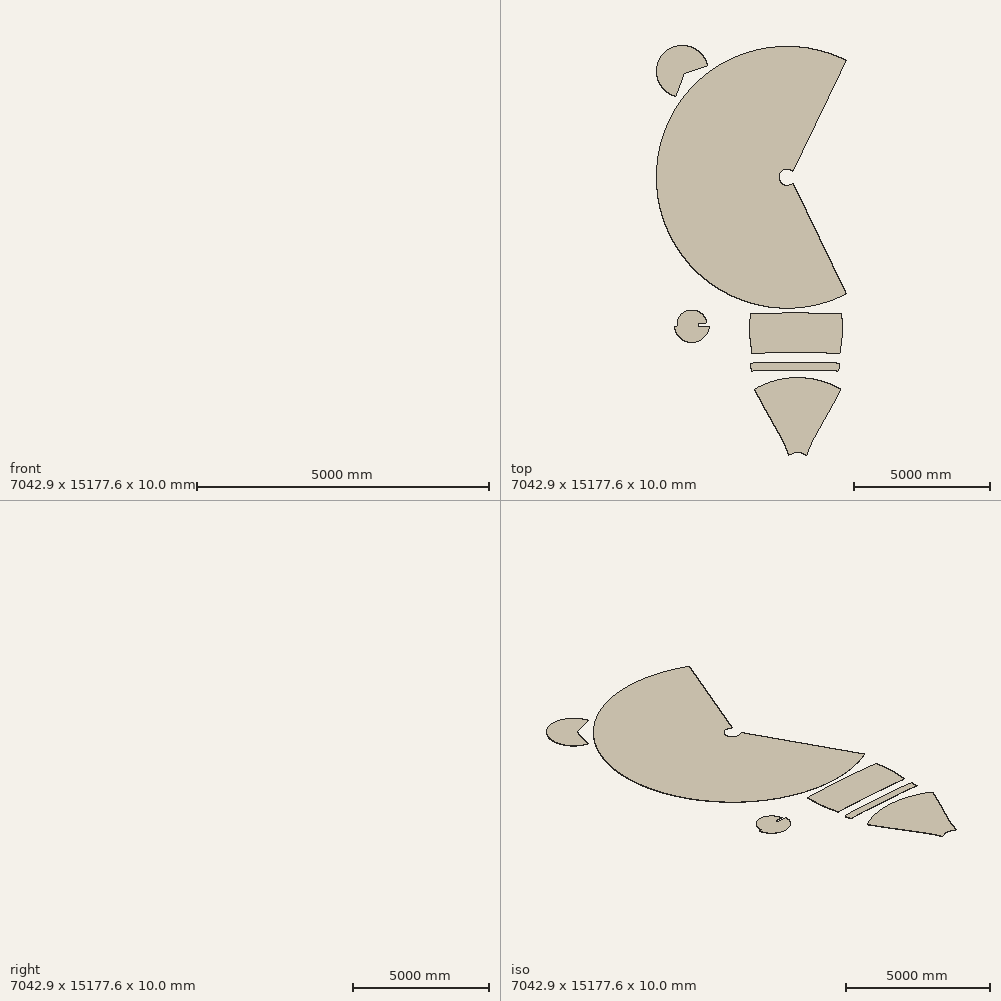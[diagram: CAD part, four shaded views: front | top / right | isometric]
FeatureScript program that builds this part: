
annotation { "Feature Type Name" : "Feature", "Feature Type Description" : "" }
export const myFeature = defineFeature(function(context is Context, id is Id, definition is map)
    precondition{}
    {
        {
            var Q0;
            Q0=qCreatedBy(makeId("Top.planeOp"),FACE);
            var sketch = newSketch(context, id + "F0", { "sketchPlane" : qUnion([Q0])});
            skLineSegment(sketch, "E0", {"start": v(3689.21, 4533.13) * mm, "end": v(3688.96, 4522.87) * mm});
            skLineSegment(sketch, "E1", {"start": v(3688.96, 4522.87) * mm, "end": v(3679.89, 4525.24) * mm});
            skLineSegment(sketch, "E2", {"start": v(3679.89, 4525.24) * mm, "end": v(3689.21, 4533.13) * mm});
            skLineSegment(sketch, "E3", {"start": v(4140.22, 4519.46) * mm, "end": v(4117.49, 4558.33) * mm});
            skLineSegment(sketch, "E4", {"start": v(4117.49, 4558.33) * mm, "end": v(4094.03, 4596.74) * mm});
            skLineSegment(sketch, "E5", {"start": v(4094.03, 4596.74) * mm, "end": v(4069.87, 4634.67) * mm});
            skLineSegment(sketch, "E6", {"start": v(4069.87, 4634.67) * mm, "end": v(4045.02, 4672.12) * mm});
            skLineSegment(sketch, "E7", {"start": v(4045.02, 4672.12) * mm, "end": v(4019.5, 4709.08) * mm});
            skLineSegment(sketch, "E8", {"start": v(4019.5, 4709.08) * mm, "end": v(3993.33, 4745.54) * mm});
            skLineSegment(sketch, "E9", {"start": v(3993.33, 4745.54) * mm, "end": v(3966.52, 4781.49) * mm});
            skLineSegment(sketch, "E10", {"start": v(3966.52, 4781.49) * mm, "end": v(3939.1, 4816.92) * mm});
            skLineSegment(sketch, "E11", {"start": v(3939.1, 4816.92) * mm, "end": v(3911.07, 4851.83) * mm});
            skLineSegment(sketch, "E12", {"start": v(3911.07, 4851.83) * mm, "end": v(3882.46, 4886.21) * mm});
            skLineSegment(sketch, "E13", {"start": v(3882.46, 4886.21) * mm, "end": v(3823.55, 4953.35) * mm});
            skLineSegment(sketch, "E14", {"start": v(3823.55, 4953.35) * mm, "end": v(3762.5, 5018.27) * mm});
            skLineSegment(sketch, "E15", {"start": v(3762.5, 5018.27) * mm, "end": v(3699.43, 5080.93) * mm});
            skLineSegment(sketch, "E16", {"start": v(3699.43, 5080.93) * mm, "end": v(3634.48, 5141.28) * mm});
            skLineSegment(sketch, "E17", {"start": v(3634.48, 5141.28) * mm, "end": v(3567.78, 5199.28) * mm});
            skLineSegment(sketch, "E18", {"start": v(3567.78, 5199.28) * mm, "end": v(3499.44, 5254.88) * mm});
            skLineSegment(sketch, "E19", {"start": v(3499.44, 5254.88) * mm, "end": v(3429.6, 5308.04) * mm});
            skLineSegment(sketch, "E20", {"start": v(3429.6, 5308.04) * mm, "end": v(3358.36, 5358.74) * mm});
            skLineSegment(sketch, "E21", {"start": v(3358.36, 5358.74) * mm, "end": v(3285.85, 5406.94) * mm});
            skLineSegment(sketch, "E22", {"start": v(3285.85, 5406.94) * mm, "end": v(3212.2, 5452.6) * mm});
            skLineSegment(sketch, "E23", {"start": v(3212.2, 5452.6) * mm, "end": v(3137.5, 5495.73) * mm});
            skLineSegment(sketch, "E24", {"start": v(3137.5, 5495.73) * mm, "end": v(3061.89, 5536.28) * mm});
            skLineSegment(sketch, "E25", {"start": v(3061.89, 5536.28) * mm, "end": v(2985.46, 5574.24) * mm});
            skLineSegment(sketch, "E26", {"start": v(2985.46, 5574.24) * mm, "end": v(2908.33, 5609.6) * mm});
            skLineSegment(sketch, "E27", {"start": v(2908.33, 5609.6) * mm, "end": v(2830.62, 5642.34) * mm});
            skLineSegment(sketch, "E28", {"start": v(2830.62, 5642.34) * mm, "end": v(2752.41, 5672.45) * mm});
            skLineSegment(sketch, "E29", {"start": v(2752.41, 5672.45) * mm, "end": v(2673.83, 5699.94) * mm});
            skLineSegment(sketch, "E30", {"start": v(2673.83, 5699.94) * mm, "end": v(2594.97, 5724.78) * mm});
            skLineSegment(sketch, "E31", {"start": v(2594.97, 5724.78) * mm, "end": v(2515.93, 5747) * mm});
            skLineSegment(sketch, "E32", {"start": v(2515.93, 5747) * mm, "end": v(2436.82, 5766.57) * mm});
            skLineSegment(sketch, "E33", {"start": v(2436.82, 5766.57) * mm, "end": v(2357.73, 5783.51) * mm});
            skLineSegment(sketch, "E34", {"start": v(2357.73, 5783.51) * mm, "end": v(2278.75, 5797.83) * mm});
            skLineSegment(sketch, "E35", {"start": v(2278.75, 5797.83) * mm, "end": v(2199.99, 5809.53) * mm});
            skLineSegment(sketch, "E36", {"start": v(2199.99, 5809.53) * mm, "end": v(2121.53, 5818.63) * mm});
            skLineSegment(sketch, "E37", {"start": v(2121.53, 5818.63) * mm, "end": v(2043.46, 5825.14) * mm});
            skLineSegment(sketch, "E38", {"start": v(2043.46, 5825.14) * mm, "end": v(1965.88, 5829.08) * mm});
            skLineSegment(sketch, "E39", {"start": v(1965.88, 5829.08) * mm, "end": v(1888.87, 5830.46) * mm});
            skLineSegment(sketch, "E40", {"start": v(1888.87, 5830.46) * mm, "end": v(1812.52, 5829.3) * mm});
            skLineSegment(sketch, "E41", {"start": v(1812.52, 5829.3) * mm, "end": v(1736.9, 5825.62) * mm});
            skLineSegment(sketch, "E42", {"start": v(1736.9, 5825.62) * mm, "end": v(1662.11, 5819.46) * mm});
            skLineSegment(sketch, "E43", {"start": v(1662.11, 5819.46) * mm, "end": v(1588.22, 5810.83) * mm});
            skLineSegment(sketch, "E44", {"start": v(1588.22, 5810.83) * mm, "end": v(1515.31, 5799.76) * mm});
            skLineSegment(sketch, "E45", {"start": v(1515.31, 5799.76) * mm, "end": v(1479.25, 5793.32) * mm});
            skLineSegment(sketch, "E46", {"start": v(1479.25, 5793.32) * mm, "end": v(1443.46, 5786.29) * mm});
            skLineSegment(sketch, "E47", {"start": v(1443.46, 5786.29) * mm, "end": v(1407.95, 5778.65) * mm});
            skLineSegment(sketch, "E48", {"start": v(1407.95, 5778.65) * mm, "end": v(1372.74, 5770.43) * mm});
            skLineSegment(sketch, "E49", {"start": v(1372.74, 5770.43) * mm, "end": v(1337.82, 5761.62) * mm});
            skLineSegment(sketch, "E50", {"start": v(1337.82, 5761.62) * mm, "end": v(1303.22, 5752.23) * mm});
            skLineSegment(sketch, "E51", {"start": v(1303.22, 5752.23) * mm, "end": v(1268.94, 5742.26) * mm});
            skLineSegment(sketch, "E52", {"start": v(1268.94, 5742.26) * mm, "end": v(1234.98, 5731.72) * mm});
            skLineSegment(sketch, "E53", {"start": v(1234.98, 5731.72) * mm, "end": v(1201.36, 5720.61) * mm});
            skLineSegment(sketch, "E54", {"start": v(1201.36, 5720.61) * mm, "end": v(1168.09, 5708.94) * mm});
            skLineSegment(sketch, "E55", {"start": v(1168.09, 5708.94) * mm, "end": v(1135.17, 5696.7) * mm});
            skLineSegment(sketch, "E56", {"start": v(1135.17, 5696.7) * mm, "end": v(1102.61, 5683.91) * mm});
            skLineSegment(sketch, "E57", {"start": v(1102.61, 5683.91) * mm, "end": v(1070.42, 5670.57) * mm});
            skLineSegment(sketch, "E58", {"start": v(1070.42, 5670.57) * mm, "end": v(1038.61, 5656.69) * mm});
            skLineSegment(sketch, "E59", {"start": v(1038.61, 5656.69) * mm, "end": v(1007.19, 5642.26) * mm});
            skLineSegment(sketch, "E60", {"start": v(1007.19, 5642.26) * mm, "end": v(976.16, 5627.3) * mm});
            skLineSegment(sketch, "E61", {"start": v(976.16, 5627.3) * mm, "end": v(945.53, 5611.8) * mm});
            skLineSegment(sketch, "E62", {"start": v(945.53, 5611.8) * mm, "end": v(915.31, 5595.79) * mm});
            skLineSegment(sketch, "E63", {"start": v(915.31, 5595.79) * mm, "end": v(885.51, 5579.25) * mm});
            skLineSegment(sketch, "E64", {"start": v(885.51, 5579.25) * mm, "end": v(856.14, 5562.2) * mm});
            skLineSegment(sketch, "E65", {"start": v(856.14, 5562.2) * mm, "end": v(827.2, 5544.64) * mm});
            skLineSegment(sketch, "E66", {"start": v(827.2, 5544.64) * mm, "end": v(798.69, 5526.58) * mm});
            skLineSegment(sketch, "E67", {"start": v(798.69, 5526.58) * mm, "end": v(770.63, 5508.01) * mm});
            skLineSegment(sketch, "E68", {"start": v(770.63, 5508.01) * mm, "end": v(743.03, 5488.96) * mm});
            skLineSegment(sketch, "E69", {"start": v(743.03, 5488.96) * mm, "end": v(715.88, 5469.42) * mm});
            skLineSegment(sketch, "E70", {"start": v(715.88, 5469.42) * mm, "end": v(689.2, 5449.4) * mm});
            skLineSegment(sketch, "E71", {"start": v(689.2, 5449.4) * mm, "end": v(663, 5428.9) * mm});
            skLineSegment(sketch, "E72", {"start": v(663, 5428.9) * mm, "end": v(637.28, 5407.92) * mm});
            skLineSegment(sketch, "E73", {"start": v(637.28, 5407.92) * mm, "end": v(612.05, 5386.5) * mm});
            skLineSegment(sketch, "E74", {"start": v(612.05, 5386.5) * mm, "end": v(587.3, 5364.6) * mm});
            skLineSegment(sketch, "E75", {"start": v(587.3, 5364.6) * mm, "end": v(563.06, 5342.25) * mm});
            skLineSegment(sketch, "E76", {"start": v(563.06, 5342.25) * mm, "end": v(539.33, 5319.46) * mm});
            skLineSegment(sketch, "E77", {"start": v(539.33, 5319.46) * mm, "end": v(516.1, 5296.23) * mm});
            skLineSegment(sketch, "E78", {"start": v(516.1, 5296.23) * mm, "end": v(493.4, 5272.56) * mm});
            skLineSegment(sketch, "E79", {"start": v(493.4, 5272.56) * mm, "end": v(471.22, 5248.47) * mm});
            skLineSegment(sketch, "E80", {"start": v(471.22, 5248.47) * mm, "end": v(449.57, 5223.95) * mm});
            skLineSegment(sketch, "E81", {"start": v(449.57, 5223.95) * mm, "end": v(428.45, 5199.01) * mm});
            skLineSegment(sketch, "E82", {"start": v(428.45, 5199.01) * mm, "end": v(407.88, 5173.67) * mm});
            skLineSegment(sketch, "E83", {"start": v(407.88, 5173.67) * mm, "end": v(387.85, 5147.92) * mm});
            skLineSegment(sketch, "E84", {"start": v(387.85, 5147.92) * mm, "end": v(368.37, 5121.77) * mm});
            skLineSegment(sketch, "E85", {"start": v(368.37, 5121.77) * mm, "end": v(349.45, 5095.23) * mm});
            skLineSegment(sketch, "E86", {"start": v(349.45, 5095.23) * mm, "end": v(331.1, 5068.3) * mm});
            skLineSegment(sketch, "E87", {"start": v(331.1, 5068.3) * mm, "end": v(313.3, 5041) * mm});
            skLineSegment(sketch, "E88", {"start": v(313.3, 5041) * mm, "end": v(296.08, 5013.33) * mm});
            skLineSegment(sketch, "E89", {"start": v(296.08, 5013.33) * mm, "end": v(279.44, 4985.28) * mm});
            skLineSegment(sketch, "E90", {"start": v(279.44, 4985.28) * mm, "end": v(263.38, 4956.88) * mm});
            skLineSegment(sketch, "E91", {"start": v(263.38, 4956.88) * mm, "end": v(247.9, 4928.12) * mm});
            skLineSegment(sketch, "E92", {"start": v(247.9, 4928.12) * mm, "end": v(233.02, 4899) * mm});
            skLineSegment(sketch, "E93", {"start": v(233.02, 4899) * mm, "end": v(218.73, 4869.56) * mm});
            skLineSegment(sketch, "E94", {"start": v(218.73, 4869.56) * mm, "end": v(205.04, 4839.77) * mm});
            skLineSegment(sketch, "E95", {"start": v(205.04, 4839.77) * mm, "end": v(191.95, 4809.65) * mm});
            skLineSegment(sketch, "E96", {"start": v(191.95, 4809.65) * mm, "end": v(179.47, 4779.21) * mm});
            skLineSegment(sketch, "E97", {"start": v(179.47, 4779.21) * mm, "end": v(167.6, 4748.46) * mm});
            skLineSegment(sketch, "E98", {"start": v(167.6, 4748.46) * mm, "end": v(156.35, 4717.4) * mm});
            skLineSegment(sketch, "E99", {"start": v(156.35, 4717.4) * mm, "end": v(145.72, 4686.02) * mm});
            skLineSegment(sketch, "E100", {"start": v(145.72, 4686.02) * mm, "end": v(135.7, 4654.35) * mm});
            skLineSegment(sketch, "E101", {"start": v(135.7, 4654.35) * mm, "end": v(126.32, 4622.39) * mm});
            skLineSegment(sketch, "E102", {"start": v(126.32, 4622.39) * mm, "end": v(117.57, 4590.14) * mm});
            skLineSegment(sketch, "E103", {"start": v(117.57, 4590.14) * mm, "end": v(109.45, 4557.61) * mm});
            skLineSegment(sketch, "E104", {"start": v(109.45, 4557.61) * mm, "end": v(101.96, 4524.81) * mm});
            skLineSegment(sketch, "E105", {"start": v(101.96, 4524.81) * mm, "end": v(95.11, 4491.74) * mm});
            skLineSegment(sketch, "E106", {"start": v(95.11, 4491.74) * mm, "end": v(88.9, 4458.41) * mm});
            skLineSegment(sketch, "E107", {"start": v(88.9, 4458.41) * mm, "end": v(83.35, 4424.83) * mm});
            skLineSegment(sketch, "E108", {"start": v(83.35, 4424.83) * mm, "end": v(78.44, 4391) * mm});
            skLineSegment(sketch, "E109", {"start": v(78.44, 4391) * mm, "end": v(74.18, 4356.92) * mm});
            skLineSegment(sketch, "E110", {"start": v(74.18, 4356.92) * mm, "end": v(70.57, 4322.6) * mm});
            skLineSegment(sketch, "E111", {"start": v(70.57, 4322.6) * mm, "end": v(67.62, 4288.06) * mm});
            skLineSegment(sketch, "E112", {"start": v(67.62, 4288.06) * mm, "end": v(65.33, 4253.3) * mm});
            skLineSegment(sketch, "E113", {"start": v(65.33, 4253.3) * mm, "end": v(63.7, 4218.3) * mm});
            skLineSegment(sketch, "E114", {"start": v(63.7, 4218.3) * mm, "end": v(62.73, 4183.1) * mm});
            skLineSegment(sketch, "E115", {"start": v(62.73, 4183.1) * mm, "end": v(62.42, 4147.69) * mm});
            skLineSegment(sketch, "E116", {"start": v(62.42, 4147.69) * mm, "end": v(62.78, 4112.07) * mm});
            skLineSegment(sketch, "E117", {"start": v(62.78, 4112.07) * mm, "end": v(63.81, 4076.27) * mm});
            skLineSegment(sketch, "E118", {"start": v(63.81, 4076.27) * mm, "end": v(65.51, 4040.27) * mm});
            skLineSegment(sketch, "E119", {"start": v(65.51, 4040.27) * mm, "end": v(67.89, 4004.08) * mm});
            skLineSegment(sketch, "E120", {"start": v(67.89, 4004.08) * mm, "end": v(70.93, 3967.72) * mm});
            skLineSegment(sketch, "E121", {"start": v(70.93, 3967.72) * mm, "end": v(74.66, 3931.18) * mm});
            skLineSegment(sketch, "E122", {"start": v(74.66, 3931.18) * mm, "end": v(79.05, 3894.48) * mm});
            skLineSegment(sketch, "E123", {"start": v(79.05, 3894.48) * mm, "end": v(89.88, 3820.58) * mm});
            skLineSegment(sketch, "E124", {"start": v(89.88, 3820.58) * mm, "end": v(103.44, 3746.07) * mm});
            skLineSegment(sketch, "E125", {"start": v(103.44, 3746.07) * mm, "end": v(119.71, 3671) * mm});
            skLineSegment(sketch, "E126", {"start": v(119.71, 3671) * mm, "end": v(138.72, 3595.4) * mm});
            skLineSegment(sketch, "E127", {"start": v(138.72, 3595.4) * mm, "end": v(160.46, 3519.3) * mm});
            skLineSegment(sketch, "E128", {"start": v(160.46, 3519.3) * mm, "end": v(184.95, 3442.76) * mm});
            skLineSegment(sketch, "E129", {"start": v(184.95, 3442.76) * mm, "end": v(212.17, 3365.8) * mm});
            skLineSegment(sketch, "E130", {"start": v(212.17, 3365.8) * mm, "end": v(242.13, 3288.46) * mm});
            skLineSegment(sketch, "E131", {"start": v(242.13, 3288.46) * mm, "end": v(274.82, 3210.77) * mm});
            skLineSegment(sketch, "E132", {"start": v(274.82, 3210.77) * mm, "end": v(310.24, 3132.76) * mm});
            skLineSegment(sketch, "E133", {"start": v(310.24, 3132.76) * mm, "end": v(348.39, 3054.47) * mm});
            skLineSegment(sketch, "E134", {"start": v(348.39, 3054.47) * mm, "end": v(389.25, 2975.93) * mm});
            skLineSegment(sketch, "E135", {"start": v(389.25, 2975.93) * mm, "end": v(432.82, 2897.15) * mm});
            skLineSegment(sketch, "E136", {"start": v(432.82, 2897.15) * mm, "end": v(479.1, 2818.17) * mm});
            skLineSegment(sketch, "E137", {"start": v(479.1, 2818.17) * mm, "end": v(528.04, 2739) * mm});
            skLineSegment(sketch, "E138", {"start": v(528.04, 2739) * mm, "end": v(579.66, 2659.68) * mm});
            skLineSegment(sketch, "E139", {"start": v(579.66, 2659.68) * mm, "end": v(633.94, 2580.2) * mm});
            skLineSegment(sketch, "E140", {"start": v(633.94, 2580.2) * mm, "end": v(690.85, 2500.62) * mm});
            skLineSegment(sketch, "E141", {"start": v(690.85, 2500.62) * mm, "end": v(750.38, 2420.92) * mm});
            skLineSegment(sketch, "E142", {"start": v(750.38, 2420.92) * mm, "end": v(812.5, 2341.12) * mm});
            skLineSegment(sketch, "E143", {"start": v(812.5, 2341.12) * mm, "end": v(877.2, 2261.24) * mm});
            skLineSegment(sketch, "E144", {"start": v(877.2, 2261.24) * mm, "end": v(944.46, 2181.27) * mm});
            skLineSegment(sketch, "E145", {"start": v(944.46, 2181.27) * mm, "end": v(1086.5, 2021.14) * mm});
            skLineSegment(sketch, "E146", {"start": v(1086.5, 2021.14) * mm, "end": v(1238.44, 1860.72) * mm});
            skLineSegment(sketch, "E147", {"start": v(1238.44, 1860.72) * mm, "end": v(1400, 1700) * mm});
            skLineSegment(sketch, "E148", {"start": v(1400, 1700) * mm, "end": v(1570.92, 1538.9) * mm});
            skLineSegment(sketch, "E149", {"start": v(1570.92, 1538.9) * mm, "end": v(1750.89, 1377.31) * mm});
            skLineSegment(sketch, "E150", {"start": v(1750.89, 1377.31) * mm, "end": v(1939.6, 1215.06) * mm});
            skLineSegment(sketch, "E151", {"start": v(1939.6, 1215.06) * mm, "end": v(2136.68, 1051.94) * mm});
            skLineSegment(sketch, "E152", {"start": v(2136.68, 1051.94) * mm, "end": v(2554.47, 721.93) * mm});
            skLineSegment(sketch, "E153", {"start": v(2554.47, 721.93) * mm, "end": v(3000.97, 384.44) * mm});
            skLineSegment(sketch, "E154", {"start": v(3000.97, 384.44) * mm, "end": v(3964.87, -329.08) * mm});
            skLineSegment(sketch, "E155", {"start": v(1447.12, 4527.46) * mm, "end": v(1247.66, 4747.46) * mm});
            skLineSegment(sketch, "E156", {"start": v(1513.24, 4570.67) * mm, "end": v(1323.36, 4814.66) * mm});
            skLineSegment(sketch, "E157", {"start": v(4034.03, 4649.95) * mm, "end": v(4487.9, 4649.95) * mm});
            skLineSegment(sketch, "E158", {"start": v(4034.03, 4772.78) * mm, "end": v(4487.9, 4772.78) * mm});
            skLineSegment(sketch, "E159", {"start": v(4487.9, 4772.78) * mm, "end": v(4487.9, 4527.12) * mm});
            skLineSegment(sketch, "E160", {"start": v(4487.9, 4527.12) * mm, "end": v(4034.03, 4527.12) * mm});
            skLineSegment(sketch, "E161", {"start": v(4034.03, 4527.12) * mm, "end": v(4034.03, 4772.78) * mm});
            skLineSegment(sketch, "E162", {"start": v(3708.57, 4527.12) * mm, "end": v(4809.75, 4527.12) * mm});
            skLineSegment(sketch, "E163", {"start": v(3672.75, 4500.41) * mm, "end": v(3636.94, 4473.7) * mm});
            skLineSegment(sketch, "E164", {"start": v(3704.91, 4531.44) * mm, "end": v(3669.18, 4504.72) * mm});
            skLineSegment(sketch, "E165", {"start": v(3669.18, 4504.72) * mm, "end": v(3628.22, 4500.41) * mm});
            skLineSegment(sketch, "E166", {"start": v(3711.49, 4523.63) * mm, "end": v(3675.46, 4495.62) * mm});
            skLineSegment(sketch, "E167", {"start": v(3675.46, 4495.62) * mm, "end": v(3664.7, 4457.04) * mm});
            skLineSegment(sketch, "E168", {"start": v(3672.75, 4500.41) * mm, "end": v(3708.57, 4527.12) * mm});
            skLineSegment(sketch, "E169", {"start": v(3685.87, 4527.86) * mm, "end": v(3654.62, 4550.77) * mm});
            skLineSegment(sketch, "E170", {"start": v(3654.62, 4550.77) * mm, "end": v(3485.23, 4535.65) * mm});
            skLineSegment(sketch, "E171", {"start": v(1299.6, 3557.02) * mm, "end": v(1190.33, 3465.32) * mm});
            skLineSegment(sketch, "E172", {"start": v(3708.57, 4527.12) * mm, "end": v(3765.21, 4574.65) * mm});
            skCircle(sketch, "E173", {"center": v(1186.85, 9802.11) * mm, "radius": 552.4 * mm});
            skCircle(sketch, "E174", {"center": v(1186.85, 9802.11) * mm, "radius": 652.4 * mm});
            skLineSegment(sketch, "E175", {"start": v(932.85, 9722.74) * mm, "end": v(1440.85, 9722.74) * mm});
            skLineSegment(sketch, "E176", {"start": v(932.85, 9881.49) * mm, "end": v(1440.85, 9881.49) * mm});
            skLineSegment(sketch, "E177", {"start": v(932.85, 9960.86) * mm, "end": v(1440.85, 9960.86) * mm});
            skLineSegment(sketch, "E178", {"start": v(1440.85, 9960.86) * mm, "end": v(1440.85, 9643.36) * mm});
            skLineSegment(sketch, "E179", {"start": v(1440.85, 9643.36) * mm, "end": v(932.85, 9643.36) * mm});
            skLineSegment(sketch, "E180", {"start": v(932.85, 9643.36) * mm, "end": v(932.85, 9960.86) * mm});
            skLineSegment(sketch, "E181", {"start": v(1837.34, 9752.11) * mm, "end": v(536.37, 9752.11) * mm});
            skLineSegment(sketch, "E182", {"start": v(1837.34, 9852.11) * mm, "end": v(536.37, 9852.11) * mm});
            skLineSegment(sketch, "E183", {"start": v(6519.23, 8294.43) * mm, "end": v(6493.53, 8297.42) * mm});
            skLineSegment(sketch, "E184", {"start": v(6493.53, 8297.42) * mm, "end": v(6467.82, 8300.22) * mm});
            skLineSegment(sketch, "E185", {"start": v(6467.82, 8300.22) * mm, "end": v(6442.09, 8302.82) * mm});
            skLineSegment(sketch, "E186", {"start": v(6442.09, 8302.82) * mm, "end": v(6416.34, 8305.23) * mm});
            skLineSegment(sketch, "E187", {"start": v(6416.34, 8305.23) * mm, "end": v(6390.59, 8307.47) * mm});
            skLineSegment(sketch, "E188", {"start": v(6390.59, 8307.47) * mm, "end": v(6364.82, 8309.52) * mm});
            skLineSegment(sketch, "E189", {"start": v(6364.82, 8309.52) * mm, "end": v(6339.7, 8311.37) * mm});
            skLineSegment(sketch, "E190", {"start": v(6339.7, 8311.37) * mm, "end": v(6314.74, 8313.05) * mm});
            skLineSegment(sketch, "E191", {"start": v(6314.74, 8313.05) * mm, "end": v(6289.79, 8314.59) * mm});
            skLineSegment(sketch, "E192", {"start": v(6289.79, 8314.59) * mm, "end": v(6264.83, 8315.98) * mm});
            skLineSegment(sketch, "E193", {"start": v(6264.83, 8315.98) * mm, "end": v(6239.88, 8317.24) * mm});
            skLineSegment(sketch, "E194", {"start": v(6239.88, 8317.24) * mm, "end": v(6214.93, 8318.37) * mm});
            skLineSegment(sketch, "E195", {"start": v(6214.93, 8318.37) * mm, "end": v(6189.98, 8319.36) * mm});
            skLineSegment(sketch, "E196", {"start": v(6189.98, 8319.36) * mm, "end": v(6165.04, 8320.24) * mm});
            skLineSegment(sketch, "E197", {"start": v(6165.04, 8320.24) * mm, "end": v(6140.1, 8321) * mm});
            skLineSegment(sketch, "E198", {"start": v(6140.1, 8321) * mm, "end": v(6115.17, 8321.65) * mm});
            skLineSegment(sketch, "E199", {"start": v(6115.17, 8321.65) * mm, "end": v(6090.25, 8322.2) * mm});
            skLineSegment(sketch, "E200", {"start": v(6090.25, 8322.2) * mm, "end": v(6065.33, 8322.66) * mm});
            skLineSegment(sketch, "E201", {"start": v(6065.33, 8322.66) * mm, "end": v(6040.43, 8323.03) * mm});
            skLineSegment(sketch, "E202", {"start": v(6040.43, 8323.03) * mm, "end": v(6015.53, 8323.33) * mm});
            skLineSegment(sketch, "E203", {"start": v(6015.53, 8323.33) * mm, "end": v(5990.65, 8323.55) * mm});
            skLineSegment(sketch, "E204", {"start": v(5990.65, 8323.55) * mm, "end": v(5965.77, 8323.7) * mm});
            skLineSegment(sketch, "E205", {"start": v(5965.77, 8323.7) * mm, "end": v(5940.9, 8323.8) * mm});
            skLineSegment(sketch, "E206", {"start": v(5940.9, 8323.8) * mm, "end": v(5916.04, 8323.83) * mm});
            skLineSegment(sketch, "E207", {"start": v(5916.04, 8323.83) * mm, "end": v(5891.2, 8323.81) * mm});
            skLineSegment(sketch, "E208", {"start": v(5891.2, 8323.81) * mm, "end": v(5866.35, 8323.75) * mm});
            skLineSegment(sketch, "E209", {"start": v(5866.35, 8323.75) * mm, "end": v(5841.52, 8323.64) * mm});
            skLineSegment(sketch, "E210", {"start": v(5841.52, 8323.64) * mm, "end": v(5816.7, 8323.5) * mm});
            skLineSegment(sketch, "E211", {"start": v(5816.7, 8323.5) * mm, "end": v(5791.89, 8323.32) * mm});
            skLineSegment(sketch, "E212", {"start": v(5791.89, 8323.32) * mm, "end": v(5767.08, 8323.12) * mm});
            skLineSegment(sketch, "E213", {"start": v(5767.08, 8323.12) * mm, "end": v(5742.28, 8322.9) * mm});
            skLineSegment(sketch, "E214", {"start": v(5742.28, 8322.9) * mm, "end": v(5717.5, 8322.66) * mm});
            skLineSegment(sketch, "E215", {"start": v(5717.5, 8322.66) * mm, "end": v(5692.7, 8322.41) * mm});
            skLineSegment(sketch, "E216", {"start": v(5692.7, 8322.41) * mm, "end": v(5667.93, 8322.15) * mm});
            skLineSegment(sketch, "E217", {"start": v(5667.93, 8322.15) * mm, "end": v(5643.15, 8321.88) * mm});
            skLineSegment(sketch, "E218", {"start": v(5643.15, 8321.88) * mm, "end": v(5618.39, 8321.6) * mm});
            skLineSegment(sketch, "E219", {"start": v(5618.39, 8321.6) * mm, "end": v(5593.62, 8321.32) * mm});
            skLineSegment(sketch, "E220", {"start": v(5593.62, 8321.32) * mm, "end": v(5569.07, 8321.05) * mm});
            skLineSegment(sketch, "E221", {"start": v(5569.07, 8321.05) * mm, "end": v(5544.6, 8320.78) * mm});
            skLineSegment(sketch, "E222", {"start": v(5544.6, 8320.78) * mm, "end": v(5520.14, 8320.52) * mm});
            skLineSegment(sketch, "E223", {"start": v(5520.14, 8320.52) * mm, "end": v(5495.68, 8320.26) * mm});
            skLineSegment(sketch, "E224", {"start": v(5495.68, 8320.26) * mm, "end": v(5471.22, 8320) * mm});
            skLineSegment(sketch, "E225", {"start": v(5471.22, 8320) * mm, "end": v(5446.77, 8319.76) * mm});
            skLineSegment(sketch, "E226", {"start": v(5446.77, 8319.76) * mm, "end": v(5422.32, 8319.53) * mm});
            skLineSegment(sketch, "E227", {"start": v(5422.32, 8319.53) * mm, "end": v(5397.87, 8319.3) * mm});
            skLineSegment(sketch, "E228", {"start": v(5397.87, 8319.3) * mm, "end": v(5373.42, 8319.08) * mm});
            skLineSegment(sketch, "E229", {"start": v(5373.42, 8319.08) * mm, "end": v(5348.98, 8318.88) * mm});
            skLineSegment(sketch, "E230", {"start": v(5348.98, 8318.88) * mm, "end": v(5324.54, 8318.68) * mm});
            skLineSegment(sketch, "E231", {"start": v(5324.54, 8318.68) * mm, "end": v(5300.1, 8318.5) * mm});
            skLineSegment(sketch, "E232", {"start": v(5300.1, 8318.5) * mm, "end": v(5275.66, 8318.33) * mm});
            skLineSegment(sketch, "E233", {"start": v(5275.66, 8318.33) * mm, "end": v(5251.23, 8318.18) * mm});
            skLineSegment(sketch, "E234", {"start": v(5251.23, 8318.18) * mm, "end": v(5226.8, 8318.04) * mm});
            skLineSegment(sketch, "E235", {"start": v(5226.8, 8318.04) * mm, "end": v(5202.36, 8317.91) * mm});
            skLineSegment(sketch, "E236", {"start": v(5202.36, 8317.91) * mm, "end": v(5177.93, 8317.8) * mm});
            skLineSegment(sketch, "E237", {"start": v(5177.93, 8317.8) * mm, "end": v(5153.5, 8317.71) * mm});
            skLineSegment(sketch, "E238", {"start": v(5153.5, 8317.71) * mm, "end": v(5129.07, 8317.63) * mm});
            skLineSegment(sketch, "E239", {"start": v(5129.07, 8317.63) * mm, "end": v(5104.64, 8317.56) * mm});
            skLineSegment(sketch, "E240", {"start": v(5104.64, 8317.56) * mm, "end": v(5080.2, 8317.5) * mm});
            skLineSegment(sketch, "E241", {"start": v(5080.2, 8317.5) * mm, "end": v(5055.78, 8317.45) * mm});
            skLineSegment(sketch, "E242", {"start": v(5055.78, 8317.45) * mm, "end": v(5031.35, 8317.43) * mm});
            skLineSegment(sketch, "E243", {"start": v(5031.35, 8317.43) * mm, "end": v(5006.93, 8317.41) * mm});
            skLineSegment(sketch, "E244", {"start": v(5006.93, 8317.41) * mm, "end": v(4982.5, 8317.42) * mm});
            skLineSegment(sketch, "E245", {"start": v(4982.5, 8317.42) * mm, "end": v(4958.07, 8317.44) * mm});
            skLineSegment(sketch, "E246", {"start": v(4958.07, 8317.44) * mm, "end": v(4933.65, 8317.47) * mm});
            skLineSegment(sketch, "E247", {"start": v(4933.65, 8317.47) * mm, "end": v(4909.22, 8317.52) * mm});
            skLineSegment(sketch, "E248", {"start": v(4909.22, 8317.52) * mm, "end": v(4884.79, 8317.58) * mm});
            skLineSegment(sketch, "E249", {"start": v(4884.79, 8317.58) * mm, "end": v(4860.36, 8317.66) * mm});
            skLineSegment(sketch, "E250", {"start": v(4860.36, 8317.66) * mm, "end": v(4835.93, 8317.74) * mm});
            skLineSegment(sketch, "E251", {"start": v(4835.93, 8317.74) * mm, "end": v(4811.5, 8317.84) * mm});
            skLineSegment(sketch, "E252", {"start": v(4811.5, 8317.84) * mm, "end": v(4787.07, 8317.96) * mm});
            skLineSegment(sketch, "E253", {"start": v(4787.07, 8317.96) * mm, "end": v(4762.63, 8318.1) * mm});
            skLineSegment(sketch, "E254", {"start": v(4762.63, 8318.1) * mm, "end": v(4738.2, 8318.24) * mm});
            skLineSegment(sketch, "E255", {"start": v(4738.2, 8318.24) * mm, "end": v(4713.76, 8318.4) * mm});
            skLineSegment(sketch, "E256", {"start": v(4713.76, 8318.4) * mm, "end": v(4689.33, 8318.58) * mm});
            skLineSegment(sketch, "E257", {"start": v(4689.33, 8318.58) * mm, "end": v(4664.89, 8318.77) * mm});
            skLineSegment(sketch, "E258", {"start": v(4664.89, 8318.77) * mm, "end": v(4640.45, 8318.98) * mm});
            skLineSegment(sketch, "E259", {"start": v(4640.45, 8318.98) * mm, "end": v(4616, 8319.19) * mm});
            skLineSegment(sketch, "E260", {"start": v(4616, 8319.19) * mm, "end": v(4591.56, 8319.41) * mm});
            skLineSegment(sketch, "E261", {"start": v(4591.56, 8319.41) * mm, "end": v(4567.1, 8319.65) * mm});
            skLineSegment(sketch, "E262", {"start": v(4567.1, 8319.65) * mm, "end": v(4542.66, 8319.9) * mm});
            skLineSegment(sketch, "E263", {"start": v(4542.66, 8319.9) * mm, "end": v(4518.2, 8320.15) * mm});
            skLineSegment(sketch, "E264", {"start": v(4518.2, 8320.15) * mm, "end": v(4493.75, 8320.4) * mm});
            skLineSegment(sketch, "E265", {"start": v(4493.75, 8320.4) * mm, "end": v(4469.28, 8320.68) * mm});
            skLineSegment(sketch, "E266", {"start": v(4469.28, 8320.68) * mm, "end": v(4444.82, 8320.96) * mm});
            skLineSegment(sketch, "E267", {"start": v(4444.82, 8320.96) * mm, "end": v(4420.35, 8321.23) * mm});
            skLineSegment(sketch, "E268", {"start": v(4420.35, 8321.23) * mm, "end": v(4395.88, 8321.52) * mm});
            skLineSegment(sketch, "E269", {"start": v(4395.88, 8321.52) * mm, "end": v(4371.4, 8321.8) * mm});
            skLineSegment(sketch, "E270", {"start": v(4371.4, 8321.8) * mm, "end": v(4346.91, 8322.07) * mm});
            skLineSegment(sketch, "E271", {"start": v(4346.91, 8322.07) * mm, "end": v(4322.42, 8322.34) * mm});
            skLineSegment(sketch, "E272", {"start": v(4322.42, 8322.34) * mm, "end": v(4297.93, 8322.6) * mm});
            skLineSegment(sketch, "E273", {"start": v(4297.93, 8322.6) * mm, "end": v(4273.42, 8322.84) * mm});
            skLineSegment(sketch, "E274", {"start": v(4273.42, 8322.84) * mm, "end": v(4248.92, 8323.07) * mm});
            skLineSegment(sketch, "E275", {"start": v(4248.92, 8323.07) * mm, "end": v(4224.4, 8323.28) * mm});
            skLineSegment(sketch, "E276", {"start": v(4224.4, 8323.28) * mm, "end": v(4199.88, 8323.47) * mm});
            skLineSegment(sketch, "E277", {"start": v(4199.88, 8323.47) * mm, "end": v(4175.35, 8323.63) * mm});
            skLineSegment(sketch, "E278", {"start": v(4175.35, 8323.63) * mm, "end": v(4150.81, 8323.76) * mm});
            skLineSegment(sketch, "E279", {"start": v(4150.81, 8323.76) * mm, "end": v(4126.26, 8323.85) * mm});
            skLineSegment(sketch, "E280", {"start": v(4126.26, 8323.85) * mm, "end": v(4101.7, 8323.9) * mm});
            skLineSegment(sketch, "E281", {"start": v(4101.7, 8323.9) * mm, "end": v(4077.14, 8323.89) * mm});
            skLineSegment(sketch, "E282", {"start": v(4077.14, 8323.89) * mm, "end": v(4052.56, 8323.83) * mm});
            skLineSegment(sketch, "E283", {"start": v(4052.56, 8323.83) * mm, "end": v(4027.98, 8323.72) * mm});
            skLineSegment(sketch, "E284", {"start": v(4027.98, 8323.72) * mm, "end": v(4003.39, 8323.54) * mm});
            skLineSegment(sketch, "E285", {"start": v(4003.39, 8323.54) * mm, "end": v(3978.79, 8323.3) * mm});
            skLineSegment(sketch, "E286", {"start": v(3978.79, 8323.3) * mm, "end": v(3954.18, 8322.98) * mm});
            skLineSegment(sketch, "E287", {"start": v(3954.18, 8322.98) * mm, "end": v(3929.56, 8322.58) * mm});
            skLineSegment(sketch, "E288", {"start": v(3929.56, 8322.58) * mm, "end": v(3904.93, 8322.1) * mm});
            skLineSegment(sketch, "E289", {"start": v(3904.93, 8322.1) * mm, "end": v(3880.3, 8321.52) * mm});
            skLineSegment(sketch, "E290", {"start": v(3880.3, 8321.52) * mm, "end": v(3855.65, 8320.84) * mm});
            skLineSegment(sketch, "E291", {"start": v(3855.65, 8320.84) * mm, "end": v(3831, 8320.05) * mm});
            skLineSegment(sketch, "E292", {"start": v(3831, 8320.05) * mm, "end": v(3806.34, 8319.14) * mm});
            skLineSegment(sketch, "E293", {"start": v(3806.34, 8319.14) * mm, "end": v(3781.68, 8318.12) * mm});
            skLineSegment(sketch, "E294", {"start": v(3781.68, 8318.12) * mm, "end": v(3757.02, 8316.98) * mm});
            skLineSegment(sketch, "E295", {"start": v(3757.02, 8316.98) * mm, "end": v(3732.36, 8315.7) * mm});
            skLineSegment(sketch, "E296", {"start": v(3732.36, 8315.7) * mm, "end": v(3707.7, 8314.28) * mm});
            skLineSegment(sketch, "E297", {"start": v(3707.7, 8314.28) * mm, "end": v(3683.02, 8312.73) * mm});
            skLineSegment(sketch, "E298", {"start": v(3683.02, 8312.73) * mm, "end": v(3658.36, 8311.03) * mm});
            skLineSegment(sketch, "E299", {"start": v(3658.36, 8311.03) * mm, "end": v(3633.7, 8309.18) * mm});
            skLineSegment(sketch, "E300", {"start": v(3633.7, 8309.18) * mm, "end": v(3609.04, 8307.17) * mm});
            skLineSegment(sketch, "E301", {"start": v(3609.04, 8307.17) * mm, "end": v(3584.4, 8305) * mm});
            skLineSegment(sketch, "E302", {"start": v(3584.4, 8305) * mm, "end": v(3559.75, 8302.67) * mm});
            skLineSegment(sketch, "E303", {"start": v(3559.75, 8302.67) * mm, "end": v(3535.13, 8300.16) * mm});
            skLineSegment(sketch, "E304", {"start": v(3535.13, 8300.16) * mm, "end": v(3510.51, 8297.47) * mm});
            skLineSegment(sketch, "E305", {"start": v(3510.51, 8297.47) * mm, "end": v(3485.92, 8294.61) * mm});
            skLineSegment(sketch, "E306", {"start": v(3485.92, 8294.61) * mm, "end": v(3461.34, 8291.58) * mm});
            skLineSegment(sketch, "E307", {"start": v(3461.34, 8291.58) * mm, "end": v(3462.78, 8280.2) * mm});
            skLineSegment(sketch, "E308", {"start": v(3462.78, 8280.2) * mm, "end": v(3464.23, 8268.84) * mm});
            skLineSegment(sketch, "E309", {"start": v(3464.23, 8268.84) * mm, "end": v(3465.68, 8257.46) * mm});
            skLineSegment(sketch, "E310", {"start": v(3465.68, 8257.46) * mm, "end": v(3467.13, 8246.03) * mm});
            skLineSegment(sketch, "E311", {"start": v(3467.13, 8246.03) * mm, "end": v(3468.58, 8234.65) * mm});
            skLineSegment(sketch, "E312", {"start": v(3468.58, 8234.65) * mm, "end": v(3470.03, 8223.29) * mm});
            skLineSegment(sketch, "E313", {"start": v(3470.03, 8223.29) * mm, "end": v(3471.48, 8211.91) * mm});
            skLineSegment(sketch, "E314", {"start": v(3471.48, 8211.91) * mm, "end": v(3472.94, 8200.49) * mm});
            skLineSegment(sketch, "E315", {"start": v(3472.94, 8200.49) * mm, "end": v(3496.94, 8203.44) * mm});
            skLineSegment(sketch, "E316", {"start": v(3496.94, 8203.44) * mm, "end": v(3520.96, 8206.23) * mm});
            skLineSegment(sketch, "E317", {"start": v(3520.96, 8206.23) * mm, "end": v(3545, 8208.85) * mm});
            skLineSegment(sketch, "E318", {"start": v(3545, 8208.85) * mm, "end": v(3569.05, 8211.3) * mm});
            skLineSegment(sketch, "E319", {"start": v(3569.05, 8211.3) * mm, "end": v(3593.14, 8213.58) * mm});
            skLineSegment(sketch, "E320", {"start": v(3593.14, 8213.58) * mm, "end": v(3617.24, 8215.7) * mm});
            skLineSegment(sketch, "E321", {"start": v(3617.24, 8215.7) * mm, "end": v(3641.36, 8217.65) * mm});
            skLineSegment(sketch, "E322", {"start": v(3641.36, 8217.65) * mm, "end": v(3665.5, 8219.46) * mm});
            skLineSegment(sketch, "E323", {"start": v(3665.5, 8219.46) * mm, "end": v(3689.65, 8221.11) * mm});
            skLineSegment(sketch, "E324", {"start": v(3689.65, 8221.11) * mm, "end": v(3713.82, 8222.62) * mm});
            skLineSegment(sketch, "E325", {"start": v(3713.82, 8222.62) * mm, "end": v(3738, 8224) * mm});
            skLineSegment(sketch, "E326", {"start": v(3738, 8224) * mm, "end": v(3762.2, 8225.26) * mm});
            skLineSegment(sketch, "E327", {"start": v(3762.2, 8225.26) * mm, "end": v(3786.42, 8226.38) * mm});
            skLineSegment(sketch, "E328", {"start": v(3786.42, 8226.38) * mm, "end": v(3810.65, 8227.38) * mm});
            skLineSegment(sketch, "E329", {"start": v(3810.65, 8227.38) * mm, "end": v(3834.89, 8228.26) * mm});
            skLineSegment(sketch, "E330", {"start": v(3834.89, 8228.26) * mm, "end": v(3859.14, 8229.04) * mm});
            skLineSegment(sketch, "E331", {"start": v(3859.14, 8229.04) * mm, "end": v(3883.41, 8229.7) * mm});
            skLineSegment(sketch, "E332", {"start": v(3883.41, 8229.7) * mm, "end": v(3907.7, 8230.27) * mm});
            skLineSegment(sketch, "E333", {"start": v(3907.7, 8230.27) * mm, "end": v(3931.98, 8230.75) * mm});
            skLineSegment(sketch, "E334", {"start": v(3931.98, 8230.75) * mm, "end": v(3956.28, 8231.14) * mm});
            skLineSegment(sketch, "E335", {"start": v(3956.28, 8231.14) * mm, "end": v(3980.6, 8231.45) * mm});
            skLineSegment(sketch, "E336", {"start": v(3980.6, 8231.45) * mm, "end": v(4004.92, 8231.69) * mm});
            skLineSegment(sketch, "E337", {"start": v(4004.92, 8231.69) * mm, "end": v(4029.25, 8231.86) * mm});
            skLineSegment(sketch, "E338", {"start": v(4029.25, 8231.86) * mm, "end": v(4053.6, 8231.97) * mm});
            skLineSegment(sketch, "E339", {"start": v(4053.6, 8231.97) * mm, "end": v(4077.94, 8232.02) * mm});
            skLineSegment(sketch, "E340", {"start": v(4077.94, 8232.02) * mm, "end": v(4102.3, 8232.02) * mm});
            skLineSegment(sketch, "E341", {"start": v(4102.3, 8232.02) * mm, "end": v(4126.67, 8231.97) * mm});
            skLineSegment(sketch, "E342", {"start": v(4126.67, 8231.97) * mm, "end": v(4151.05, 8231.88) * mm});
            skLineSegment(sketch, "E343", {"start": v(4151.05, 8231.88) * mm, "end": v(4175.43, 8231.75) * mm});
            skLineSegment(sketch, "E344", {"start": v(4175.43, 8231.75) * mm, "end": v(4199.82, 8231.6) * mm});
            skLineSegment(sketch, "E345", {"start": v(4199.82, 8231.6) * mm, "end": v(4224.22, 8231.4) * mm});
            skLineSegment(sketch, "E346", {"start": v(4224.22, 8231.4) * mm, "end": v(4248.63, 8231.2) * mm});
            skLineSegment(sketch, "E347", {"start": v(4248.63, 8231.2) * mm, "end": v(4273.04, 8230.97) * mm});
            skLineSegment(sketch, "E348", {"start": v(4273.04, 8230.97) * mm, "end": v(4297.46, 8230.73) * mm});
            skLineSegment(sketch, "E349", {"start": v(4297.46, 8230.73) * mm, "end": v(4321.9, 8230.48) * mm});
            skLineSegment(sketch, "E350", {"start": v(4321.9, 8230.48) * mm, "end": v(4346.32, 8230.2) * mm});
            skLineSegment(sketch, "E351", {"start": v(4346.32, 8230.2) * mm, "end": v(4370.76, 8229.93) * mm});
            skLineSegment(sketch, "E352", {"start": v(4370.76, 8229.93) * mm, "end": v(4395.2, 8229.65) * mm});
            skLineSegment(sketch, "E353", {"start": v(4395.2, 8229.65) * mm, "end": v(4419.65, 8229.37) * mm});
            skLineSegment(sketch, "E354", {"start": v(4419.65, 8229.37) * mm, "end": v(4444.1, 8229.09) * mm});
            skLineSegment(sketch, "E355", {"start": v(4444.1, 8229.09) * mm, "end": v(4468.55, 8228.81) * mm});
            skLineSegment(sketch, "E356", {"start": v(4468.55, 8228.81) * mm, "end": v(4493.01, 8228.54) * mm});
            skLineSegment(sketch, "E357", {"start": v(4493.01, 8228.54) * mm, "end": v(4517.47, 8228.27) * mm});
            skLineSegment(sketch, "E358", {"start": v(4517.47, 8228.27) * mm, "end": v(4541.93, 8228.02) * mm});
            skLineSegment(sketch, "E359", {"start": v(4541.93, 8228.02) * mm, "end": v(4566.4, 8227.77) * mm});
            skLineSegment(sketch, "E360", {"start": v(4566.4, 8227.77) * mm, "end": v(4590.86, 8227.53) * mm});
            skLineSegment(sketch, "E361", {"start": v(4590.86, 8227.53) * mm, "end": v(4615.33, 8227.3) * mm});
            skLineSegment(sketch, "E362", {"start": v(4615.33, 8227.3) * mm, "end": v(4639.8, 8227.09) * mm});
            skLineSegment(sketch, "E363", {"start": v(4639.8, 8227.09) * mm, "end": v(4664.27, 8226.88) * mm});
            skLineSegment(sketch, "E364", {"start": v(4664.27, 8226.88) * mm, "end": v(4688.74, 8226.69) * mm});
            skLineSegment(sketch, "E365", {"start": v(4688.74, 8226.69) * mm, "end": v(4713.22, 8226.51) * mm});
            skLineSegment(sketch, "E366", {"start": v(4713.22, 8226.51) * mm, "end": v(4737.7, 8226.35) * mm});
            skLineSegment(sketch, "E367", {"start": v(4737.7, 8226.35) * mm, "end": v(4762.17, 8226.2) * mm});
            skLineSegment(sketch, "E368", {"start": v(4762.17, 8226.2) * mm, "end": v(4786.64, 8226.07) * mm});
            skLineSegment(sketch, "E369", {"start": v(4786.64, 8226.07) * mm, "end": v(4811.12, 8225.95) * mm});
            skLineSegment(sketch, "E370", {"start": v(4811.12, 8225.95) * mm, "end": v(4835.6, 8225.85) * mm});
            skLineSegment(sketch, "E371", {"start": v(4835.6, 8225.85) * mm, "end": v(4860.07, 8225.76) * mm});
            skLineSegment(sketch, "E372", {"start": v(4860.07, 8225.76) * mm, "end": v(4884.55, 8225.68) * mm});
            skLineSegment(sketch, "E373", {"start": v(4884.55, 8225.68) * mm, "end": v(4909.03, 8225.62) * mm});
            skLineSegment(sketch, "E374", {"start": v(4909.03, 8225.62) * mm, "end": v(4933.5, 8225.57) * mm});
            skLineSegment(sketch, "E375", {"start": v(4933.5, 8225.57) * mm, "end": v(4957.98, 8225.53) * mm});
            skLineSegment(sketch, "E376", {"start": v(4957.98, 8225.53) * mm, "end": v(4982.46, 8225.51) * mm});
            skLineSegment(sketch, "E377", {"start": v(4982.46, 8225.51) * mm, "end": v(5006.94, 8225.5) * mm});
            skLineSegment(sketch, "E378", {"start": v(5006.94, 8225.5) * mm, "end": v(5031.42, 8225.52) * mm});
            skLineSegment(sketch, "E379", {"start": v(5031.42, 8225.52) * mm, "end": v(5055.9, 8225.55) * mm});
            skLineSegment(sketch, "E380", {"start": v(5055.9, 8225.55) * mm, "end": v(5080.37, 8225.6) * mm});
            skLineSegment(sketch, "E381", {"start": v(5080.37, 8225.6) * mm, "end": v(5104.85, 8225.66) * mm});
            skLineSegment(sketch, "E382", {"start": v(5104.85, 8225.66) * mm, "end": v(5129.33, 8225.73) * mm});
            skLineSegment(sketch, "E383", {"start": v(5129.33, 8225.73) * mm, "end": v(5153.8, 8225.82) * mm});
            skLineSegment(sketch, "E384", {"start": v(5153.8, 8225.82) * mm, "end": v(5178.28, 8225.91) * mm});
            skLineSegment(sketch, "E385", {"start": v(5178.28, 8225.91) * mm, "end": v(5202.75, 8226.02) * mm});
            skLineSegment(sketch, "E386", {"start": v(5202.75, 8226.02) * mm, "end": v(5227.23, 8226.15) * mm});
            skLineSegment(sketch, "E387", {"start": v(5227.23, 8226.15) * mm, "end": v(5251.7, 8226.29) * mm});
            skLineSegment(sketch, "E388", {"start": v(5251.7, 8226.29) * mm, "end": v(5276.18, 8226.44) * mm});
            skLineSegment(sketch, "E389", {"start": v(5276.18, 8226.44) * mm, "end": v(5300.65, 8226.6) * mm});
            skLineSegment(sketch, "E390", {"start": v(5300.65, 8226.6) * mm, "end": v(5325.13, 8226.8) * mm});
            skLineSegment(sketch, "E391", {"start": v(5325.13, 8226.8) * mm, "end": v(5349.6, 8226.99) * mm});
            skLineSegment(sketch, "E392", {"start": v(5349.6, 8226.99) * mm, "end": v(5374.07, 8227.2) * mm});
            skLineSegment(sketch, "E393", {"start": v(5374.07, 8227.2) * mm, "end": v(5398.53, 8227.42) * mm});
            skLineSegment(sketch, "E394", {"start": v(5398.53, 8227.42) * mm, "end": v(5423, 8227.65) * mm});
            skLineSegment(sketch, "E395", {"start": v(5423, 8227.65) * mm, "end": v(5447.46, 8227.88) * mm});
            skLineSegment(sketch, "E396", {"start": v(5447.46, 8227.88) * mm, "end": v(5471.92, 8228.13) * mm});
            skLineSegment(sketch, "E397", {"start": v(5471.92, 8228.13) * mm, "end": v(5496.39, 8228.39) * mm});
            skLineSegment(sketch, "E398", {"start": v(5496.39, 8228.39) * mm, "end": v(5520.84, 8228.65) * mm});
            skLineSegment(sketch, "E399", {"start": v(5520.84, 8228.65) * mm, "end": v(5545.3, 8228.91) * mm});
            skLineSegment(sketch, "E400", {"start": v(5545.3, 8228.91) * mm, "end": v(5569.75, 8229.18) * mm});
            skLineSegment(sketch, "E401", {"start": v(5569.75, 8229.18) * mm, "end": v(5594.28, 8229.46) * mm});
            skLineSegment(sketch, "E402", {"start": v(5594.28, 8229.46) * mm, "end": v(5619, 8229.74) * mm});
            skLineSegment(sketch, "E403", {"start": v(5619, 8229.74) * mm, "end": v(5643.74, 8230.02) * mm});
            skLineSegment(sketch, "E404", {"start": v(5643.74, 8230.02) * mm, "end": v(5668.46, 8230.29) * mm});
            skLineSegment(sketch, "E405", {"start": v(5668.46, 8230.29) * mm, "end": v(5693.18, 8230.55) * mm});
            skLineSegment(sketch, "E406", {"start": v(5693.18, 8230.55) * mm, "end": v(5717.89, 8230.8) * mm});
            skLineSegment(sketch, "E407", {"start": v(5717.89, 8230.8) * mm, "end": v(5742.6, 8231.03) * mm});
            skLineSegment(sketch, "E408", {"start": v(5742.6, 8231.03) * mm, "end": v(5767.3, 8231.25) * mm});
            skLineSegment(sketch, "E409", {"start": v(5767.3, 8231.25) * mm, "end": v(5791.98, 8231.44) * mm});
            skLineSegment(sketch, "E410", {"start": v(5791.98, 8231.44) * mm, "end": v(5816.66, 8231.62) * mm});
            skLineSegment(sketch, "E411", {"start": v(5816.66, 8231.62) * mm, "end": v(5841.34, 8231.76) * mm});
            skLineSegment(sketch, "E412", {"start": v(5841.34, 8231.76) * mm, "end": v(5866, 8231.87) * mm});
            skLineSegment(sketch, "E413", {"start": v(5866, 8231.87) * mm, "end": v(5890.66, 8231.94) * mm});
            skLineSegment(sketch, "E414", {"start": v(5890.66, 8231.94) * mm, "end": v(5915.31, 8231.96) * mm});
            skLineSegment(sketch, "E415", {"start": v(5915.31, 8231.96) * mm, "end": v(5939.95, 8231.93) * mm});
            skLineSegment(sketch, "E416", {"start": v(5939.95, 8231.93) * mm, "end": v(5964.58, 8231.84) * mm});
            skLineSegment(sketch, "E417", {"start": v(5964.58, 8231.84) * mm, "end": v(5989.2, 8231.7) * mm});
            skLineSegment(sketch, "E418", {"start": v(5989.2, 8231.7) * mm, "end": v(6013.82, 8231.48) * mm});
            skLineSegment(sketch, "E419", {"start": v(6013.82, 8231.48) * mm, "end": v(6038.42, 8231.2) * mm});
            skLineSegment(sketch, "E420", {"start": v(6038.42, 8231.2) * mm, "end": v(6063.01, 8230.83) * mm});
            skLineSegment(sketch, "E421", {"start": v(6063.01, 8230.83) * mm, "end": v(6087.6, 8230.38) * mm});
            skLineSegment(sketch, "E422", {"start": v(6087.6, 8230.38) * mm, "end": v(6112.16, 8229.84) * mm});
            skLineSegment(sketch, "E423", {"start": v(6112.16, 8229.84) * mm, "end": v(6136.72, 8229.2) * mm});
            skLineSegment(sketch, "E424", {"start": v(6136.72, 8229.2) * mm, "end": v(6161.26, 8228.45) * mm});
            skLineSegment(sketch, "E425", {"start": v(6161.26, 8228.45) * mm, "end": v(6185.79, 8227.59) * mm});
            skLineSegment(sketch, "E426", {"start": v(6185.79, 8227.59) * mm, "end": v(6210.3, 8226.61) * mm});
            skLineSegment(sketch, "E427", {"start": v(6210.3, 8226.61) * mm, "end": v(6234.8, 8225.52) * mm});
            skLineSegment(sketch, "E428", {"start": v(6234.8, 8225.52) * mm, "end": v(6259.3, 8224.29) * mm});
            skLineSegment(sketch, "E429", {"start": v(6259.3, 8224.29) * mm, "end": v(6283.77, 8222.92) * mm});
            skLineSegment(sketch, "E430", {"start": v(6283.77, 8222.92) * mm, "end": v(6308.23, 8221.42) * mm});
            skLineSegment(sketch, "E431", {"start": v(6308.23, 8221.42) * mm, "end": v(6332.67, 8219.78) * mm});
            skLineSegment(sketch, "E432", {"start": v(6332.67, 8219.78) * mm, "end": v(6357.27, 8217.98) * mm});
            skLineSegment(sketch, "E433", {"start": v(6357.27, 8217.98) * mm, "end": v(6382.47, 8215.98) * mm});
            skLineSegment(sketch, "E434", {"start": v(6382.47, 8215.98) * mm, "end": v(6407.66, 8213.8) * mm});
            skLineSegment(sketch, "E435", {"start": v(6407.66, 8213.8) * mm, "end": v(6432.82, 8211.45) * mm});
            skLineSegment(sketch, "E436", {"start": v(6432.82, 8211.45) * mm, "end": v(6457.97, 8208.91) * mm});
            skLineSegment(sketch, "E437", {"start": v(6457.97, 8208.91) * mm, "end": v(6483.08, 8206.18) * mm});
            skLineSegment(sketch, "E438", {"start": v(6483.08, 8206.18) * mm, "end": v(6508.18, 8203.27) * mm});
            skLineSegment(sketch, "E439", {"start": v(6508.18, 8203.27) * mm, "end": v(6533.25, 8200.16) * mm});
            skLineSegment(sketch, "E440", {"start": v(6533.25, 8200.16) * mm, "end": v(6534.71, 8211.59) * mm});
            skLineSegment(sketch, "E441", {"start": v(6534.71, 8211.59) * mm, "end": v(6536.17, 8222.97) * mm});
            skLineSegment(sketch, "E442", {"start": v(6536.17, 8222.97) * mm, "end": v(6537.62, 8234.33) * mm});
            skLineSegment(sketch, "E443", {"start": v(6537.62, 8234.33) * mm, "end": v(6539.08, 8245.7) * mm});
            skLineSegment(sketch, "E444", {"start": v(6539.08, 8245.7) * mm, "end": v(6540.54, 8257.13) * mm});
            skLineSegment(sketch, "E445", {"start": v(6540.54, 8257.13) * mm, "end": v(6542, 8268.51) * mm});
            skLineSegment(sketch, "E446", {"start": v(6542, 8268.51) * mm, "end": v(6543.46, 8279.87) * mm});
            skLineSegment(sketch, "E447", {"start": v(6543.46, 8279.87) * mm, "end": v(6544.9, 8291.25) * mm});
            skLineSegment(sketch, "E448", {"start": v(6544.9, 8291.25) * mm, "end": v(6519.23, 8294.43) * mm});
            skLineSegment(sketch, "E449", {"start": v(6590.38, 8909.88) * mm, "end": v(6599.59, 8973.4) * mm});
            skLineSegment(sketch, "E450", {"start": v(6599.59, 8973.4) * mm, "end": v(6608.48, 9035.46) * mm});
            skLineSegment(sketch, "E451", {"start": v(6608.48, 9035.46) * mm, "end": v(6616.8, 9096.04) * mm});
            skLineSegment(sketch, "E452", {"start": v(6616.8, 9096.04) * mm, "end": v(6625, 9158.81) * mm});
            skLineSegment(sketch, "E453", {"start": v(6625, 9158.81) * mm, "end": v(6632.56, 9221.72) * mm});
            skLineSegment(sketch, "E454", {"start": v(6632.56, 9221.72) * mm, "end": v(6639.26, 9284.76) * mm});
            skLineSegment(sketch, "E455", {"start": v(6639.26, 9284.76) * mm, "end": v(6644.98, 9347.86) * mm});
            skLineSegment(sketch, "E456", {"start": v(6644.98, 9347.86) * mm, "end": v(6649.79, 9412.57) * mm});
            skLineSegment(sketch, "E457", {"start": v(6649.79, 9412.57) * mm, "end": v(6653.36, 9476.26) * mm});
            skLineSegment(sketch, "E458", {"start": v(6653.36, 9476.26) * mm, "end": v(6655.73, 9539.38) * mm});
            skLineSegment(sketch, "E459", {"start": v(6655.73, 9539.38) * mm, "end": v(6656.93, 9601.13) * mm});
            skLineSegment(sketch, "E460", {"start": v(6656.93, 9601.13) * mm, "end": v(6657.01, 9663.96) * mm});
            skLineSegment(sketch, "E461", {"start": v(6657.01, 9663.96) * mm, "end": v(6655.96, 9728.54) * mm});
            skLineSegment(sketch, "E462", {"start": v(6655.96, 9728.54) * mm, "end": v(6653.75, 9794.97) * mm});
            skLineSegment(sketch, "E463", {"start": v(6653.75, 9794.97) * mm, "end": v(6650.99, 9858.48) * mm});
            skLineSegment(sketch, "E464", {"start": v(6650.99, 9858.48) * mm, "end": v(6647.65, 9921.7) * mm});
            skLineSegment(sketch, "E465", {"start": v(6647.65, 9921.7) * mm, "end": v(6644.1, 9983.44) * mm});
            skLineSegment(sketch, "E466", {"start": v(6644.1, 9983.44) * mm, "end": v(6640.26, 10046.74) * mm});
            skLineSegment(sketch, "E467", {"start": v(6640.26, 10046.74) * mm, "end": v(6636.59, 10110.05) * mm});
            skLineSegment(sketch, "E468", {"start": v(6636.59, 10110.05) * mm, "end": v(6572.65, 10110.82) * mm});
            skLineSegment(sketch, "E469", {"start": v(6572.65, 10110.82) * mm, "end": v(6508.56, 10112.35) * mm});
            skLineSegment(sketch, "E470", {"start": v(6508.56, 10112.35) * mm, "end": v(6444.42, 10114.41) * mm});
            skLineSegment(sketch, "E471", {"start": v(6444.42, 10114.41) * mm, "end": v(6382.08, 10116.6) * mm});
            skLineSegment(sketch, "E472", {"start": v(6382.08, 10116.6) * mm, "end": v(6319.6, 10119.03) * mm});
            skLineSegment(sketch, "E473", {"start": v(6319.6, 10119.03) * mm, "end": v(6256.96, 10121.57) * mm});
            skLineSegment(sketch, "E474", {"start": v(6256.96, 10121.57) * mm, "end": v(6194.22, 10124.13) * mm});
            skLineSegment(sketch, "E475", {"start": v(6194.22, 10124.13) * mm, "end": v(6131.36, 10126.66) * mm});
            skLineSegment(sketch, "E476", {"start": v(6131.36, 10126.66) * mm, "end": v(6068.4, 10129.12) * mm});
            skLineSegment(sketch, "E477", {"start": v(6068.4, 10129.12) * mm, "end": v(6005.36, 10131.47) * mm});
            skLineSegment(sketch, "E478", {"start": v(6005.36, 10131.47) * mm, "end": v(5942.22, 10133.66) * mm});
            skLineSegment(sketch, "E479", {"start": v(5942.22, 10133.66) * mm, "end": v(5879.04, 10135.7) * mm});
            skLineSegment(sketch, "E480", {"start": v(5879.04, 10135.7) * mm, "end": v(5815.78, 10137.58) * mm});
            skLineSegment(sketch, "E481", {"start": v(5815.78, 10137.58) * mm, "end": v(5752.46, 10139.35) * mm});
            skLineSegment(sketch, "E482", {"start": v(5752.46, 10139.35) * mm, "end": v(5689.1, 10140.97) * mm});
            skLineSegment(sketch, "E483", {"start": v(5689.1, 10140.97) * mm, "end": v(5626, 10142.43) * mm});
            skLineSegment(sketch, "E484", {"start": v(5626, 10142.43) * mm, "end": v(5563.33, 10143.73) * mm});
            skLineSegment(sketch, "E485", {"start": v(5563.33, 10143.73) * mm, "end": v(5500.62, 10144.9) * mm});
            skLineSegment(sketch, "E486", {"start": v(5500.62, 10144.9) * mm, "end": v(5437.89, 10145.9) * mm});
            skLineSegment(sketch, "E487", {"start": v(5437.89, 10145.9) * mm, "end": v(5375.15, 10146.77) * mm});
            skLineSegment(sketch, "E488", {"start": v(5375.15, 10146.77) * mm, "end": v(5312.39, 10147.5) * mm});
            skLineSegment(sketch, "E489", {"start": v(5312.39, 10147.5) * mm, "end": v(5249.6, 10148.07) * mm});
            skLineSegment(sketch, "E490", {"start": v(5249.6, 10148.07) * mm, "end": v(5186.84, 10148.5) * mm});
            skLineSegment(sketch, "E491", {"start": v(5186.84, 10148.5) * mm, "end": v(5124.04, 10148.78) * mm});
            skLineSegment(sketch, "E492", {"start": v(5124.04, 10148.78) * mm, "end": v(5061.25, 10148.9) * mm});
            skLineSegment(sketch, "E493", {"start": v(5061.25, 10148.9) * mm, "end": v(4998.46, 10148.9) * mm});
            skLineSegment(sketch, "E494", {"start": v(4998.46, 10148.9) * mm, "end": v(4935.66, 10148.75) * mm});
            skLineSegment(sketch, "E495", {"start": v(4935.66, 10148.75) * mm, "end": v(4872.88, 10148.45) * mm});
            skLineSegment(sketch, "E496", {"start": v(4872.88, 10148.45) * mm, "end": v(4810.1, 10148) * mm});
            skLineSegment(sketch, "E497", {"start": v(4810.1, 10148) * mm, "end": v(4747.32, 10147.4) * mm});
            skLineSegment(sketch, "E498", {"start": v(4747.32, 10147.4) * mm, "end": v(4684.56, 10146.64) * mm});
            skLineSegment(sketch, "E499", {"start": v(4684.56, 10146.64) * mm, "end": v(4621.81, 10145.75) * mm});
            skLineSegment(sketch, "E500", {"start": v(4621.81, 10145.75) * mm, "end": v(4559.08, 10144.7) * mm});
            skLineSegment(sketch, "E501", {"start": v(4559.08, 10144.7) * mm, "end": v(4496.38, 10143.5) * mm});
            skLineSegment(sketch, "E502", {"start": v(4496.38, 10143.5) * mm, "end": v(4433.69, 10142.15) * mm});
            skLineSegment(sketch, "E503", {"start": v(4433.69, 10142.15) * mm, "end": v(4371.06, 10140.66) * mm});
            skLineSegment(sketch, "E504", {"start": v(4371.06, 10140.66) * mm, "end": v(4308.45, 10139.03) * mm});
            skLineSegment(sketch, "E505", {"start": v(4308.45, 10139.03) * mm, "end": v(4245.88, 10137.26) * mm});
            skLineSegment(sketch, "E506", {"start": v(4245.88, 10137.26) * mm, "end": v(4183.38, 10135.36) * mm});
            skLineSegment(sketch, "E507", {"start": v(4183.38, 10135.36) * mm, "end": v(4120.93, 10133.33) * mm});
            skLineSegment(sketch, "E508", {"start": v(4120.93, 10133.33) * mm, "end": v(4058.55, 10131.14) * mm});
            skLineSegment(sketch, "E509", {"start": v(4058.55, 10131.14) * mm, "end": v(3996.25, 10128.8) * mm});
            skLineSegment(sketch, "E510", {"start": v(3996.25, 10128.8) * mm, "end": v(3934.04, 10126.34) * mm});
            skLineSegment(sketch, "E511", {"start": v(3934.04, 10126.34) * mm, "end": v(3871.94, 10123.84) * mm});
            skLineSegment(sketch, "E512", {"start": v(3871.94, 10123.84) * mm, "end": v(3809.94, 10121.3) * mm});
            skLineSegment(sketch, "E513", {"start": v(3809.94, 10121.3) * mm, "end": v(3748.04, 10118.79) * mm});
            skLineSegment(sketch, "E514", {"start": v(3748.04, 10118.79) * mm, "end": v(3686.3, 10116.4) * mm});
            skLineSegment(sketch, "E515", {"start": v(3686.3, 10116.4) * mm, "end": v(3624.7, 10114.25) * mm});
            skLineSegment(sketch, "E516", {"start": v(3624.7, 10114.25) * mm, "end": v(3563.22, 10112.42) * mm});
            skLineSegment(sketch, "E517", {"start": v(3563.22, 10112.42) * mm, "end": v(3501.9, 10111.1) * mm});
            skLineSegment(sketch, "E518", {"start": v(3501.9, 10111.1) * mm, "end": v(3440.72, 10110.51) * mm});
            skLineSegment(sketch, "E519", {"start": v(3440.72, 10110.51) * mm, "end": v(3437.05, 10047.2) * mm});
            skLineSegment(sketch, "E520", {"start": v(3437.05, 10047.2) * mm, "end": v(3433.22, 9983.9) * mm});
            skLineSegment(sketch, "E521", {"start": v(3433.22, 9983.9) * mm, "end": v(3429.68, 9922.16) * mm});
            skLineSegment(sketch, "E522", {"start": v(3429.68, 9922.16) * mm, "end": v(3426.35, 9858.93) * mm});
            skLineSegment(sketch, "E523", {"start": v(3426.35, 9858.93) * mm, "end": v(3423.6, 9795.41) * mm});
            skLineSegment(sketch, "E524", {"start": v(3423.6, 9795.41) * mm, "end": v(3421.39, 9728.97) * mm});
            skLineSegment(sketch, "E525", {"start": v(3421.39, 9728.97) * mm, "end": v(3420.33, 9664.38) * mm});
            skLineSegment(sketch, "E526", {"start": v(3420.33, 9664.38) * mm, "end": v(3420.41, 9601.53) * mm});
            skLineSegment(sketch, "E527", {"start": v(3420.41, 9601.53) * mm, "end": v(3421.6, 9539.76) * mm});
            skLineSegment(sketch, "E528", {"start": v(3421.6, 9539.76) * mm, "end": v(3423.96, 9476.63) * mm});
            skLineSegment(sketch, "E529", {"start": v(3423.96, 9476.63) * mm, "end": v(3427.51, 9412.91) * mm});
            skLineSegment(sketch, "E530", {"start": v(3427.51, 9412.91) * mm, "end": v(3432.3, 9348.18) * mm});
            skLineSegment(sketch, "E531", {"start": v(3432.3, 9348.18) * mm, "end": v(3438, 9285.07) * mm});
            skLineSegment(sketch, "E532", {"start": v(3438, 9285.07) * mm, "end": v(3444.67, 9222.01) * mm});
            skLineSegment(sketch, "E533", {"start": v(3444.67, 9222.01) * mm, "end": v(3452.2, 9159.08) * mm});
            skLineSegment(sketch, "E534", {"start": v(3452.2, 9159.08) * mm, "end": v(3460.37, 9096.3) * mm});
            skLineSegment(sketch, "E535", {"start": v(3460.37, 9096.3) * mm, "end": v(3468.65, 9035.72) * mm});
            skLineSegment(sketch, "E536", {"start": v(3468.65, 9035.72) * mm, "end": v(3477.5, 8973.65) * mm});
            skLineSegment(sketch, "E537", {"start": v(3477.5, 8973.65) * mm, "end": v(3486.68, 8910.12) * mm});
            skLineSegment(sketch, "E538", {"start": v(3486.68, 8910.12) * mm, "end": v(3496, 8845.1) * mm});
            skLineSegment(sketch, "E539", {"start": v(3496, 8845.1) * mm, "end": v(3554.92, 8849.86) * mm});
            skLineSegment(sketch, "E540", {"start": v(3554.92, 8849.86) * mm, "end": v(3614.03, 8853.72) * mm});
            skLineSegment(sketch, "E541", {"start": v(3614.03, 8853.72) * mm, "end": v(3673.31, 8856.87) * mm});
            skLineSegment(sketch, "E542", {"start": v(3673.31, 8856.87) * mm, "end": v(3732.76, 8859.43) * mm});
            skLineSegment(sketch, "E543", {"start": v(3732.76, 8859.43) * mm, "end": v(3792.34, 8861.5) * mm});
            skLineSegment(sketch, "E544", {"start": v(3792.34, 8861.5) * mm, "end": v(3852.05, 8863.2) * mm});
            skLineSegment(sketch, "E545", {"start": v(3852.05, 8863.2) * mm, "end": v(3911.9, 8864.6) * mm});
            skLineSegment(sketch, "E546", {"start": v(3911.9, 8864.6) * mm, "end": v(3971.85, 8865.77) * mm});
            skLineSegment(sketch, "E547", {"start": v(3971.85, 8865.77) * mm, "end": v(4031.88, 8866.76) * mm});
            skLineSegment(sketch, "E548", {"start": v(4031.88, 8866.76) * mm, "end": v(4092.03, 8867.61) * mm});
            skLineSegment(sketch, "E549", {"start": v(4092.03, 8867.61) * mm, "end": v(4152.25, 8868.36) * mm});
            skLineSegment(sketch, "E550", {"start": v(4152.25, 8868.36) * mm, "end": v(4212.52, 8869.02) * mm});
            skLineSegment(sketch, "E551", {"start": v(4212.52, 8869.02) * mm, "end": v(4272.87, 8869.6) * mm});
            skLineSegment(sketch, "E552", {"start": v(4272.87, 8869.6) * mm, "end": v(4333.27, 8870.08) * mm});
            skLineSegment(sketch, "E553", {"start": v(4333.27, 8870.08) * mm, "end": v(4393.71, 8870.5) * mm});
            skLineSegment(sketch, "E554", {"start": v(4393.71, 8870.5) * mm, "end": v(4454.2, 8870.88) * mm});
            skLineSegment(sketch, "E555", {"start": v(4454.2, 8870.88) * mm, "end": v(4514.71, 8871.19) * mm});
            skLineSegment(sketch, "E556", {"start": v(4514.71, 8871.19) * mm, "end": v(4575.26, 8871.42) * mm});
            skLineSegment(sketch, "E557", {"start": v(4575.26, 8871.42) * mm, "end": v(4635.84, 8871.6) * mm});
            skLineSegment(sketch, "E558", {"start": v(4635.84, 8871.6) * mm, "end": v(4696.44, 8871.74) * mm});
            skLineSegment(sketch, "E559", {"start": v(4696.44, 8871.74) * mm, "end": v(4757.07, 8871.83) * mm});
            skLineSegment(sketch, "E560", {"start": v(4757.07, 8871.83) * mm, "end": v(4817.7, 8871.9) * mm});
            skLineSegment(sketch, "E561", {"start": v(4817.7, 8871.9) * mm, "end": v(4878.35, 8871.97) * mm});
            skLineSegment(sketch, "E562", {"start": v(4878.35, 8871.97) * mm, "end": v(4939.02, 8872) * mm});
            skLineSegment(sketch, "E563", {"start": v(4939.02, 8872) * mm, "end": v(4999.68, 8872.02) * mm});
            skLineSegment(sketch, "E564", {"start": v(4999.68, 8872.02) * mm, "end": v(5060.35, 8872.01) * mm});
            skLineSegment(sketch, "E565", {"start": v(5060.35, 8872.01) * mm, "end": v(5121.01, 8872) * mm});
            skLineSegment(sketch, "E566", {"start": v(5121.01, 8872) * mm, "end": v(5181.67, 8871.97) * mm});
            skLineSegment(sketch, "E567", {"start": v(5181.67, 8871.97) * mm, "end": v(5242.32, 8871.9) * mm});
            skLineSegment(sketch, "E568", {"start": v(5242.32, 8871.9) * mm, "end": v(5302.96, 8871.83) * mm});
            skLineSegment(sketch, "E569", {"start": v(5302.96, 8871.83) * mm, "end": v(5363.58, 8871.73) * mm});
            skLineSegment(sketch, "E570", {"start": v(5363.58, 8871.73) * mm, "end": v(5424.19, 8871.6) * mm});
            skLineSegment(sketch, "E571", {"start": v(5424.19, 8871.6) * mm, "end": v(5484.77, 8871.4) * mm});
            skLineSegment(sketch, "E572", {"start": v(5484.77, 8871.4) * mm, "end": v(5545.31, 8871.17) * mm});
            skLineSegment(sketch, "E573", {"start": v(5545.31, 8871.17) * mm, "end": v(5605.84, 8870.86) * mm});
            skLineSegment(sketch, "E574", {"start": v(5605.84, 8870.86) * mm, "end": v(5666.77, 8870.48) * mm});
            skLineSegment(sketch, "E575", {"start": v(5666.77, 8870.48) * mm, "end": v(5727.93, 8870.04) * mm});
            skLineSegment(sketch, "E576", {"start": v(5727.93, 8870.04) * mm, "end": v(5789.06, 8869.54) * mm});
            skLineSegment(sketch, "E577", {"start": v(5789.06, 8869.54) * mm, "end": v(5850.12, 8868.97) * mm});
            skLineSegment(sketch, "E578", {"start": v(5850.12, 8868.97) * mm, "end": v(5911.13, 8868.3) * mm});
            skLineSegment(sketch, "E579", {"start": v(5911.13, 8868.3) * mm, "end": v(5972.07, 8867.55) * mm});
            skLineSegment(sketch, "E580", {"start": v(5972.07, 8867.55) * mm, "end": v(6032.93, 8866.7) * mm});
            skLineSegment(sketch, "E581", {"start": v(6032.93, 8866.7) * mm, "end": v(6093.7, 8865.7) * mm});
            skLineSegment(sketch, "E582", {"start": v(6093.7, 8865.7) * mm, "end": v(6154.36, 8864.52) * mm});
            skLineSegment(sketch, "E583", {"start": v(6154.36, 8864.52) * mm, "end": v(6214.94, 8863.12) * mm});
            skLineSegment(sketch, "E584", {"start": v(6214.94, 8863.12) * mm, "end": v(6275.37, 8861.43) * mm});
            skLineSegment(sketch, "E585", {"start": v(6275.37, 8861.43) * mm, "end": v(6335.67, 8859.35) * mm});
            skLineSegment(sketch, "E586", {"start": v(6335.67, 8859.35) * mm, "end": v(6395.82, 8856.79) * mm});
            skLineSegment(sketch, "E587", {"start": v(6395.82, 8856.79) * mm, "end": v(6457.7, 8853.64) * mm});
            skLineSegment(sketch, "E588", {"start": v(6457.7, 8853.64) * mm, "end": v(6519.47, 8849.73) * mm});
            skLineSegment(sketch, "E589", {"start": v(6519.47, 8849.73) * mm, "end": v(6581.04, 8844.87) * mm});
            skLineSegment(sketch, "E590", {"start": v(6581.04, 8844.87) * mm, "end": v(6590.38, 8909.88) * mm});
            skLineSegment(sketch, "E591", {"start": v(6494.4, 7419.7) * mm, "end": v(6411.13, 7460.06) * mm});
            skLineSegment(sketch, "E592", {"start": v(6411.13, 7460.06) * mm, "end": v(6332.75, 7495.39) * mm});
            skLineSegment(sketch, "E593", {"start": v(6332.75, 7495.39) * mm, "end": v(6251.7, 7529.35) * mm});
            skLineSegment(sketch, "E594", {"start": v(6251.7, 7529.35) * mm, "end": v(6169.67, 7561.06) * mm});
            skLineSegment(sketch, "E595", {"start": v(6169.67, 7561.06) * mm, "end": v(6086.74, 7590.48) * mm});
            skLineSegment(sketch, "E596", {"start": v(6086.74, 7590.48) * mm, "end": v(6002.96, 7617.53) * mm});
            skLineSegment(sketch, "E597", {"start": v(6002.96, 7617.53) * mm, "end": v(5918.41, 7642.18) * mm});
            skLineSegment(sketch, "E598", {"start": v(5918.41, 7642.18) * mm, "end": v(5833.15, 7664.4) * mm});
            skLineSegment(sketch, "E599", {"start": v(5833.15, 7664.4) * mm, "end": v(5747.26, 7684.18) * mm});
            skLineSegment(sketch, "E600", {"start": v(5747.26, 7684.18) * mm, "end": v(5661.1, 7701.4) * mm});
            skLineSegment(sketch, "E601", {"start": v(5661.1, 7701.4) * mm, "end": v(5575.18, 7716.04) * mm});
            skLineSegment(sketch, "E602", {"start": v(5575.18, 7716.04) * mm, "end": v(5488.86, 7728.2) * mm});
            skLineSegment(sketch, "E603", {"start": v(5488.86, 7728.2) * mm, "end": v(5402.21, 7737.9) * mm});
            skLineSegment(sketch, "E604", {"start": v(5402.21, 7737.9) * mm, "end": v(5315.32, 7745.11) * mm});
            skLineSegment(sketch, "E605", {"start": v(5315.32, 7745.11) * mm, "end": v(5228.25, 7749.84) * mm});
            skLineSegment(sketch, "E606", {"start": v(5228.25, 7749.84) * mm, "end": v(5141.07, 7752.06) * mm});
            skLineSegment(sketch, "E607", {"start": v(5141.07, 7752.06) * mm, "end": v(5053.86, 7751.8) * mm});
            skLineSegment(sketch, "E608", {"start": v(5053.86, 7751.8) * mm, "end": v(4966.7, 7749.04) * mm});
            skLineSegment(sketch, "E609", {"start": v(4966.7, 7749.04) * mm, "end": v(4879.66, 7743.78) * mm});
            skLineSegment(sketch, "E610", {"start": v(4879.66, 7743.78) * mm, "end": v(4792.81, 7736.04) * mm});
            skLineSegment(sketch, "E611", {"start": v(4792.81, 7736.04) * mm, "end": v(4706.23, 7725.8) * mm});
            skLineSegment(sketch, "E612", {"start": v(4706.23, 7725.8) * mm, "end": v(4619.99, 7713.11) * mm});
            skLineSegment(sketch, "E613", {"start": v(4619.99, 7713.11) * mm, "end": v(4534.16, 7697.96) * mm});
            skLineSegment(sketch, "E614", {"start": v(4534.16, 7697.96) * mm, "end": v(4448.83, 7680.36) * mm});
            skLineSegment(sketch, "E615", {"start": v(4448.83, 7680.36) * mm, "end": v(4364.05, 7660.34) * mm});
            skLineSegment(sketch, "E616", {"start": v(4364.05, 7660.34) * mm, "end": v(4279.9, 7637.93) * mm});
            skLineSegment(sketch, "E617", {"start": v(4279.9, 7637.93) * mm, "end": v(4196.46, 7613.14) * mm});
            skLineSegment(sketch, "E618", {"start": v(4196.46, 7613.14) * mm, "end": v(4113.79, 7586.02) * mm});
            skLineSegment(sketch, "E619", {"start": v(4113.79, 7586.02) * mm, "end": v(4031.95, 7556.6) * mm});
            skLineSegment(sketch, "E620", {"start": v(4031.95, 7556.6) * mm, "end": v(3951, 7524.93) * mm});
            skLineSegment(sketch, "E621", {"start": v(3951, 7524.93) * mm, "end": v(3871.02, 7491.07) * mm});
            skLineSegment(sketch, "E622", {"start": v(3871.02, 7491.07) * mm, "end": v(3792.02, 7455.1) * mm});
            skLineSegment(sketch, "E623", {"start": v(3792.02, 7455.1) * mm, "end": v(3714.05, 7417.12) * mm});
            skLineSegment(sketch, "E624", {"start": v(3714.05, 7417.12) * mm, "end": v(3637.1, 7377.24) * mm});
            skLineSegment(sketch, "E625", {"start": v(3637.1, 7377.24) * mm, "end": v(3677.34, 7298.95) * mm});
            skLineSegment(sketch, "E626", {"start": v(3677.34, 7298.95) * mm, "end": v(3717.53, 7221.35) * mm});
            skLineSegment(sketch, "E627", {"start": v(3717.53, 7221.35) * mm, "end": v(3758.79, 7142.38) * mm});
            skLineSegment(sketch, "E628", {"start": v(3758.79, 7142.38) * mm, "end": v(3801.1, 7062.25) * mm});
            skLineSegment(sketch, "E629", {"start": v(3801.1, 7062.25) * mm, "end": v(3843.37, 6983.07) * mm});
            skLineSegment(sketch, "E630", {"start": v(3843.37, 6983.07) * mm, "end": v(3886.36, 6903.43) * mm});
            skLineSegment(sketch, "E631", {"start": v(3886.36, 6903.43) * mm, "end": v(3929.8, 6823.78) * mm});
            skLineSegment(sketch, "E632", {"start": v(3929.8, 6823.78) * mm, "end": v(3973.49, 6744.44) * mm});
            skLineSegment(sketch, "E633", {"start": v(3973.49, 6744.44) * mm, "end": v(4017.2, 6665.7) * mm});
            skLineSegment(sketch, "E634", {"start": v(4017.2, 6665.7) * mm, "end": v(4060.75, 6587.87) * mm});
            skLineSegment(sketch, "E635", {"start": v(4060.75, 6587.87) * mm, "end": v(4103.9, 6511.18) * mm});
            skLineSegment(sketch, "E636", {"start": v(4103.9, 6511.18) * mm, "end": v(4146.43, 6435.86) * mm});
            skLineSegment(sketch, "E637", {"start": v(4146.43, 6435.86) * mm, "end": v(4188.17, 6362.11) * mm});
            skLineSegment(sketch, "E638", {"start": v(4188.17, 6362.11) * mm, "end": v(4231.58, 6285.64) * mm});
            skLineSegment(sketch, "E639", {"start": v(4231.58, 6285.64) * mm, "end": v(4274.47, 6210.19) * mm});
            skLineSegment(sketch, "E640", {"start": v(4274.47, 6210.19) * mm, "end": v(4317.99, 6133.68) * mm});
            skLineSegment(sketch, "E641", {"start": v(4317.99, 6133.68) * mm, "end": v(4362.04, 6056.13) * mm});
            skLineSegment(sketch, "E642", {"start": v(4362.04, 6056.13) * mm, "end": v(4406.37, 5977.75) * mm});
            skLineSegment(sketch, "E643", {"start": v(4406.37, 5977.75) * mm, "end": v(4451.73, 5897) * mm});
            skLineSegment(sketch, "E644", {"start": v(4451.73, 5897) * mm, "end": v(4494.51, 5819.73) * mm});
            skLineSegment(sketch, "E645", {"start": v(4494.51, 5819.73) * mm, "end": v(4536.74, 5742.22) * mm});
            skLineSegment(sketch, "E646", {"start": v(4536.74, 5742.22) * mm, "end": v(4578.25, 5664.38) * mm});
            skLineSegment(sketch, "E647", {"start": v(4578.25, 5664.38) * mm, "end": v(4618.85, 5586.13) * mm});
            skLineSegment(sketch, "E648", {"start": v(4618.85, 5586.13) * mm, "end": v(4658.35, 5507.36) * mm});
            skLineSegment(sketch, "E649", {"start": v(4658.35, 5507.36) * mm, "end": v(4697.98, 5424.49) * mm});
            skLineSegment(sketch, "E650", {"start": v(4697.98, 5424.49) * mm, "end": v(4735.11, 5342.73) * mm});
            skLineSegment(sketch, "E651", {"start": v(4735.11, 5342.73) * mm, "end": v(4769.5, 5262.25) * mm});
            skLineSegment(sketch, "E652", {"start": v(4769.5, 5262.25) * mm, "end": v(4801.03, 5183.22) * mm});
            skLineSegment(sketch, "E653", {"start": v(4801.03, 5183.22) * mm, "end": v(4829.89, 5105.82) * mm});
            skLineSegment(sketch, "E654", {"start": v(4829.89, 5105.82) * mm, "end": v(4844.83, 5112.73) * mm});
            skLineSegment(sketch, "E655", {"start": v(4844.83, 5112.73) * mm, "end": v(4859.77, 5119.67) * mm});
            skLineSegment(sketch, "E656", {"start": v(4859.77, 5119.67) * mm, "end": v(4874.76, 5126.46) * mm});
            skLineSegment(sketch, "E657", {"start": v(4874.76, 5126.46) * mm, "end": v(4889.86, 5133.02) * mm});
            skLineSegment(sketch, "E658", {"start": v(4889.86, 5133.02) * mm, "end": v(4905.08, 5139.29) * mm});
            skLineSegment(sketch, "E659", {"start": v(4905.08, 5139.29) * mm, "end": v(4920.43, 5145.2) * mm});
            skLineSegment(sketch, "E660", {"start": v(4920.43, 5145.2) * mm, "end": v(4935.92, 5150.73) * mm});
            skLineSegment(sketch, "E661", {"start": v(4935.92, 5150.73) * mm, "end": v(4951.54, 5155.84) * mm});
            skLineSegment(sketch, "E662", {"start": v(4951.54, 5155.84) * mm, "end": v(4967.3, 5160.5) * mm});
            skLineSegment(sketch, "E663", {"start": v(4967.3, 5160.5) * mm, "end": v(4983.2, 5164.69) * mm});
            skLineSegment(sketch, "E664", {"start": v(4983.2, 5164.69) * mm, "end": v(4999.2, 5168.4) * mm});
            skLineSegment(sketch, "E665", {"start": v(4999.2, 5168.4) * mm, "end": v(5015.3, 5171.6) * mm});
            skLineSegment(sketch, "E666", {"start": v(5015.3, 5171.6) * mm, "end": v(5031.5, 5174.3) * mm});
            skLineSegment(sketch, "E667", {"start": v(5031.5, 5174.3) * mm, "end": v(5047.78, 5176.48) * mm});
            skLineSegment(sketch, "E668", {"start": v(5047.78, 5176.48) * mm, "end": v(5064.1, 5178.13) * mm});
            skLineSegment(sketch, "E669", {"start": v(5064.1, 5178.13) * mm, "end": v(5080.49, 5179.25) * mm});
            skLineSegment(sketch, "E670", {"start": v(5080.49, 5179.25) * mm, "end": v(5096.89, 5179.84) * mm});
            skLineSegment(sketch, "E671", {"start": v(5096.89, 5179.84) * mm, "end": v(5113.3, 5179.9) * mm});
            skLineSegment(sketch, "E672", {"start": v(5113.3, 5179.9) * mm, "end": v(5129.7, 5179.41) * mm});
            skLineSegment(sketch, "E673", {"start": v(5129.7, 5179.41) * mm, "end": v(5146.09, 5178.4) * mm});
            skLineSegment(sketch, "E674", {"start": v(5146.09, 5178.4) * mm, "end": v(5162.43, 5176.85) * mm});
            skLineSegment(sketch, "E675", {"start": v(5162.43, 5176.85) * mm, "end": v(5178.72, 5174.78) * mm});
            skLineSegment(sketch, "E676", {"start": v(5178.72, 5174.78) * mm, "end": v(5194.93, 5172.19) * mm});
            skLineSegment(sketch, "E677", {"start": v(5194.93, 5172.19) * mm, "end": v(5211.06, 5169.08) * mm});
            skLineSegment(sketch, "E678", {"start": v(5211.06, 5169.08) * mm, "end": v(5227.22, 5165.45) * mm});
            skLineSegment(sketch, "E679", {"start": v(5227.22, 5165.45) * mm, "end": v(5243.32, 5161.3) * mm});
            skLineSegment(sketch, "E680", {"start": v(5243.32, 5161.3) * mm, "end": v(5259.3, 5156.68) * mm});
            skLineSegment(sketch, "E681", {"start": v(5259.3, 5156.68) * mm, "end": v(5275.13, 5151.6) * mm});
            skLineSegment(sketch, "E682", {"start": v(5275.13, 5151.6) * mm, "end": v(5290.82, 5146.08) * mm});
            skLineSegment(sketch, "E683", {"start": v(5290.82, 5146.08) * mm, "end": v(5306.38, 5140.16) * mm});
            skLineSegment(sketch, "E684", {"start": v(5306.38, 5140.16) * mm, "end": v(5321.8, 5133.88) * mm});
            skLineSegment(sketch, "E685", {"start": v(5321.8, 5133.88) * mm, "end": v(5337.09, 5127.28) * mm});
            skLineSegment(sketch, "E686", {"start": v(5337.09, 5127.28) * mm, "end": v(5351.95, 5120.58) * mm});
            skLineSegment(sketch, "E687", {"start": v(5351.95, 5120.58) * mm, "end": v(5367.91, 5113.25) * mm});
            skLineSegment(sketch, "E688", {"start": v(5367.91, 5113.25) * mm, "end": v(5383.54, 5106.04) * mm});
            skLineSegment(sketch, "E689", {"start": v(5383.54, 5106.04) * mm, "end": v(5412.35, 5183.46) * mm});
            skLineSegment(sketch, "E690", {"start": v(5412.35, 5183.46) * mm, "end": v(5443.84, 5262.5) * mm});
            skLineSegment(sketch, "E691", {"start": v(5443.84, 5262.5) * mm, "end": v(5478.17, 5343) * mm});
            skLineSegment(sketch, "E692", {"start": v(5478.17, 5343) * mm, "end": v(5515.24, 5424.77) * mm});
            skLineSegment(sketch, "E693", {"start": v(5515.24, 5424.77) * mm, "end": v(5554.8, 5507.65) * mm});
            skLineSegment(sketch, "E694", {"start": v(5554.8, 5507.65) * mm, "end": v(5594.25, 5586.44) * mm});
            skLineSegment(sketch, "E695", {"start": v(5594.25, 5586.44) * mm, "end": v(5634.8, 5664.7) * mm});
            skLineSegment(sketch, "E696", {"start": v(5634.8, 5664.7) * mm, "end": v(5676.24, 5742.56) * mm});
            skLineSegment(sketch, "E697", {"start": v(5676.24, 5742.56) * mm, "end": v(5718.42, 5820.1) * mm});
            skLineSegment(sketch, "E698", {"start": v(5718.42, 5820.1) * mm, "end": v(5761.15, 5897.39) * mm});
            skLineSegment(sketch, "E699", {"start": v(5761.15, 5897.39) * mm, "end": v(5806.45, 5978.16) * mm});
            skLineSegment(sketch, "E700", {"start": v(5806.45, 5978.16) * mm, "end": v(5850.73, 6056.57) * mm});
            skLineSegment(sketch, "E701", {"start": v(5850.73, 6056.57) * mm, "end": v(5894.73, 6134.15) * mm});
            skLineSegment(sketch, "E702", {"start": v(5894.73, 6134.15) * mm, "end": v(5938.2, 6210.68) * mm});
            skLineSegment(sketch, "E703", {"start": v(5938.2, 6210.68) * mm, "end": v(5981.04, 6286.15) * mm});
            skLineSegment(sketch, "E704", {"start": v(5981.04, 6286.15) * mm, "end": v(6024.4, 6362.66) * mm});
            skLineSegment(sketch, "E705", {"start": v(6024.4, 6362.66) * mm, "end": v(6066.1, 6436.43) * mm});
            skLineSegment(sketch, "E706", {"start": v(6066.1, 6436.43) * mm, "end": v(6108.6, 6511.78) * mm});
            skLineSegment(sketch, "E707", {"start": v(6108.6, 6511.78) * mm, "end": v(6151.7, 6588.5) * mm});
            skLineSegment(sketch, "E708", {"start": v(6151.7, 6588.5) * mm, "end": v(6195.19, 6666.35) * mm});
            skLineSegment(sketch, "E709", {"start": v(6195.19, 6666.35) * mm, "end": v(6238.86, 6745.1) * mm});
            skLineSegment(sketch, "E710", {"start": v(6238.86, 6745.1) * mm, "end": v(6282.5, 6824.48) * mm});
            skLineSegment(sketch, "E711", {"start": v(6282.5, 6824.48) * mm, "end": v(6325.9, 6904.15) * mm});
            skLineSegment(sketch, "E712", {"start": v(6325.9, 6904.15) * mm, "end": v(6368.84, 6983.82) * mm});
            skLineSegment(sketch, "E713", {"start": v(6368.84, 6983.82) * mm, "end": v(6411.07, 7063.02) * mm});
            skLineSegment(sketch, "E714", {"start": v(6411.07, 7063.02) * mm, "end": v(6453.32, 7143.17) * mm});
            skLineSegment(sketch, "E715", {"start": v(6453.32, 7143.17) * mm, "end": v(6494.52, 7222.16) * mm});
            skLineSegment(sketch, "E716", {"start": v(6494.52, 7222.16) * mm, "end": v(6534.66, 7299.8) * mm});
            skLineSegment(sketch, "E717", {"start": v(6534.66, 7299.8) * mm, "end": v(6574.84, 7378.12) * mm});
            skLineSegment(sketch, "E718", {"start": v(6574.84, 7378.12) * mm, "end": v(6494.4, 7419.7) * mm});
            skLineSegment(sketch, "E719", {"start": v(6538.01, 7509.7) * mm, "end": v(6454.74, 7550.05) * mm});
            skLineSegment(sketch, "E720", {"start": v(6454.74, 7550.05) * mm, "end": v(6452.22, 7551.23) * mm});
            skLineSegment(sketch, "E721", {"start": v(6452.22, 7551.23) * mm, "end": v(6373.83, 7586.56) * mm});
            skLineSegment(sketch, "E722", {"start": v(6373.83, 7586.56) * mm, "end": v(6371.4, 7587.62) * mm});
            skLineSegment(sketch, "E723", {"start": v(6371.4, 7587.62) * mm, "end": v(6290.34, 7621.58) * mm});
            skLineSegment(sketch, "E724", {"start": v(6290.34, 7621.58) * mm, "end": v(6287.76, 7622.62) * mm});
            skLineSegment(sketch, "E725", {"start": v(6287.76, 7622.62) * mm, "end": v(6205.74, 7654.33) * mm});
            skLineSegment(sketch, "E726", {"start": v(6205.74, 7654.33) * mm, "end": v(6203.1, 7655.31) * mm});
            skLineSegment(sketch, "E727", {"start": v(6203.1, 7655.31) * mm, "end": v(6120.17, 7684.72) * mm});
            skLineSegment(sketch, "E728", {"start": v(6120.17, 7684.72) * mm, "end": v(6117.47, 7685.64) * mm});
            skLineSegment(sketch, "E729", {"start": v(6117.47, 7685.64) * mm, "end": v(6033.7, 7712.7) * mm});
            skLineSegment(sketch, "E730", {"start": v(6033.7, 7712.7) * mm, "end": v(6030.96, 7713.53) * mm});
            skLineSegment(sketch, "E731", {"start": v(6030.96, 7713.53) * mm, "end": v(5946.4, 7738.19) * mm});
            skLineSegment(sketch, "E732", {"start": v(5946.4, 7738.19) * mm, "end": v(5943.63, 7738.95) * mm});
            skLineSegment(sketch, "E733", {"start": v(5943.63, 7738.95) * mm, "end": v(5858.38, 7761.18) * mm});
            skLineSegment(sketch, "E734", {"start": v(5858.38, 7761.18) * mm, "end": v(5855.58, 7761.86) * mm});
            skLineSegment(sketch, "E735", {"start": v(5855.58, 7761.86) * mm, "end": v(5769.69, 7781.63) * mm});
            skLineSegment(sketch, "E736", {"start": v(5769.69, 7781.63) * mm, "end": v(5766.87, 7782.24) * mm});
            skLineSegment(sketch, "E737", {"start": v(5766.87, 7782.24) * mm, "end": v(5680.7, 7799.47) * mm});
            skLineSegment(sketch, "E738", {"start": v(5680.7, 7799.47) * mm, "end": v(5677.88, 7800) * mm});
            skLineSegment(sketch, "E739", {"start": v(5677.88, 7800) * mm, "end": v(5591.96, 7814.62) * mm});
            skLineSegment(sketch, "E740", {"start": v(5591.96, 7814.62) * mm, "end": v(5589.13, 7815.06) * mm});
            skLineSegment(sketch, "E741", {"start": v(5589.13, 7815.06) * mm, "end": v(5502.82, 7827.23) * mm});
            skLineSegment(sketch, "E742", {"start": v(5502.82, 7827.23) * mm, "end": v(5499.98, 7827.59) * mm});
            skLineSegment(sketch, "E743", {"start": v(5499.98, 7827.59) * mm, "end": v(5413.33, 7837.28) * mm});
            skLineSegment(sketch, "E744", {"start": v(5413.33, 7837.28) * mm, "end": v(5410.49, 7837.56) * mm});
            skLineSegment(sketch, "E745", {"start": v(5410.49, 7837.56) * mm, "end": v(5323.6, 7844.77) * mm});
            skLineSegment(sketch, "E746", {"start": v(5323.6, 7844.77) * mm, "end": v(5320.73, 7844.97) * mm});
            skLineSegment(sketch, "E747", {"start": v(5320.73, 7844.97) * mm, "end": v(5233.66, 7849.69) * mm});
            skLineSegment(sketch, "E748", {"start": v(5233.66, 7849.69) * mm, "end": v(5230.8, 7849.8) * mm});
            skLineSegment(sketch, "E749", {"start": v(5230.8, 7849.8) * mm, "end": v(5143.62, 7852.03) * mm});
            skLineSegment(sketch, "E750", {"start": v(5143.62, 7852.03) * mm, "end": v(5140.76, 7852.06) * mm});
            skLineSegment(sketch, "E751", {"start": v(5140.76, 7852.06) * mm, "end": v(5053.56, 7851.8) * mm});
            skLineSegment(sketch, "E752", {"start": v(5053.56, 7851.8) * mm, "end": v(5050.7, 7851.75) * mm});
            skLineSegment(sketch, "E753", {"start": v(5050.7, 7851.75) * mm, "end": v(4963.54, 7848.99) * mm});
            skLineSegment(sketch, "E754", {"start": v(4963.54, 7848.99) * mm, "end": v(4960.68, 7848.85) * mm});
            skLineSegment(sketch, "E755", {"start": v(4960.68, 7848.85) * mm, "end": v(4873.63, 7843.6) * mm});
            skLineSegment(sketch, "E756", {"start": v(4873.63, 7843.6) * mm, "end": v(4870.78, 7843.39) * mm});
            skLineSegment(sketch, "E757", {"start": v(4870.78, 7843.39) * mm, "end": v(4783.93, 7835.64) * mm});
            skLineSegment(sketch, "E758", {"start": v(4783.93, 7835.64) * mm, "end": v(4781.08, 7835.35) * mm});
            skLineSegment(sketch, "E759", {"start": v(4781.08, 7835.35) * mm, "end": v(4694.5, 7825.12) * mm});
            skLineSegment(sketch, "E760", {"start": v(4694.5, 7825.12) * mm, "end": v(4691.66, 7824.74) * mm});
            skLineSegment(sketch, "E761", {"start": v(4691.66, 7824.74) * mm, "end": v(4605.42, 7812.04) * mm});
            skLineSegment(sketch, "E762", {"start": v(4605.42, 7812.04) * mm, "end": v(4602.6, 7811.59) * mm});
            skLineSegment(sketch, "E763", {"start": v(4602.6, 7811.59) * mm, "end": v(4516.78, 7796.43) * mm});
            skLineSegment(sketch, "E764", {"start": v(4516.78, 7796.43) * mm, "end": v(4513.97, 7795.9) * mm});
            skLineSegment(sketch, "E765", {"start": v(4513.97, 7795.9) * mm, "end": v(4428.63, 7778.3) * mm});
            skLineSegment(sketch, "E766", {"start": v(4428.63, 7778.3) * mm, "end": v(4425.84, 7777.68) * mm});
            skLineSegment(sketch, "E767", {"start": v(4425.84, 7777.68) * mm, "end": v(4341.06, 7757.66) * mm});
            skLineSegment(sketch, "E768", {"start": v(4341.06, 7757.66) * mm, "end": v(4338.3, 7756.97) * mm});
            skLineSegment(sketch, "E769", {"start": v(4338.3, 7756.97) * mm, "end": v(4254.16, 7734.56) * mm});
            skLineSegment(sketch, "E770", {"start": v(4254.16, 7734.56) * mm, "end": v(4251.43, 7733.79) * mm});
            skLineSegment(sketch, "E771", {"start": v(4251.43, 7733.79) * mm, "end": v(4167.98, 7709) * mm});
            skLineSegment(sketch, "E772", {"start": v(4167.98, 7709) * mm, "end": v(4165.28, 7708.16) * mm});
            skLineSegment(sketch, "E773", {"start": v(4165.28, 7708.16) * mm, "end": v(4082.61, 7681.03) * mm});
            skLineSegment(sketch, "E774", {"start": v(4082.61, 7681.03) * mm, "end": v(4079.95, 7680.12) * mm});
            skLineSegment(sketch, "E775", {"start": v(4079.95, 7680.12) * mm, "end": v(3998.12, 7650.7) * mm});
            skLineSegment(sketch, "E776", {"start": v(3998.12, 7650.7) * mm, "end": v(3995.52, 7649.72) * mm});
            skLineSegment(sketch, "E777", {"start": v(3995.52, 7649.72) * mm, "end": v(3914.57, 7618.05) * mm});
            skLineSegment(sketch, "E778", {"start": v(3914.57, 7618.05) * mm, "end": v(3912.03, 7617.02) * mm});
            skLineSegment(sketch, "E779", {"start": v(3912.03, 7617.02) * mm, "end": v(3832.04, 7583.16) * mm});
            skLineSegment(sketch, "E780", {"start": v(3832.04, 7583.16) * mm, "end": v(3829.58, 7582.08) * mm});
            skLineSegment(sketch, "E781", {"start": v(3829.58, 7582.08) * mm, "end": v(3750.58, 7546.1) * mm});
            skLineSegment(sketch, "E782", {"start": v(3750.58, 7546.1) * mm, "end": v(3748.23, 7545) * mm});
            skLineSegment(sketch, "E783", {"start": v(3748.23, 7545) * mm, "end": v(3670.26, 7507.02) * mm});
            skLineSegment(sketch, "E784", {"start": v(3670.26, 7507.02) * mm, "end": v(3668.04, 7505.9) * mm});
            skLineSegment(sketch, "E785", {"start": v(3668.04, 7505.9) * mm, "end": v(3591.09, 7466.03) * mm});
            skLineSegment(sketch, "E786", {"start": v(3591.09, 7466.03) * mm, "end": v(3502.6, 7420.17) * mm});
            skLineSegment(sketch, "E787", {"start": v(3502.6, 7420.17) * mm, "end": v(3548.16, 7331.53) * mm});
            skLineSegment(sketch, "E788", {"start": v(3548.16, 7331.53) * mm, "end": v(3588.47, 7253.1) * mm});
            skLineSegment(sketch, "E789", {"start": v(3588.47, 7253.1) * mm, "end": v(3628.81, 7175.2) * mm});
            skLineSegment(sketch, "E790", {"start": v(3628.81, 7175.2) * mm, "end": v(3670.26, 7095.88) * mm});
            skLineSegment(sketch, "E791", {"start": v(3670.26, 7095.88) * mm, "end": v(3712.77, 7015.35) * mm});
            skLineSegment(sketch, "E792", {"start": v(3712.77, 7015.35) * mm, "end": v(3755.27, 6935.77) * mm});
            skLineSegment(sketch, "E793", {"start": v(3755.27, 6935.77) * mm, "end": v(3798.46, 6855.75) * mm});
            skLineSegment(sketch, "E794", {"start": v(3798.46, 6855.75) * mm, "end": v(3842.1, 6775.73) * mm});
            skLineSegment(sketch, "E795", {"start": v(3842.1, 6775.73) * mm, "end": v(3885.98, 6696.05) * mm});
            skLineSegment(sketch, "E796", {"start": v(3885.98, 6696.05) * mm, "end": v(3929.86, 6617.02) * mm});
            skLineSegment(sketch, "E797", {"start": v(3929.86, 6617.02) * mm, "end": v(3973.53, 6538.94) * mm});
            skLineSegment(sketch, "E798", {"start": v(3973.53, 6538.94) * mm, "end": v(4016.78, 6462.08) * mm});
            skLineSegment(sketch, "E799", {"start": v(4016.78, 6462.08) * mm, "end": v(4059.37, 6386.65) * mm});
            skLineSegment(sketch, "E800", {"start": v(4059.37, 6386.65) * mm, "end": v(4101.17, 6312.8) * mm});
            skLineSegment(sketch, "E801", {"start": v(4101.17, 6312.8) * mm, "end": v(4144.63, 6236.24) * mm});
            skLineSegment(sketch, "E802", {"start": v(4144.63, 6236.24) * mm, "end": v(4187.54, 6160.76) * mm});
            skLineSegment(sketch, "E803", {"start": v(4187.54, 6160.76) * mm, "end": v(4231.05, 6084.27) * mm});
            skLineSegment(sketch, "E804", {"start": v(4231.05, 6084.27) * mm, "end": v(4275.04, 6006.82) * mm});
            skLineSegment(sketch, "E805", {"start": v(4275.04, 6006.82) * mm, "end": v(4319.25, 5928.65) * mm});
            skLineSegment(sketch, "E806", {"start": v(4319.25, 5928.65) * mm, "end": v(4364.4, 5848.3) * mm});
            skLineSegment(sketch, "E807", {"start": v(4364.4, 5848.3) * mm, "end": v(4406.86, 5771.59) * mm});
            skLineSegment(sketch, "E808", {"start": v(4406.86, 5771.59) * mm, "end": v(4448.71, 5694.77) * mm});
            skLineSegment(sketch, "E809", {"start": v(4448.71, 5694.77) * mm, "end": v(4489.74, 5617.83) * mm});
            skLineSegment(sketch, "E810", {"start": v(4489.74, 5617.83) * mm, "end": v(4529.77, 5540.69) * mm});
            skLineSegment(sketch, "E811", {"start": v(4529.77, 5540.69) * mm, "end": v(4568.54, 5463.37) * mm});
            skLineSegment(sketch, "E812", {"start": v(4568.54, 5463.37) * mm, "end": v(4607.34, 5382.24) * mm});
            skLineSegment(sketch, "E813", {"start": v(4607.34, 5382.24) * mm, "end": v(4643.6, 5302.4) * mm});
            skLineSegment(sketch, "E814", {"start": v(4643.6, 5302.4) * mm, "end": v(4677.07, 5224.07) * mm});
            skLineSegment(sketch, "E815", {"start": v(4677.07, 5224.07) * mm, "end": v(4707.73, 5147.22) * mm});
            skLineSegment(sketch, "E816", {"start": v(4707.73, 5147.22) * mm, "end": v(4736.19, 5070.88) * mm});
            skLineSegment(sketch, "E817", {"start": v(4736.19, 5070.88) * mm, "end": v(4773.9, 4969.73) * mm});
            skLineSegment(sketch, "E818", {"start": v(4773.9, 4969.73) * mm, "end": v(4871.88, 5015.06) * mm});
            skLineSegment(sketch, "E819", {"start": v(4871.88, 5015.06) * mm, "end": v(4928.81, 5040.92) * mm});
            skLineSegment(sketch, "E820", {"start": v(4928.81, 5040.92) * mm, "end": v(4942.1, 5046.39) * mm});
            skLineSegment(sketch, "E821", {"start": v(4942.1, 5046.39) * mm, "end": v(4955.22, 5051.44) * mm});
            skLineSegment(sketch, "E822", {"start": v(4955.22, 5051.44) * mm, "end": v(4968.26, 5056.1) * mm});
            skLineSegment(sketch, "E823", {"start": v(4968.26, 5056.1) * mm, "end": v(4981.25, 5060.34) * mm});
            skLineSegment(sketch, "E824", {"start": v(4981.25, 5060.34) * mm, "end": v(4994.24, 5064.18) * mm});
            skLineSegment(sketch, "E825", {"start": v(4994.24, 5064.18) * mm, "end": v(5007.23, 5067.6) * mm});
            skLineSegment(sketch, "E826", {"start": v(5007.23, 5067.6) * mm, "end": v(5020.25, 5070.62) * mm});
            skLineSegment(sketch, "E827", {"start": v(5020.25, 5070.62) * mm, "end": v(5033.3, 5073.22) * mm});
            skLineSegment(sketch, "E828", {"start": v(5033.3, 5073.22) * mm, "end": v(5046.35, 5075.4) * mm});
            skLineSegment(sketch, "E829", {"start": v(5046.35, 5075.4) * mm, "end": v(5059.44, 5077.15) * mm});
            skLineSegment(sketch, "E830", {"start": v(5059.44, 5077.15) * mm, "end": v(5072.56, 5078.47) * mm});
            skLineSegment(sketch, "E831", {"start": v(5072.56, 5078.47) * mm, "end": v(5085.7, 5079.37) * mm});
            skLineSegment(sketch, "E832", {"start": v(5085.7, 5079.37) * mm, "end": v(5098.85, 5079.84) * mm});
            skLineSegment(sketch, "E833", {"start": v(5098.85, 5079.84) * mm, "end": v(5112, 5079.89) * mm});
            skLineSegment(sketch, "E834", {"start": v(5112, 5079.89) * mm, "end": v(5125.16, 5079.5) * mm});
            skLineSegment(sketch, "E835", {"start": v(5125.16, 5079.5) * mm, "end": v(5138.3, 5078.7) * mm});
            skLineSegment(sketch, "E836", {"start": v(5138.3, 5078.7) * mm, "end": v(5151.41, 5077.45) * mm});
            skLineSegment(sketch, "E837", {"start": v(5151.41, 5077.45) * mm, "end": v(5164.5, 5075.78) * mm});
            skLineSegment(sketch, "E838", {"start": v(5164.5, 5075.78) * mm, "end": v(5177.57, 5073.7) * mm});
            skLineSegment(sketch, "E839", {"start": v(5177.57, 5073.7) * mm, "end": v(5190.62, 5071.18) * mm});
            skLineSegment(sketch, "E840", {"start": v(5190.62, 5071.18) * mm, "end": v(5203.8, 5068.22) * mm});
            skLineSegment(sketch, "E841", {"start": v(5203.8, 5068.22) * mm, "end": v(5216.96, 5064.83) * mm});
            skLineSegment(sketch, "E842", {"start": v(5216.96, 5064.83) * mm, "end": v(5230.1, 5061.03) * mm});
            skLineSegment(sketch, "E843", {"start": v(5230.1, 5061.03) * mm, "end": v(5243.26, 5056.8) * mm});
            skLineSegment(sketch, "E844", {"start": v(5243.26, 5056.8) * mm, "end": v(5256.45, 5052.16) * mm});
            skLineSegment(sketch, "E845", {"start": v(5256.45, 5052.16) * mm, "end": v(5269.72, 5047.11) * mm});
            skLineSegment(sketch, "E846", {"start": v(5269.72, 5047.11) * mm, "end": v(5283.15, 5041.64) * mm});
            skLineSegment(sketch, "E847", {"start": v(5283.15, 5041.64) * mm, "end": v(5341.66, 5015.24) * mm});
            skLineSegment(sketch, "E848", {"start": v(5341.66, 5015.24) * mm, "end": v(5439.62, 4970.06) * mm});
            skLineSegment(sketch, "E849", {"start": v(5439.62, 4970.06) * mm, "end": v(5477.26, 5071.16) * mm});
            skLineSegment(sketch, "E850", {"start": v(5477.26, 5071.16) * mm, "end": v(5505.68, 5147.51) * mm});
            skLineSegment(sketch, "E851", {"start": v(5505.68, 5147.51) * mm, "end": v(5536.3, 5224.38) * mm});
            skLineSegment(sketch, "E852", {"start": v(5536.3, 5224.38) * mm, "end": v(5569.7, 5302.73) * mm});
            skLineSegment(sketch, "E853", {"start": v(5569.7, 5302.73) * mm, "end": v(5605.9, 5382.58) * mm});
            skLineSegment(sketch, "E854", {"start": v(5605.9, 5382.58) * mm, "end": v(5644.65, 5463.72) * mm});
            skLineSegment(sketch, "E855", {"start": v(5644.65, 5463.72) * mm, "end": v(5683.36, 5541.06) * mm});
            skLineSegment(sketch, "E856", {"start": v(5683.36, 5541.06) * mm, "end": v(5723.33, 5618.21) * mm});
            skLineSegment(sketch, "E857", {"start": v(5723.33, 5618.21) * mm, "end": v(5764.3, 5695.17) * mm});
            skLineSegment(sketch, "E858", {"start": v(5764.3, 5695.17) * mm, "end": v(5806.1, 5772.01) * mm});
            skLineSegment(sketch, "E859", {"start": v(5806.1, 5772.01) * mm, "end": v(5848.51, 5848.74) * mm});
            skLineSegment(sketch, "E860", {"start": v(5848.51, 5848.74) * mm, "end": v(5893.6, 5929.12) * mm});
            skLineSegment(sketch, "E861", {"start": v(5893.6, 5929.12) * mm, "end": v(5937.76, 6007.31) * mm});
            skLineSegment(sketch, "E862", {"start": v(5937.76, 6007.31) * mm, "end": v(5981.7, 6084.79) * mm});
            skLineSegment(sketch, "E863", {"start": v(5981.7, 6084.79) * mm, "end": v(6025.16, 6161.3) * mm});
            skLineSegment(sketch, "E864", {"start": v(6025.16, 6161.3) * mm, "end": v(6068.02, 6236.81) * mm});
            skLineSegment(sketch, "E865", {"start": v(6068.02, 6236.81) * mm, "end": v(6111.44, 6313.4) * mm});
            skLineSegment(sketch, "E866", {"start": v(6111.44, 6313.4) * mm, "end": v(6153.18, 6387.27) * mm});
            skLineSegment(sketch, "E867", {"start": v(6153.18, 6387.27) * mm, "end": v(6195.74, 6462.72) * mm});
            skLineSegment(sketch, "E868", {"start": v(6195.74, 6462.72) * mm, "end": v(6238.93, 6539.62) * mm});
            skLineSegment(sketch, "E869", {"start": v(6238.93, 6539.62) * mm, "end": v(6282.56, 6617.72) * mm});
            skLineSegment(sketch, "E870", {"start": v(6282.56, 6617.72) * mm, "end": v(6326.4, 6696.77) * mm});
            skLineSegment(sketch, "E871", {"start": v(6326.4, 6696.77) * mm, "end": v(6370.23, 6776.47) * mm});
            skLineSegment(sketch, "E872", {"start": v(6370.23, 6776.47) * mm, "end": v(6413.82, 6856.52) * mm});
            skLineSegment(sketch, "E873", {"start": v(6413.82, 6856.52) * mm, "end": v(6456.97, 6936.57) * mm});
            skLineSegment(sketch, "E874", {"start": v(6456.97, 6936.57) * mm, "end": v(6499.42, 7016.17) * mm});
            skLineSegment(sketch, "E875", {"start": v(6499.42, 7016.17) * mm, "end": v(6541.88, 7096.73) * mm});
            skLineSegment(sketch, "E876", {"start": v(6541.88, 7096.73) * mm, "end": v(6583.27, 7176.08) * mm});
            skLineSegment(sketch, "E877", {"start": v(6583.27, 7176.08) * mm, "end": v(6623.56, 7254) * mm});
            skLineSegment(sketch, "E878", {"start": v(6623.56, 7254) * mm, "end": v(6663.81, 7332.47) * mm});
            skLineSegment(sketch, "E879", {"start": v(6663.81, 7332.47) * mm, "end": v(6709.32, 7421.16) * mm});
            skLineSegment(sketch, "E880", {"start": v(6709.32, 7421.16) * mm, "end": v(6620.77, 7466.94) * mm});
            skLineSegment(sketch, "E881", {"start": v(6620.77, 7466.94) * mm, "end": v(6540.33, 7508.53) * mm});
            skLineSegment(sketch, "E882", {"start": v(6540.33, 7508.53) * mm, "end": v(6538.01, 7509.7) * mm});
            skLineSegment(sketch, "E883", {"start": v(6689.36, 8895.6) * mm, "end": v(6698.57, 8959.14) * mm});
            skLineSegment(sketch, "E884", {"start": v(6698.57, 8959.14) * mm, "end": v(6707.5, 9021.57) * mm});
            skLineSegment(sketch, "E885", {"start": v(6707.5, 9021.57) * mm, "end": v(6715.9, 9082.75) * mm});
            skLineSegment(sketch, "E886", {"start": v(6715.9, 9082.75) * mm, "end": v(6724.22, 9146.37) * mm});
            skLineSegment(sketch, "E887", {"start": v(6724.22, 9146.37) * mm, "end": v(6731.92, 9210.47) * mm});
            skLineSegment(sketch, "E888", {"start": v(6731.92, 9210.47) * mm, "end": v(6738.78, 9274.95) * mm});
            skLineSegment(sketch, "E889", {"start": v(6738.78, 9274.95) * mm, "end": v(6744.64, 9339.64) * mm});
            skLineSegment(sketch, "E890", {"start": v(6744.64, 9339.64) * mm, "end": v(6749.51, 9405.17) * mm});
            skLineSegment(sketch, "E891", {"start": v(6749.51, 9405.17) * mm, "end": v(6749.63, 9406.97) * mm});
            skLineSegment(sketch, "E892", {"start": v(6749.63, 9406.97) * mm, "end": v(6753.2, 9470.67) * mm});
            skLineSegment(sketch, "E893", {"start": v(6753.2, 9470.67) * mm, "end": v(6753.3, 9472.5) * mm});
            skLineSegment(sketch, "E894", {"start": v(6753.3, 9472.5) * mm, "end": v(6755.66, 9535.62) * mm});
            skLineSegment(sketch, "E895", {"start": v(6755.66, 9535.62) * mm, "end": v(6755.72, 9537.44) * mm});
            skLineSegment(sketch, "E896", {"start": v(6755.72, 9537.44) * mm, "end": v(6756.91, 9599.2) * mm});
            skLineSegment(sketch, "E897", {"start": v(6756.91, 9599.2) * mm, "end": v(6756.93, 9601) * mm});
            skLineSegment(sketch, "E898", {"start": v(6756.93, 9601) * mm, "end": v(6757.01, 9663.83) * mm});
            skLineSegment(sketch, "E899", {"start": v(6757.01, 9663.83) * mm, "end": v(6757, 9665.6) * mm});
            skLineSegment(sketch, "E900", {"start": v(6757, 9665.6) * mm, "end": v(6755.92, 9731.02) * mm});
            skLineSegment(sketch, "E901", {"start": v(6755.92, 9731.02) * mm, "end": v(6753.67, 9798.8) * mm});
            skLineSegment(sketch, "E902", {"start": v(6753.67, 9798.8) * mm, "end": v(6750.87, 9863.3) * mm});
            skLineSegment(sketch, "E903", {"start": v(6750.87, 9863.3) * mm, "end": v(6747.5, 9927.22) * mm});
            skLineSegment(sketch, "E904", {"start": v(6747.5, 9927.22) * mm, "end": v(6743.92, 9989.34) * mm});
            skLineSegment(sketch, "E905", {"start": v(6743.92, 9989.34) * mm, "end": v(6740.08, 10052.65) * mm});
            skLineSegment(sketch, "E906", {"start": v(6740.08, 10052.65) * mm, "end": v(6736.42, 10115.84) * mm});
            skLineSegment(sketch, "E907", {"start": v(6736.42, 10115.84) * mm, "end": v(6731.02, 10208.92) * mm});
            skLineSegment(sketch, "E908", {"start": v(6731.02, 10208.92) * mm, "end": v(6637.8, 10210.04) * mm});
            skLineSegment(sketch, "E909", {"start": v(6637.8, 10210.04) * mm, "end": v(6574.45, 10210.8) * mm});
            skLineSegment(sketch, "E910", {"start": v(6574.45, 10210.8) * mm, "end": v(6511.36, 10212.31) * mm});
            skLineSegment(sketch, "E911", {"start": v(6511.36, 10212.31) * mm, "end": v(6447.79, 10214.36) * mm});
            skLineSegment(sketch, "E912", {"start": v(6447.79, 10214.36) * mm, "end": v(6385.77, 10216.54) * mm});
            skLineSegment(sketch, "E913", {"start": v(6385.77, 10216.54) * mm, "end": v(6323.56, 10218.95) * mm});
            skLineSegment(sketch, "E914", {"start": v(6323.56, 10218.95) * mm, "end": v(6261.02, 10221.49) * mm});
            skLineSegment(sketch, "E915", {"start": v(6261.02, 10221.49) * mm, "end": v(6198.27, 10224.05) * mm});
            skLineSegment(sketch, "E916", {"start": v(6198.27, 10224.05) * mm, "end": v(6135.32, 10226.58) * mm});
            skLineSegment(sketch, "E917", {"start": v(6135.32, 10226.58) * mm, "end": v(6072.22, 10229.05) * mm});
            skLineSegment(sketch, "E918", {"start": v(6072.22, 10229.05) * mm, "end": v(6008.96, 10231.4) * mm});
            skLineSegment(sketch, "E919", {"start": v(6008.96, 10231.4) * mm, "end": v(5945.56, 10233.6) * mm});
            skLineSegment(sketch, "E920", {"start": v(5945.56, 10233.6) * mm, "end": v(5882.14, 10235.64) * mm});
            skLineSegment(sketch, "E921", {"start": v(5882.14, 10235.64) * mm, "end": v(5818.66, 10237.54) * mm});
            skLineSegment(sketch, "E922", {"start": v(5818.66, 10237.54) * mm, "end": v(5755.13, 10239.3) * mm});
            skLineSegment(sketch, "E923", {"start": v(5755.13, 10239.3) * mm, "end": v(5691.54, 10240.94) * mm});
            skLineSegment(sketch, "E924", {"start": v(5691.54, 10240.94) * mm, "end": v(5628.2, 10242.4) * mm});
            skLineSegment(sketch, "E925", {"start": v(5628.2, 10242.4) * mm, "end": v(5565.3, 10243.71) * mm});
            skLineSegment(sketch, "E926", {"start": v(5565.3, 10243.71) * mm, "end": v(5502.35, 10244.88) * mm});
            skLineSegment(sketch, "E927", {"start": v(5502.35, 10244.88) * mm, "end": v(5439.38, 10245.9) * mm});
            skLineSegment(sketch, "E928", {"start": v(5439.38, 10245.9) * mm, "end": v(5376.42, 10246.76) * mm});
            skLineSegment(sketch, "E929", {"start": v(5376.42, 10246.76) * mm, "end": v(5313.42, 10247.49) * mm});
            skLineSegment(sketch, "E930", {"start": v(5313.42, 10247.49) * mm, "end": v(5250.4, 10248.06) * mm});
            skLineSegment(sketch, "E931", {"start": v(5250.4, 10248.06) * mm, "end": v(5187.4, 10248.5) * mm});
            skLineSegment(sketch, "E932", {"start": v(5187.4, 10248.5) * mm, "end": v(5124.36, 10248.78) * mm});
            skLineSegment(sketch, "E933", {"start": v(5124.36, 10248.78) * mm, "end": v(5061.34, 10248.9) * mm});
            skLineSegment(sketch, "E934", {"start": v(5061.34, 10248.9) * mm, "end": v(4998.34, 10248.9) * mm});
            skLineSegment(sketch, "E935", {"start": v(4998.34, 10248.9) * mm, "end": v(4935.3, 10248.75) * mm});
            skLineSegment(sketch, "E936", {"start": v(4935.3, 10248.75) * mm, "end": v(4872.27, 10248.45) * mm});
            skLineSegment(sketch, "E937", {"start": v(4872.27, 10248.45) * mm, "end": v(4809.26, 10248) * mm});
            skLineSegment(sketch, "E938", {"start": v(4809.26, 10248) * mm, "end": v(4746.24, 10247.4) * mm});
            skLineSegment(sketch, "E939", {"start": v(4746.24, 10247.4) * mm, "end": v(4683.25, 10246.64) * mm});
            skLineSegment(sketch, "E940", {"start": v(4683.25, 10246.64) * mm, "end": v(4620.27, 10245.74) * mm});
            skLineSegment(sketch, "E941", {"start": v(4620.27, 10245.74) * mm, "end": v(4557.28, 10244.69) * mm});
            skLineSegment(sketch, "E942", {"start": v(4557.28, 10244.69) * mm, "end": v(4494.34, 10243.48) * mm});
            skLineSegment(sketch, "E943", {"start": v(4494.34, 10243.48) * mm, "end": v(4431.43, 10242.13) * mm});
            skLineSegment(sketch, "E944", {"start": v(4431.43, 10242.13) * mm, "end": v(4368.56, 10240.63) * mm});
            skLineSegment(sketch, "E945", {"start": v(4368.56, 10240.63) * mm, "end": v(4305.73, 10238.99) * mm});
            skLineSegment(sketch, "E946", {"start": v(4305.73, 10238.99) * mm, "end": v(4242.95, 10237.22) * mm});
            skLineSegment(sketch, "E947", {"start": v(4242.95, 10237.22) * mm, "end": v(4180.24, 10235.31) * mm});
            skLineSegment(sketch, "E948", {"start": v(4180.24, 10235.31) * mm, "end": v(4117.54, 10233.27) * mm});
            skLineSegment(sketch, "E949", {"start": v(4117.54, 10233.27) * mm, "end": v(4054.92, 10231.07) * mm});
            skLineSegment(sketch, "E950", {"start": v(4054.92, 10231.07) * mm, "end": v(3992.4, 10228.72) * mm});
            skLineSegment(sketch, "E951", {"start": v(3992.4, 10228.72) * mm, "end": v(3930.06, 10226.27) * mm});
            skLineSegment(sketch, "E952", {"start": v(3930.06, 10226.27) * mm, "end": v(3867.87, 10223.76) * mm});
            skLineSegment(sketch, "E953", {"start": v(3867.87, 10223.76) * mm, "end": v(3805.86, 10221.21) * mm});
            skLineSegment(sketch, "E954", {"start": v(3805.86, 10221.21) * mm, "end": v(3744.09, 10218.7) * mm});
            skLineSegment(sketch, "E955", {"start": v(3744.09, 10218.7) * mm, "end": v(3682.63, 10216.33) * mm});
            skLineSegment(sketch, "E956", {"start": v(3682.63, 10216.33) * mm, "end": v(3621.47, 10214.2) * mm});
            skLineSegment(sketch, "E957", {"start": v(3621.47, 10214.2) * mm, "end": v(3560.67, 10212.38) * mm});
            skLineSegment(sketch, "E958", {"start": v(3560.67, 10212.38) * mm, "end": v(3500.35, 10211.1) * mm});
            skLineSegment(sketch, "E959", {"start": v(3500.35, 10211.1) * mm, "end": v(3439.75, 10210.5) * mm});
            skLineSegment(sketch, "E960", {"start": v(3439.75, 10210.5) * mm, "end": v(3346.3, 10209.6) * mm});
            skLineSegment(sketch, "E961", {"start": v(3346.3, 10209.6) * mm, "end": v(3340.89, 10116.3) * mm});
            skLineSegment(sketch, "E962", {"start": v(3340.89, 10116.3) * mm, "end": v(3337.22, 10053.12) * mm});
            skLineSegment(sketch, "E963", {"start": v(3337.22, 10053.12) * mm, "end": v(3333.39, 9989.78) * mm});
            skLineSegment(sketch, "E964", {"start": v(3333.39, 9989.78) * mm, "end": v(3329.83, 9927.65) * mm});
            skLineSegment(sketch, "E965", {"start": v(3329.83, 9927.65) * mm, "end": v(3326.46, 9863.73) * mm});
            skLineSegment(sketch, "E966", {"start": v(3326.46, 9863.73) * mm, "end": v(3323.67, 9799.24) * mm});
            skLineSegment(sketch, "E967", {"start": v(3323.67, 9799.24) * mm, "end": v(3321.42, 9731.45) * mm});
            skLineSegment(sketch, "E968", {"start": v(3321.42, 9731.45) * mm, "end": v(3320.34, 9666) * mm});
            skLineSegment(sketch, "E969", {"start": v(3320.34, 9666) * mm, "end": v(3320.33, 9664.24) * mm});
            skLineSegment(sketch, "E970", {"start": v(3320.33, 9664.24) * mm, "end": v(3320.41, 9601.4) * mm});
            skLineSegment(sketch, "E971", {"start": v(3320.41, 9601.4) * mm, "end": v(3320.43, 9599.6) * mm});
            skLineSegment(sketch, "E972", {"start": v(3320.43, 9599.6) * mm, "end": v(3321.62, 9537.83) * mm});
            skLineSegment(sketch, "E973", {"start": v(3321.62, 9537.83) * mm, "end": v(3321.67, 9536.02) * mm});
            skLineSegment(sketch, "E974", {"start": v(3321.67, 9536.02) * mm, "end": v(3324.03, 9472.9) * mm});
            skLineSegment(sketch, "E975", {"start": v(3324.03, 9472.9) * mm, "end": v(3324.12, 9471.06) * mm});
            skLineSegment(sketch, "E976", {"start": v(3324.12, 9471.06) * mm, "end": v(3327.67, 9407.35) * mm});
            skLineSegment(sketch, "E977", {"start": v(3327.67, 9407.35) * mm, "end": v(3327.79, 9405.55) * mm});
            skLineSegment(sketch, "E978", {"start": v(3327.79, 9405.55) * mm, "end": v(3332.64, 9340) * mm});
            skLineSegment(sketch, "E979", {"start": v(3332.64, 9340) * mm, "end": v(3338.48, 9275.3) * mm});
            skLineSegment(sketch, "E980", {"start": v(3338.48, 9275.3) * mm, "end": v(3345.3, 9210.81) * mm});
            skLineSegment(sketch, "E981", {"start": v(3345.3, 9210.81) * mm, "end": v(3352.97, 9146.7) * mm});
            skLineSegment(sketch, "E982", {"start": v(3352.97, 9146.7) * mm, "end": v(3361.25, 9083.08) * mm});
            skLineSegment(sketch, "E983", {"start": v(3361.25, 9083.08) * mm, "end": v(3369.6, 9021.9) * mm});
            skLineSegment(sketch, "E984", {"start": v(3369.6, 9021.9) * mm, "end": v(3378.52, 8959.44) * mm});
            skLineSegment(sketch, "E985", {"start": v(3378.52, 8959.44) * mm, "end": v(3387.7, 8895.86) * mm});
            skLineSegment(sketch, "E986", {"start": v(3387.7, 8895.86) * mm, "end": v(3397.02, 8830.9) * mm});
            skLineSegment(sketch, "E987", {"start": v(3397.02, 8830.9) * mm, "end": v(3410.36, 8737.88) * mm});
            skLineSegment(sketch, "E988", {"start": v(3410.36, 8737.88) * mm, "end": v(3504.04, 8745.43) * mm});
            skLineSegment(sketch, "E989", {"start": v(3504.04, 8745.43) * mm, "end": v(3562.2, 8750.13) * mm});
            skLineSegment(sketch, "E990", {"start": v(3562.2, 8750.13) * mm, "end": v(3619.94, 8753.9) * mm});
            skLineSegment(sketch, "E991", {"start": v(3619.94, 8753.9) * mm, "end": v(3678.11, 8756.98) * mm});
            skLineSegment(sketch, "E992", {"start": v(3678.11, 8756.98) * mm, "end": v(3736.65, 8759.5) * mm});
            skLineSegment(sketch, "E993", {"start": v(3736.65, 8759.5) * mm, "end": v(3795.5, 8761.55) * mm});
            skLineSegment(sketch, "E994", {"start": v(3795.5, 8761.55) * mm, "end": v(3854.64, 8763.23) * mm});
            skLineSegment(sketch, "E995", {"start": v(3854.64, 8763.23) * mm, "end": v(3914.04, 8764.62) * mm});
            skLineSegment(sketch, "E996", {"start": v(3914.04, 8764.62) * mm, "end": v(3973.65, 8765.78) * mm});
            skLineSegment(sketch, "E997", {"start": v(3973.65, 8765.78) * mm, "end": v(4033.42, 8766.77) * mm});
            skLineSegment(sketch, "E998", {"start": v(4033.42, 8766.77) * mm, "end": v(4093.36, 8767.62) * mm});
            skLineSegment(sketch, "E999", {"start": v(4093.36, 8767.62) * mm, "end": v(4153.42, 8768.36) * mm});
            skLineSegment(sketch, "E1000", {"start": v(4153.42, 8768.36) * mm, "end": v(4213.55, 8769.03) * mm});
            skLineSegment(sketch, "E1001", {"start": v(4213.55, 8769.03) * mm, "end": v(4273.75, 8769.6) * mm});
            skLineSegment(sketch, "E1002", {"start": v(4273.75, 8769.6) * mm, "end": v(4334.03, 8770.09) * mm});
            skLineSegment(sketch, "E1003", {"start": v(4334.03, 8770.09) * mm, "end": v(4394.37, 8770.51) * mm});
            skLineSegment(sketch, "E1004", {"start": v(4394.37, 8770.51) * mm, "end": v(4454.76, 8770.88) * mm});
            skLineSegment(sketch, "E1005", {"start": v(4454.76, 8770.88) * mm, "end": v(4515.15, 8771.2) * mm});
            skLineSegment(sketch, "E1006", {"start": v(4515.15, 8771.2) * mm, "end": v(4575.6, 8771.42) * mm});
            skLineSegment(sketch, "E1007", {"start": v(4575.6, 8771.42) * mm, "end": v(4636.1, 8771.6) * mm});
            skLineSegment(sketch, "E1008", {"start": v(4636.1, 8771.6) * mm, "end": v(4696.64, 8771.74) * mm});
            skLineSegment(sketch, "E1009", {"start": v(4696.64, 8771.74) * mm, "end": v(4757.2, 8771.83) * mm});
            skLineSegment(sketch, "E1010", {"start": v(4757.2, 8771.83) * mm, "end": v(4817.81, 8771.9) * mm});
            skLineSegment(sketch, "E1011", {"start": v(4817.81, 8771.9) * mm, "end": v(4878.44, 8771.97) * mm});
            skLineSegment(sketch, "E1012", {"start": v(4878.44, 8771.97) * mm, "end": v(4939.06, 8772) * mm});
            skLineSegment(sketch, "E1013", {"start": v(4939.06, 8772) * mm, "end": v(4999.69, 8772.02) * mm});
            skLineSegment(sketch, "E1014", {"start": v(4999.69, 8772.02) * mm, "end": v(5060.34, 8772.01) * mm});
            skLineSegment(sketch, "E1015", {"start": v(5060.34, 8772.01) * mm, "end": v(5120.98, 8772) * mm});
            skLineSegment(sketch, "E1016", {"start": v(5120.98, 8772) * mm, "end": v(5181.59, 8771.97) * mm});
            skLineSegment(sketch, "E1017", {"start": v(5181.59, 8771.97) * mm, "end": v(5242.2, 8771.9) * mm});
            skLineSegment(sketch, "E1018", {"start": v(5242.2, 8771.9) * mm, "end": v(5302.82, 8771.83) * mm});
            skLineSegment(sketch, "E1019", {"start": v(5302.82, 8771.83) * mm, "end": v(5363.39, 8771.73) * mm});
            skLineSegment(sketch, "E1020", {"start": v(5363.39, 8771.73) * mm, "end": v(5423.92, 8771.6) * mm});
            skLineSegment(sketch, "E1021", {"start": v(5423.92, 8771.6) * mm, "end": v(5484.42, 8771.4) * mm});
            skLineSegment(sketch, "E1022", {"start": v(5484.42, 8771.4) * mm, "end": v(5544.86, 8771.17) * mm});
            skLineSegment(sketch, "E1023", {"start": v(5544.86, 8771.17) * mm, "end": v(5605.26, 8770.86) * mm});
            skLineSegment(sketch, "E1024", {"start": v(5605.26, 8770.86) * mm, "end": v(5666.1, 8770.48) * mm});
            skLineSegment(sketch, "E1025", {"start": v(5666.1, 8770.48) * mm, "end": v(5727.17, 8770.05) * mm});
            skLineSegment(sketch, "E1026", {"start": v(5727.17, 8770.05) * mm, "end": v(5788.18, 8769.55) * mm});
            skLineSegment(sketch, "E1027", {"start": v(5788.18, 8769.55) * mm, "end": v(5849.1, 8768.97) * mm});
            skLineSegment(sketch, "E1028", {"start": v(5849.1, 8768.97) * mm, "end": v(5909.97, 8768.3) * mm});
            skLineSegment(sketch, "E1029", {"start": v(5909.97, 8768.3) * mm, "end": v(5970.75, 8767.56) * mm});
            skLineSegment(sketch, "E1030", {"start": v(5970.75, 8767.56) * mm, "end": v(6031.4, 8766.7) * mm});
            skLineSegment(sketch, "E1031", {"start": v(6031.4, 8766.7) * mm, "end": v(6091.91, 8765.7) * mm});
            skLineSegment(sketch, "E1032", {"start": v(6091.91, 8765.7) * mm, "end": v(6152.24, 8764.55) * mm});
            skLineSegment(sketch, "E1033", {"start": v(6152.24, 8764.55) * mm, "end": v(6212.38, 8763.16) * mm});
            skLineSegment(sketch, "E1034", {"start": v(6212.38, 8763.16) * mm, "end": v(6272.24, 8761.48) * mm});
            skLineSegment(sketch, "E1035", {"start": v(6272.24, 8761.48) * mm, "end": v(6331.82, 8759.42) * mm});
            skLineSegment(sketch, "E1036", {"start": v(6331.82, 8759.42) * mm, "end": v(6391.15, 8756.9) * mm});
            skLineSegment(sketch, "E1037", {"start": v(6391.15, 8756.9) * mm, "end": v(6451.99, 8753.8) * mm});
            skLineSegment(sketch, "E1038", {"start": v(6451.99, 8753.8) * mm, "end": v(6512.37, 8749.98) * mm});
            skLineSegment(sketch, "E1039", {"start": v(6512.37, 8749.98) * mm, "end": v(6573.17, 8745.18) * mm});
            skLineSegment(sketch, "E1040", {"start": v(6573.17, 8745.18) * mm, "end": v(6666.68, 8737.8) * mm});
            skLineSegment(sketch, "E1041", {"start": v(6666.68, 8737.8) * mm, "end": v(6680.02, 8830.64) * mm});
            skLineSegment(sketch, "E1042", {"start": v(6680.02, 8830.64) * mm, "end": v(6689.36, 8895.6) * mm});
            skLineSegment(sketch, "E1043", {"start": v(6531.16, 8393.71) * mm, "end": v(6504.72, 8396.79) * mm});
            skLineSegment(sketch, "E1044", {"start": v(6504.72, 8396.79) * mm, "end": v(6478.26, 8399.67) * mm});
            skLineSegment(sketch, "E1045", {"start": v(6478.26, 8399.67) * mm, "end": v(6451.78, 8402.35) * mm});
            skLineSegment(sketch, "E1046", {"start": v(6451.78, 8402.35) * mm, "end": v(6425.33, 8404.83) * mm});
            skLineSegment(sketch, "E1047", {"start": v(6425.33, 8404.83) * mm, "end": v(6398.88, 8407.12) * mm});
            skLineSegment(sketch, "E1048", {"start": v(6398.88, 8407.12) * mm, "end": v(6372.46, 8409.23) * mm});
            skLineSegment(sketch, "E1049", {"start": v(6372.46, 8409.23) * mm, "end": v(6346.72, 8411.12) * mm});
            skLineSegment(sketch, "E1050", {"start": v(6346.72, 8411.12) * mm, "end": v(6321.18, 8412.84) * mm});
            skLineSegment(sketch, "E1051", {"start": v(6321.18, 8412.84) * mm, "end": v(6295.65, 8414.41) * mm});
            skLineSegment(sketch, "E1052", {"start": v(6295.65, 8414.41) * mm, "end": v(6270.14, 8415.84) * mm});
            skLineSegment(sketch, "E1053", {"start": v(6270.14, 8415.84) * mm, "end": v(6244.64, 8417.13) * mm});
            skLineSegment(sketch, "E1054", {"start": v(6244.64, 8417.13) * mm, "end": v(6219.17, 8418.27) * mm});
            skLineSegment(sketch, "E1055", {"start": v(6219.17, 8418.27) * mm, "end": v(6193.73, 8419.3) * mm});
            skLineSegment(sketch, "E1056", {"start": v(6193.73, 8419.3) * mm, "end": v(6168.32, 8420.19) * mm});
            skLineSegment(sketch, "E1057", {"start": v(6168.32, 8420.19) * mm, "end": v(6142.93, 8420.96) * mm});
            skLineSegment(sketch, "E1058", {"start": v(6142.93, 8420.96) * mm, "end": v(6117.58, 8421.62) * mm});
            skLineSegment(sketch, "E1059", {"start": v(6117.58, 8421.62) * mm, "end": v(6092.27, 8422.18) * mm});
            skLineSegment(sketch, "E1060", {"start": v(6092.27, 8422.18) * mm, "end": v(6067, 8422.65) * mm});
            skLineSegment(sketch, "E1061", {"start": v(6067, 8422.65) * mm, "end": v(6041.77, 8423.03) * mm});
            skLineSegment(sketch, "E1062", {"start": v(6041.77, 8423.03) * mm, "end": v(6016.57, 8423.32) * mm});
            skLineSegment(sketch, "E1063", {"start": v(6016.57, 8423.32) * mm, "end": v(5991.4, 8423.55) * mm});
            skLineSegment(sketch, "E1064", {"start": v(5991.4, 8423.55) * mm, "end": v(5966.26, 8423.7) * mm});
            skLineSegment(sketch, "E1065", {"start": v(5966.26, 8423.7) * mm, "end": v(5941.15, 8423.8) * mm});
            skLineSegment(sketch, "E1066", {"start": v(5941.15, 8423.8) * mm, "end": v(5916.08, 8423.83) * mm});
            skLineSegment(sketch, "E1067", {"start": v(5916.08, 8423.83) * mm, "end": v(5891.02, 8423.81) * mm});
            skLineSegment(sketch, "E1068", {"start": v(5891.02, 8423.81) * mm, "end": v(5866, 8423.75) * mm});
            skLineSegment(sketch, "E1069", {"start": v(5866, 8423.75) * mm, "end": v(5841.01, 8423.64) * mm});
            skLineSegment(sketch, "E1070", {"start": v(5841.01, 8423.64) * mm, "end": v(5816.06, 8423.5) * mm});
            skLineSegment(sketch, "E1071", {"start": v(5816.06, 8423.5) * mm, "end": v(5791.13, 8423.32) * mm});
            skLineSegment(sketch, "E1072", {"start": v(5791.13, 8423.32) * mm, "end": v(5766.24, 8423.12) * mm});
            skLineSegment(sketch, "E1073", {"start": v(5766.24, 8423.12) * mm, "end": v(5741.36, 8422.9) * mm});
            skLineSegment(sketch, "E1074", {"start": v(5741.36, 8422.9) * mm, "end": v(5716.51, 8422.66) * mm});
            skLineSegment(sketch, "E1075", {"start": v(5716.51, 8422.66) * mm, "end": v(5691.67, 8422.4) * mm});
            skLineSegment(sketch, "E1076", {"start": v(5691.67, 8422.4) * mm, "end": v(5666.85, 8422.15) * mm});
            skLineSegment(sketch, "E1077", {"start": v(5666.85, 8422.15) * mm, "end": v(5642.04, 8421.87) * mm});
            skLineSegment(sketch, "E1078", {"start": v(5642.04, 8421.87) * mm, "end": v(5617.26, 8421.6) * mm});
            skLineSegment(sketch, "E1079", {"start": v(5617.26, 8421.6) * mm, "end": v(5592.5, 8421.32) * mm});
            skLineSegment(sketch, "E1080", {"start": v(5592.5, 8421.32) * mm, "end": v(5567.97, 8421.04) * mm});
            skLineSegment(sketch, "E1081", {"start": v(5567.97, 8421.04) * mm, "end": v(5543.51, 8420.78) * mm});
            skLineSegment(sketch, "E1082", {"start": v(5543.51, 8420.78) * mm, "end": v(5519.07, 8420.51) * mm});
            skLineSegment(sketch, "E1083", {"start": v(5519.07, 8420.51) * mm, "end": v(5494.63, 8420.25) * mm});
            skLineSegment(sketch, "E1084", {"start": v(5494.63, 8420.25) * mm, "end": v(5470.2, 8420) * mm});
            skLineSegment(sketch, "E1085", {"start": v(5470.2, 8420) * mm, "end": v(5445.78, 8419.76) * mm});
            skLineSegment(sketch, "E1086", {"start": v(5445.78, 8419.76) * mm, "end": v(5421.37, 8419.52) * mm});
            skLineSegment(sketch, "E1087", {"start": v(5421.37, 8419.52) * mm, "end": v(5396.96, 8419.3) * mm});
            skLineSegment(sketch, "E1088", {"start": v(5396.96, 8419.3) * mm, "end": v(5372.56, 8419.08) * mm});
            skLineSegment(sketch, "E1089", {"start": v(5372.56, 8419.08) * mm, "end": v(5348.15, 8418.87) * mm});
            skLineSegment(sketch, "E1090", {"start": v(5348.15, 8418.87) * mm, "end": v(5323.76, 8418.68) * mm});
            skLineSegment(sketch, "E1091", {"start": v(5323.76, 8418.68) * mm, "end": v(5299.38, 8418.5) * mm});
            skLineSegment(sketch, "E1092", {"start": v(5299.38, 8418.5) * mm, "end": v(5275.01, 8418.32) * mm});
            skLineSegment(sketch, "E1093", {"start": v(5275.01, 8418.32) * mm, "end": v(5250.63, 8418.17) * mm});
            skLineSegment(sketch, "E1094", {"start": v(5250.63, 8418.17) * mm, "end": v(5226.25, 8418.04) * mm});
            skLineSegment(sketch, "E1095", {"start": v(5226.25, 8418.04) * mm, "end": v(5201.89, 8417.91) * mm});
            skLineSegment(sketch, "E1096", {"start": v(5201.89, 8417.91) * mm, "end": v(5177.52, 8417.8) * mm});
            skLineSegment(sketch, "E1097", {"start": v(5177.52, 8417.8) * mm, "end": v(5153.14, 8417.71) * mm});
            skLineSegment(sketch, "E1098", {"start": v(5153.14, 8417.71) * mm, "end": v(5128.75, 8417.63) * mm});
            skLineSegment(sketch, "E1099", {"start": v(5128.75, 8417.63) * mm, "end": v(5104.37, 8417.56) * mm});
            skLineSegment(sketch, "E1100", {"start": v(5104.37, 8417.56) * mm, "end": v(5080, 8417.5) * mm});
            skLineSegment(sketch, "E1101", {"start": v(5080, 8417.5) * mm, "end": v(5055.63, 8417.45) * mm});
            skLineSegment(sketch, "E1102", {"start": v(5055.63, 8417.45) * mm, "end": v(5031.27, 8417.43) * mm});
            skLineSegment(sketch, "E1103", {"start": v(5031.27, 8417.43) * mm, "end": v(5006.9, 8417.41) * mm});
            skLineSegment(sketch, "E1104", {"start": v(5006.9, 8417.41) * mm, "end": v(4982.55, 8417.42) * mm});
            skLineSegment(sketch, "E1105", {"start": v(4982.55, 8417.42) * mm, "end": v(4958.19, 8417.44) * mm});
            skLineSegment(sketch, "E1106", {"start": v(4958.19, 8417.44) * mm, "end": v(4933.82, 8417.47) * mm});
            skLineSegment(sketch, "E1107", {"start": v(4933.82, 8417.47) * mm, "end": v(4909.44, 8417.52) * mm});
            skLineSegment(sketch, "E1108", {"start": v(4909.44, 8417.52) * mm, "end": v(4885.06, 8417.58) * mm});
            skLineSegment(sketch, "E1109", {"start": v(4885.06, 8417.58) * mm, "end": v(4860.68, 8417.66) * mm});
            skLineSegment(sketch, "E1110", {"start": v(4860.68, 8417.66) * mm, "end": v(4836.31, 8417.74) * mm});
            skLineSegment(sketch, "E1111", {"start": v(4836.31, 8417.74) * mm, "end": v(4811.95, 8417.84) * mm});
            skLineSegment(sketch, "E1112", {"start": v(4811.95, 8417.84) * mm, "end": v(4787.57, 8417.96) * mm});
            skLineSegment(sketch, "E1113", {"start": v(4787.57, 8417.96) * mm, "end": v(4763.2, 8418.1) * mm});
            skLineSegment(sketch, "E1114", {"start": v(4763.2, 8418.1) * mm, "end": v(4738.83, 8418.24) * mm});
            skLineSegment(sketch, "E1115", {"start": v(4738.83, 8418.24) * mm, "end": v(4714.46, 8418.4) * mm});
            skLineSegment(sketch, "E1116", {"start": v(4714.46, 8418.4) * mm, "end": v(4690.09, 8418.58) * mm});
            skLineSegment(sketch, "E1117", {"start": v(4690.09, 8418.58) * mm, "end": v(4665.7, 8418.77) * mm});
            skLineSegment(sketch, "E1118", {"start": v(4665.7, 8418.77) * mm, "end": v(4641.3, 8418.97) * mm});
            skLineSegment(sketch, "E1119", {"start": v(4641.3, 8418.97) * mm, "end": v(4616.9, 8419.18) * mm});
            skLineSegment(sketch, "E1120", {"start": v(4616.9, 8419.18) * mm, "end": v(4592.5, 8419.4) * mm});
            skLineSegment(sketch, "E1121", {"start": v(4592.5, 8419.4) * mm, "end": v(4568.1, 8419.64) * mm});
            skLineSegment(sketch, "E1122", {"start": v(4568.1, 8419.64) * mm, "end": v(4543.68, 8419.89) * mm});
            skLineSegment(sketch, "E1123", {"start": v(4543.68, 8419.89) * mm, "end": v(4519.26, 8420.14) * mm});
            skLineSegment(sketch, "E1124", {"start": v(4519.26, 8420.14) * mm, "end": v(4494.83, 8420.4) * mm});
            skLineSegment(sketch, "E1125", {"start": v(4494.83, 8420.4) * mm, "end": v(4470.4, 8420.67) * mm});
            skLineSegment(sketch, "E1126", {"start": v(4470.4, 8420.67) * mm, "end": v(4445.95, 8420.95) * mm});
            skLineSegment(sketch, "E1127", {"start": v(4445.95, 8420.95) * mm, "end": v(4421.5, 8421.23) * mm});
            skLineSegment(sketch, "E1128", {"start": v(4421.5, 8421.23) * mm, "end": v(4397.02, 8421.5) * mm});
            skLineSegment(sketch, "E1129", {"start": v(4397.02, 8421.5) * mm, "end": v(4372.53, 8421.79) * mm});
            skLineSegment(sketch, "E1130", {"start": v(4372.53, 8421.79) * mm, "end": v(4348.02, 8422.07) * mm});
            skLineSegment(sketch, "E1131", {"start": v(4348.02, 8422.07) * mm, "end": v(4323.49, 8422.33) * mm});
            skLineSegment(sketch, "E1132", {"start": v(4323.49, 8422.33) * mm, "end": v(4298.94, 8422.59) * mm});
            skLineSegment(sketch, "E1133", {"start": v(4298.94, 8422.59) * mm, "end": v(4274.39, 8422.83) * mm});
            skLineSegment(sketch, "E1134", {"start": v(4274.39, 8422.83) * mm, "end": v(4249.81, 8423.06) * mm});
            skLineSegment(sketch, "E1135", {"start": v(4249.81, 8423.06) * mm, "end": v(4225.22, 8423.28) * mm});
            skLineSegment(sketch, "E1136", {"start": v(4225.22, 8423.28) * mm, "end": v(4200.6, 8423.47) * mm});
            skLineSegment(sketch, "E1137", {"start": v(4200.6, 8423.47) * mm, "end": v(4175.94, 8423.63) * mm});
            skLineSegment(sketch, "E1138", {"start": v(4175.94, 8423.63) * mm, "end": v(4151.25, 8423.76) * mm});
            skLineSegment(sketch, "E1139", {"start": v(4151.25, 8423.76) * mm, "end": v(4126.53, 8423.85) * mm});
            skLineSegment(sketch, "E1140", {"start": v(4126.53, 8423.85) * mm, "end": v(4101.79, 8423.9) * mm});
            skLineSegment(sketch, "E1141", {"start": v(4101.79, 8423.9) * mm, "end": v(4077.02, 8423.89) * mm});
            skLineSegment(sketch, "E1142", {"start": v(4077.02, 8423.89) * mm, "end": v(4052.22, 8423.83) * mm});
            skLineSegment(sketch, "E1143", {"start": v(4052.22, 8423.83) * mm, "end": v(4027.4, 8423.71) * mm});
            skLineSegment(sketch, "E1144", {"start": v(4027.4, 8423.71) * mm, "end": v(4002.53, 8423.54) * mm});
            skLineSegment(sketch, "E1145", {"start": v(4002.53, 8423.54) * mm, "end": v(3977.64, 8423.29) * mm});
            skLineSegment(sketch, "E1146", {"start": v(3977.64, 8423.29) * mm, "end": v(3952.72, 8422.97) * mm});
            skLineSegment(sketch, "E1147", {"start": v(3952.72, 8422.97) * mm, "end": v(3927.77, 8422.56) * mm});
            skLineSegment(sketch, "E1148", {"start": v(3927.77, 8422.56) * mm, "end": v(3902.78, 8422.07) * mm});
            skLineSegment(sketch, "E1149", {"start": v(3902.78, 8422.07) * mm, "end": v(3877.74, 8421.49) * mm});
            skLineSegment(sketch, "E1150", {"start": v(3877.74, 8421.49) * mm, "end": v(3852.66, 8420.8) * mm});
            skLineSegment(sketch, "E1151", {"start": v(3852.66, 8420.8) * mm, "end": v(3827.57, 8419.99) * mm});
            skLineSegment(sketch, "E1152", {"start": v(3827.57, 8419.99) * mm, "end": v(3802.45, 8419.07) * mm});
            skLineSegment(sketch, "E1153", {"start": v(3802.45, 8419.07) * mm, "end": v(3777.3, 8418.03) * mm});
            skLineSegment(sketch, "E1154", {"start": v(3777.3, 8418.03) * mm, "end": v(3752.1, 8416.85) * mm});
            skLineSegment(sketch, "E1155", {"start": v(3752.1, 8416.85) * mm, "end": v(3726.9, 8415.55) * mm});
            skLineSegment(sketch, "E1156", {"start": v(3726.9, 8415.55) * mm, "end": v(3701.69, 8414.1) * mm});
            skLineSegment(sketch, "E1157", {"start": v(3701.69, 8414.1) * mm, "end": v(3676.46, 8412.51) * mm});
            skLineSegment(sketch, "E1158", {"start": v(3676.46, 8412.51) * mm, "end": v(3651.19, 8410.78) * mm});
            skLineSegment(sketch, "E1159", {"start": v(3651.19, 8410.78) * mm, "end": v(3625.9, 8408.88) * mm});
            skLineSegment(sketch, "E1160", {"start": v(3625.9, 8408.88) * mm, "end": v(3600.6, 8406.82) * mm});
            skLineSegment(sketch, "E1161", {"start": v(3600.6, 8406.82) * mm, "end": v(3575.3, 8404.59) * mm});
            skLineSegment(sketch, "E1162", {"start": v(3575.3, 8404.59) * mm, "end": v(3549.96, 8402.19) * mm});
            skLineSegment(sketch, "E1163", {"start": v(3549.96, 8402.19) * mm, "end": v(3524.63, 8399.6) * mm});
            skLineSegment(sketch, "E1164", {"start": v(3524.63, 8399.6) * mm, "end": v(3499.31, 8396.84) * mm});
            skLineSegment(sketch, "E1165", {"start": v(3499.31, 8396.84) * mm, "end": v(3474.02, 8393.9) * mm});
            skLineSegment(sketch, "E1166", {"start": v(3474.02, 8393.9) * mm, "end": v(3449.1, 8390.83) * mm});
            skLineSegment(sketch, "E1167", {"start": v(3449.1, 8390.83) * mm, "end": v(3349.51, 8378.55) * mm});
            skLineSegment(sketch, "E1168", {"start": v(3349.51, 8378.55) * mm, "end": v(3362.13, 8279) * mm});
            skLineSegment(sketch, "E1169", {"start": v(3362.13, 8279) * mm, "end": v(3373.74, 8187.84) * mm});
            skLineSegment(sketch, "E1170", {"start": v(3373.74, 8187.84) * mm, "end": v(3386.34, 8089.05) * mm});
            skLineSegment(sketch, "E1171", {"start": v(3386.34, 8089.05) * mm, "end": v(3485.17, 8101.24) * mm});
            skLineSegment(sketch, "E1172", {"start": v(3485.17, 8101.24) * mm, "end": v(3508.82, 8104.15) * mm});
            skLineSegment(sketch, "E1173", {"start": v(3508.82, 8104.15) * mm, "end": v(3532.15, 8106.86) * mm});
            skLineSegment(sketch, "E1174", {"start": v(3532.15, 8106.86) * mm, "end": v(3555.48, 8109.4) * mm});
            skLineSegment(sketch, "E1175", {"start": v(3555.48, 8109.4) * mm, "end": v(3578.83, 8111.78) * mm});
            skLineSegment(sketch, "E1176", {"start": v(3578.83, 8111.78) * mm, "end": v(3602.22, 8114) * mm});
            skLineSegment(sketch, "E1177", {"start": v(3602.22, 8114) * mm, "end": v(3625.65, 8116.05) * mm});
            skLineSegment(sketch, "E1178", {"start": v(3625.65, 8116.05) * mm, "end": v(3649.13, 8117.96) * mm});
            skLineSegment(sketch, "E1179", {"start": v(3649.13, 8117.96) * mm, "end": v(3672.63, 8119.71) * mm});
            skLineSegment(sketch, "E1180", {"start": v(3672.63, 8119.71) * mm, "end": v(3696.19, 8121.33) * mm});
            skLineSegment(sketch, "E1181", {"start": v(3696.19, 8121.33) * mm, "end": v(3719.8, 8122.8) * mm});
            skLineSegment(sketch, "E1182", {"start": v(3719.8, 8122.8) * mm, "end": v(3743.44, 8124.15) * mm});
            skLineSegment(sketch, "E1183", {"start": v(3743.44, 8124.15) * mm, "end": v(3767.1, 8125.38) * mm});
            skLineSegment(sketch, "E1184", {"start": v(3767.1, 8125.38) * mm, "end": v(3790.8, 8126.48) * mm});
            skLineSegment(sketch, "E1185", {"start": v(3790.8, 8126.48) * mm, "end": v(3814.53, 8127.45) * mm});
            skLineSegment(sketch, "E1186", {"start": v(3814.53, 8127.45) * mm, "end": v(3838.3, 8128.32) * mm});
            skLineSegment(sketch, "E1187", {"start": v(3838.3, 8128.32) * mm, "end": v(3862.12, 8129.08) * mm});
            skLineSegment(sketch, "E1188", {"start": v(3862.12, 8129.08) * mm, "end": v(3885.96, 8129.74) * mm});
            skLineSegment(sketch, "E1189", {"start": v(3885.96, 8129.74) * mm, "end": v(3909.83, 8130.3) * mm});
            skLineSegment(sketch, "E1190", {"start": v(3909.83, 8130.3) * mm, "end": v(3933.76, 8130.76) * mm});
            skLineSegment(sketch, "E1191", {"start": v(3933.76, 8130.76) * mm, "end": v(3957.73, 8131.15) * mm});
            skLineSegment(sketch, "E1192", {"start": v(3957.73, 8131.15) * mm, "end": v(3981.73, 8131.45) * mm});
            skLineSegment(sketch, "E1193", {"start": v(3981.73, 8131.45) * mm, "end": v(4005.76, 8131.7) * mm});
            skLineSegment(sketch, "E1194", {"start": v(4005.76, 8131.7) * mm, "end": v(4029.83, 8131.86) * mm});
            skLineSegment(sketch, "E1195", {"start": v(4029.83, 8131.86) * mm, "end": v(4053.93, 8131.97) * mm});
            skLineSegment(sketch, "E1196", {"start": v(4053.93, 8131.97) * mm, "end": v(4078.05, 8132.02) * mm});
            skLineSegment(sketch, "E1197", {"start": v(4078.05, 8132.02) * mm, "end": v(4102.2, 8132.02) * mm});
            skLineSegment(sketch, "E1198", {"start": v(4102.2, 8132.02) * mm, "end": v(4126.38, 8131.97) * mm});
            skLineSegment(sketch, "E1199", {"start": v(4126.38, 8131.97) * mm, "end": v(4150.6, 8131.88) * mm});
            skLineSegment(sketch, "E1200", {"start": v(4150.6, 8131.88) * mm, "end": v(4174.84, 8131.76) * mm});
            skLineSegment(sketch, "E1201", {"start": v(4174.84, 8131.76) * mm, "end": v(4199.11, 8131.6) * mm});
            skLineSegment(sketch, "E1202", {"start": v(4199.11, 8131.6) * mm, "end": v(4223.4, 8131.41) * mm});
            skLineSegment(sketch, "E1203", {"start": v(4223.4, 8131.41) * mm, "end": v(4247.74, 8131.2) * mm});
            skLineSegment(sketch, "E1204", {"start": v(4247.74, 8131.2) * mm, "end": v(4272.08, 8130.97) * mm});
            skLineSegment(sketch, "E1205", {"start": v(4272.08, 8130.97) * mm, "end": v(4296.45, 8130.73) * mm});
            skLineSegment(sketch, "E1206", {"start": v(4296.45, 8130.73) * mm, "end": v(4320.83, 8130.48) * mm});
            skLineSegment(sketch, "E1207", {"start": v(4320.83, 8130.48) * mm, "end": v(4345.21, 8130.22) * mm});
            skLineSegment(sketch, "E1208", {"start": v(4345.21, 8130.22) * mm, "end": v(4369.62, 8129.94) * mm});
            skLineSegment(sketch, "E1209", {"start": v(4369.62, 8129.94) * mm, "end": v(4394.05, 8129.66) * mm});
            skLineSegment(sketch, "E1210", {"start": v(4394.05, 8129.66) * mm, "end": v(4418.5, 8129.38) * mm});
            skLineSegment(sketch, "E1211", {"start": v(4418.5, 8129.38) * mm, "end": v(4442.96, 8129.1) * mm});
            skLineSegment(sketch, "E1212", {"start": v(4442.96, 8129.1) * mm, "end": v(4467.43, 8128.82) * mm});
            skLineSegment(sketch, "E1213", {"start": v(4467.43, 8128.82) * mm, "end": v(4491.92, 8128.54) * mm});
            skLineSegment(sketch, "E1214", {"start": v(4491.92, 8128.54) * mm, "end": v(4516.4, 8128.28) * mm});
            skLineSegment(sketch, "E1215", {"start": v(4516.4, 8128.28) * mm, "end": v(4540.9, 8128.02) * mm});
            skLineSegment(sketch, "E1216", {"start": v(4540.9, 8128.02) * mm, "end": v(4565.4, 8127.77) * mm});
            skLineSegment(sketch, "E1217", {"start": v(4565.4, 8127.77) * mm, "end": v(4589.91, 8127.54) * mm});
            skLineSegment(sketch, "E1218", {"start": v(4589.91, 8127.54) * mm, "end": v(4614.43, 8127.3) * mm});
            skLineSegment(sketch, "E1219", {"start": v(4614.43, 8127.3) * mm, "end": v(4638.94, 8127.1) * mm});
            skLineSegment(sketch, "E1220", {"start": v(4638.94, 8127.1) * mm, "end": v(4663.46, 8126.89) * mm});
            skLineSegment(sketch, "E1221", {"start": v(4663.46, 8126.89) * mm, "end": v(4687.98, 8126.7) * mm});
            skLineSegment(sketch, "E1222", {"start": v(4687.98, 8126.7) * mm, "end": v(4712.52, 8126.51) * mm});
            skLineSegment(sketch, "E1223", {"start": v(4712.52, 8126.51) * mm, "end": v(4737.06, 8126.35) * mm});
            skLineSegment(sketch, "E1224", {"start": v(4737.06, 8126.35) * mm, "end": v(4761.6, 8126.2) * mm});
            skLineSegment(sketch, "E1225", {"start": v(4761.6, 8126.2) * mm, "end": v(4786.13, 8126.07) * mm});
            skLineSegment(sketch, "E1226", {"start": v(4786.13, 8126.07) * mm, "end": v(4810.67, 8125.95) * mm});
            skLineSegment(sketch, "E1227", {"start": v(4810.67, 8125.95) * mm, "end": v(4835.2, 8125.85) * mm});
            skLineSegment(sketch, "E1228", {"start": v(4835.2, 8125.85) * mm, "end": v(4859.74, 8125.76) * mm});
            skLineSegment(sketch, "E1229", {"start": v(4859.74, 8125.76) * mm, "end": v(4884.27, 8125.69) * mm});
            skLineSegment(sketch, "E1230", {"start": v(4884.27, 8125.69) * mm, "end": v(4908.8, 8125.62) * mm});
            skLineSegment(sketch, "E1231", {"start": v(4908.8, 8125.62) * mm, "end": v(4933.32, 8125.57) * mm});
            skLineSegment(sketch, "E1232", {"start": v(4933.32, 8125.57) * mm, "end": v(4957.86, 8125.53) * mm});
            skLineSegment(sketch, "E1233", {"start": v(4957.86, 8125.53) * mm, "end": v(4982.4, 8125.51) * mm});
            skLineSegment(sketch, "E1234", {"start": v(4982.4, 8125.51) * mm, "end": v(5006.96, 8125.5) * mm});
            skLineSegment(sketch, "E1235", {"start": v(5006.96, 8125.5) * mm, "end": v(5031.5, 8125.52) * mm});
            skLineSegment(sketch, "E1236", {"start": v(5031.5, 8125.52) * mm, "end": v(5056.05, 8125.55) * mm});
            skLineSegment(sketch, "E1237", {"start": v(5056.05, 8125.55) * mm, "end": v(5080.6, 8125.6) * mm});
            skLineSegment(sketch, "E1238", {"start": v(5080.6, 8125.6) * mm, "end": v(5105.12, 8125.66) * mm});
            skLineSegment(sketch, "E1239", {"start": v(5105.12, 8125.66) * mm, "end": v(5129.65, 8125.73) * mm});
            skLineSegment(sketch, "E1240", {"start": v(5129.65, 8125.73) * mm, "end": v(5154.17, 8125.82) * mm});
            skLineSegment(sketch, "E1241", {"start": v(5154.17, 8125.82) * mm, "end": v(5178.7, 8125.91) * mm});
            skLineSegment(sketch, "E1242", {"start": v(5178.7, 8125.91) * mm, "end": v(5203.23, 8126.02) * mm});
            skLineSegment(sketch, "E1243", {"start": v(5203.23, 8126.02) * mm, "end": v(5227.77, 8126.15) * mm});
            skLineSegment(sketch, "E1244", {"start": v(5227.77, 8126.15) * mm, "end": v(5252.3, 8126.29) * mm});
            skLineSegment(sketch, "E1245", {"start": v(5252.3, 8126.29) * mm, "end": v(5276.84, 8126.44) * mm});
            skLineSegment(sketch, "E1246", {"start": v(5276.84, 8126.44) * mm, "end": v(5301.37, 8126.6) * mm});
            skLineSegment(sketch, "E1247", {"start": v(5301.37, 8126.6) * mm, "end": v(5325.9, 8126.8) * mm});
            skLineSegment(sketch, "E1248", {"start": v(5325.9, 8126.8) * mm, "end": v(5350.43, 8127) * mm});
            skLineSegment(sketch, "E1249", {"start": v(5350.43, 8127) * mm, "end": v(5374.94, 8127.2) * mm});
            skLineSegment(sketch, "E1250", {"start": v(5374.94, 8127.2) * mm, "end": v(5399.44, 8127.42) * mm});
            skLineSegment(sketch, "E1251", {"start": v(5399.44, 8127.42) * mm, "end": v(5423.95, 8127.65) * mm});
            skLineSegment(sketch, "E1252", {"start": v(5423.95, 8127.65) * mm, "end": v(5448.46, 8127.89) * mm});
            skLineSegment(sketch, "E1253", {"start": v(5448.46, 8127.89) * mm, "end": v(5472.95, 8128.14) * mm});
            skLineSegment(sketch, "E1254", {"start": v(5472.95, 8128.14) * mm, "end": v(5497.44, 8128.4) * mm});
            skLineSegment(sketch, "E1255", {"start": v(5497.44, 8128.4) * mm, "end": v(5521.92, 8128.65) * mm});
            skLineSegment(sketch, "E1256", {"start": v(5521.92, 8128.65) * mm, "end": v(5546.4, 8128.92) * mm});
            skLineSegment(sketch, "E1257", {"start": v(5546.4, 8128.92) * mm, "end": v(5570.86, 8129.2) * mm});
            skLineSegment(sketch, "E1258", {"start": v(5570.86, 8129.2) * mm, "end": v(5595.4, 8129.47) * mm});
            skLineSegment(sketch, "E1259", {"start": v(5595.4, 8129.47) * mm, "end": v(5620.13, 8129.74) * mm});
            skLineSegment(sketch, "E1260", {"start": v(5620.13, 8129.74) * mm, "end": v(5644.85, 8130.02) * mm});
            skLineSegment(sketch, "E1261", {"start": v(5644.85, 8130.02) * mm, "end": v(5669.54, 8130.3) * mm});
            skLineSegment(sketch, "E1262", {"start": v(5669.54, 8130.3) * mm, "end": v(5694.2, 8130.56) * mm});
            skLineSegment(sketch, "E1263", {"start": v(5694.2, 8130.56) * mm, "end": v(5718.86, 8130.8) * mm});
            skLineSegment(sketch, "E1264", {"start": v(5718.86, 8130.8) * mm, "end": v(5743.5, 8131.03) * mm});
            skLineSegment(sketch, "E1265", {"start": v(5743.5, 8131.03) * mm, "end": v(5768.13, 8131.25) * mm});
            skLineSegment(sketch, "E1266", {"start": v(5768.13, 8131.25) * mm, "end": v(5792.73, 8131.45) * mm});
            skLineSegment(sketch, "E1267", {"start": v(5792.73, 8131.45) * mm, "end": v(5817.3, 8131.62) * mm});
            skLineSegment(sketch, "E1268", {"start": v(5817.3, 8131.62) * mm, "end": v(5841.86, 8131.76) * mm});
            skLineSegment(sketch, "E1269", {"start": v(5841.86, 8131.76) * mm, "end": v(5866.37, 8131.87) * mm});
            skLineSegment(sketch, "E1270", {"start": v(5866.37, 8131.87) * mm, "end": v(5890.84, 8131.94) * mm});
            skLineSegment(sketch, "E1271", {"start": v(5890.84, 8131.94) * mm, "end": v(5915.3, 8131.96) * mm});
            skLineSegment(sketch, "E1272", {"start": v(5915.3, 8131.96) * mm, "end": v(5939.72, 8131.93) * mm});
            skLineSegment(sketch, "E1273", {"start": v(5939.72, 8131.93) * mm, "end": v(5964.1, 8131.84) * mm});
            skLineSegment(sketch, "E1274", {"start": v(5964.1, 8131.84) * mm, "end": v(5988.47, 8131.7) * mm});
            skLineSegment(sketch, "E1275", {"start": v(5988.47, 8131.7) * mm, "end": v(6012.8, 8131.48) * mm});
            skLineSegment(sketch, "E1276", {"start": v(6012.8, 8131.48) * mm, "end": v(6037.1, 8131.2) * mm});
            skLineSegment(sketch, "E1277", {"start": v(6037.1, 8131.2) * mm, "end": v(6061.35, 8130.84) * mm});
            skLineSegment(sketch, "E1278", {"start": v(6061.35, 8130.84) * mm, "end": v(6085.58, 8130.4) * mm});
            skLineSegment(sketch, "E1279", {"start": v(6085.58, 8130.4) * mm, "end": v(6109.76, 8129.87) * mm});
            skLineSegment(sketch, "E1280", {"start": v(6109.76, 8129.87) * mm, "end": v(6133.9, 8129.24) * mm});
            skLineSegment(sketch, "E1281", {"start": v(6133.9, 8129.24) * mm, "end": v(6157.98, 8128.5) * mm});
            skLineSegment(sketch, "E1282", {"start": v(6157.98, 8128.5) * mm, "end": v(6182.05, 8127.66) * mm});
            skLineSegment(sketch, "E1283", {"start": v(6182.05, 8127.66) * mm, "end": v(6206.08, 8126.7) * mm});
            skLineSegment(sketch, "E1284", {"start": v(6206.08, 8126.7) * mm, "end": v(6230.06, 8125.63) * mm});
            skLineSegment(sketch, "E1285", {"start": v(6230.06, 8125.63) * mm, "end": v(6254, 8124.43) * mm});
            skLineSegment(sketch, "E1286", {"start": v(6254, 8124.43) * mm, "end": v(6277.93, 8123.1) * mm});
            skLineSegment(sketch, "E1287", {"start": v(6277.93, 8123.1) * mm, "end": v(6301.82, 8121.63) * mm});
            skLineSegment(sketch, "E1288", {"start": v(6301.82, 8121.63) * mm, "end": v(6325.67, 8120.03) * mm});
            skLineSegment(sketch, "E1289", {"start": v(6325.67, 8120.03) * mm, "end": v(6349.66, 8118.27) * mm});
            skLineSegment(sketch, "E1290", {"start": v(6349.66, 8118.27) * mm, "end": v(6374.21, 8116.32) * mm});
            skLineSegment(sketch, "E1291", {"start": v(6374.21, 8116.32) * mm, "end": v(6398.7, 8114.2) * mm});
            skLineSegment(sketch, "E1292", {"start": v(6398.7, 8114.2) * mm, "end": v(6423.15, 8111.92) * mm});
            skLineSegment(sketch, "E1293", {"start": v(6423.15, 8111.92) * mm, "end": v(6447.55, 8109.46) * mm});
            skLineSegment(sketch, "E1294", {"start": v(6447.55, 8109.46) * mm, "end": v(6471.91, 8106.81) * mm});
            skLineSegment(sketch, "E1295", {"start": v(6471.91, 8106.81) * mm, "end": v(6496.27, 8103.98) * mm});
            skLineSegment(sketch, "E1296", {"start": v(6496.27, 8103.98) * mm, "end": v(6520.97, 8100.92) * mm});
            skLineSegment(sketch, "E1297", {"start": v(6520.97, 8100.92) * mm, "end": v(6619.79, 8088.7) * mm});
            skLineSegment(sketch, "E1298", {"start": v(6619.79, 8088.7) * mm, "end": v(6632.44, 8187.46) * mm});
            skLineSegment(sketch, "E1299", {"start": v(6632.44, 8187.46) * mm, "end": v(6644.1, 8278.6) * mm});
            skLineSegment(sketch, "E1300", {"start": v(6644.1, 8278.6) * mm, "end": v(6656.8, 8378.16) * mm});
            skLineSegment(sketch, "E1301", {"start": v(6656.8, 8378.16) * mm, "end": v(6557.2, 8390.5) * mm});
            skLineSegment(sketch, "E1302", {"start": v(6557.2, 8390.5) * mm, "end": v(6531.16, 8393.71) * mm});
            skLineSegment(sketch, "E1303", {"start": v(1245.46, 3491) * mm, "end": v(1232.71, 3506.5) * mm});
            skLineSegment(sketch, "E1304", {"start": v(1232.71, 3506.5) * mm, "end": v(1220.38, 3522.13) * mm});
            skLineSegment(sketch, "E1305", {"start": v(1220.38, 3522.13) * mm, "end": v(1208.47, 3537.87) * mm});
            skLineSegment(sketch, "E1306", {"start": v(1208.47, 3537.87) * mm, "end": v(1197, 3553.7) * mm});
            skLineSegment(sketch, "E1307", {"start": v(1197, 3553.7) * mm, "end": v(1185.94, 3569.62) * mm});
            skLineSegment(sketch, "E1308", {"start": v(1185.94, 3569.62) * mm, "end": v(1175.31, 3585.63) * mm});
            skLineSegment(sketch, "E1309", {"start": v(1175.31, 3585.63) * mm, "end": v(1165.12, 3601.72) * mm});
            skLineSegment(sketch, "E1310", {"start": v(1165.12, 3601.72) * mm, "end": v(1155.36, 3617.87) * mm});
            skLineSegment(sketch, "E1311", {"start": v(1155.36, 3617.87) * mm, "end": v(1146.02, 3634.08) * mm});
            skLineSegment(sketch, "E1312", {"start": v(1146.02, 3634.08) * mm, "end": v(1137.12, 3650.35) * mm});
            skLineSegment(sketch, "E1313", {"start": v(1137.12, 3650.35) * mm, "end": v(1128.64, 3666.65) * mm});
            skLineSegment(sketch, "E1314", {"start": v(1128.64, 3666.65) * mm, "end": v(1120.6, 3683) * mm});
            skLineSegment(sketch, "E1315", {"start": v(1120.6, 3683) * mm, "end": v(1112.98, 3699.37) * mm});
            skLineSegment(sketch, "E1316", {"start": v(1112.98, 3699.37) * mm, "end": v(1105.8, 3715.76) * mm});
            skLineSegment(sketch, "E1317", {"start": v(1105.8, 3715.76) * mm, "end": v(1099.02, 3732.16) * mm});
            skLineSegment(sketch, "E1318", {"start": v(1099.02, 3732.16) * mm, "end": v(1092.68, 3748.57) * mm});
            skLineSegment(sketch, "E1319", {"start": v(1092.68, 3748.57) * mm, "end": v(1086.75, 3764.97) * mm});
            skLineSegment(sketch, "E1320", {"start": v(1086.75, 3764.97) * mm, "end": v(1081.24, 3781.37) * mm});
            skLineSegment(sketch, "E1321", {"start": v(1081.24, 3781.37) * mm, "end": v(1076.14, 3797.75) * mm});
            skLineSegment(sketch, "E1322", {"start": v(1076.14, 3797.75) * mm, "end": v(1071.45, 3814.1) * mm});
            skLineSegment(sketch, "E1323", {"start": v(1071.45, 3814.1) * mm, "end": v(1067.16, 3830.43) * mm});
            skLineSegment(sketch, "E1324", {"start": v(1067.16, 3830.43) * mm, "end": v(1063.27, 3846.71) * mm});
            skLineSegment(sketch, "E1325", {"start": v(1063.27, 3846.71) * mm, "end": v(1059.78, 3862.96) * mm});
            skLineSegment(sketch, "E1326", {"start": v(1059.78, 3862.96) * mm, "end": v(1056.68, 3879.15) * mm});
            skLineSegment(sketch, "E1327", {"start": v(1056.68, 3879.15) * mm, "end": v(1053.96, 3895.29) * mm});
            skLineSegment(sketch, "E1328", {"start": v(1053.96, 3895.29) * mm, "end": v(1051.63, 3911.36) * mm});
            skLineSegment(sketch, "E1329", {"start": v(1051.63, 3911.36) * mm, "end": v(1049.67, 3927.37) * mm});
            skLineSegment(sketch, "E1330", {"start": v(1049.67, 3927.37) * mm, "end": v(1048.08, 3943.3) * mm});
            skLineSegment(sketch, "E1331", {"start": v(1048.08, 3943.3) * mm, "end": v(1046.85, 3959.16) * mm});
            skLineSegment(sketch, "E1332", {"start": v(1046.85, 3959.16) * mm, "end": v(1045.99, 3974.93) * mm});
            skLineSegment(sketch, "E1333", {"start": v(1045.99, 3974.93) * mm, "end": v(1045.47, 3990.61) * mm});
            skLineSegment(sketch, "E1334", {"start": v(1045.47, 3990.61) * mm, "end": v(1045.3, 4006.2) * mm});
            skLineSegment(sketch, "E1335", {"start": v(1045.3, 4006.2) * mm, "end": v(1045.56, 4025.27) * mm});
            skLineSegment(sketch, "E1336", {"start": v(1045.56, 4025.27) * mm, "end": v(1046.33, 4044.49) * mm});
            skLineSegment(sketch, "E1337", {"start": v(1046.33, 4044.49) * mm, "end": v(1047.63, 4063.83) * mm});
            skLineSegment(sketch, "E1338", {"start": v(1047.63, 4063.83) * mm, "end": v(1049.48, 4083.3) * mm});
            skLineSegment(sketch, "E1339", {"start": v(1049.48, 4083.3) * mm, "end": v(1051.88, 4102.87) * mm});
            skLineSegment(sketch, "E1340", {"start": v(1051.88, 4102.87) * mm, "end": v(1054.84, 4122.55) * mm});
            skLineSegment(sketch, "E1341", {"start": v(1054.84, 4122.55) * mm, "end": v(1058.37, 4142.31) * mm});
            skLineSegment(sketch, "E1342", {"start": v(1058.37, 4142.31) * mm, "end": v(1062.48, 4162.15) * mm});
            skLineSegment(sketch, "E1343", {"start": v(1062.48, 4162.15) * mm, "end": v(1067.18, 4182.06) * mm});
            skLineSegment(sketch, "E1344", {"start": v(1067.18, 4182.06) * mm, "end": v(1072.48, 4202.03) * mm});
            skLineSegment(sketch, "E1345", {"start": v(1072.48, 4202.03) * mm, "end": v(1078.39, 4222.04) * mm});
            skLineSegment(sketch, "E1346", {"start": v(1078.39, 4222.04) * mm, "end": v(1084.9, 4242.08) * mm});
            skLineSegment(sketch, "E1347", {"start": v(1084.9, 4242.08) * mm, "end": v(1092.05, 4262.14) * mm});
            skLineSegment(sketch, "E1348", {"start": v(1092.05, 4262.14) * mm, "end": v(1099.81, 4282.2) * mm});
            skLineSegment(sketch, "E1349", {"start": v(1099.81, 4282.2) * mm, "end": v(1108.2, 4302.26) * mm});
            skLineSegment(sketch, "E1350", {"start": v(1108.2, 4302.26) * mm, "end": v(1117.24, 4322.3) * mm});
            skLineSegment(sketch, "E1351", {"start": v(1117.24, 4322.3) * mm, "end": v(1126.9, 4342.29) * mm});
            skLineSegment(sketch, "E1352", {"start": v(1126.9, 4342.29) * mm, "end": v(1137.22, 4362.23) * mm});
            skLineSegment(sketch, "E1353", {"start": v(1137.22, 4362.23) * mm, "end": v(1148.17, 4382.12) * mm});
            skLineSegment(sketch, "E1354", {"start": v(1148.17, 4382.12) * mm, "end": v(1159.76, 4401.92) * mm});
            skLineSegment(sketch, "E1355", {"start": v(1159.76, 4401.92) * mm, "end": v(1172, 4421.62) * mm});
            skLineSegment(sketch, "E1356", {"start": v(1172, 4421.62) * mm, "end": v(1184.89, 4441.22) * mm});
            skLineSegment(sketch, "E1357", {"start": v(1184.89, 4441.22) * mm, "end": v(1198.41, 4460.7) * mm});
            skLineSegment(sketch, "E1358", {"start": v(1198.41, 4460.7) * mm, "end": v(1212.57, 4480.03) * mm});
            skLineSegment(sketch, "E1359", {"start": v(1212.57, 4480.03) * mm, "end": v(1227.37, 4499.2) * mm});
            skLineSegment(sketch, "E1360", {"start": v(1227.37, 4499.2) * mm, "end": v(1242.8, 4518.21) * mm});
            skLineSegment(sketch, "E1361", {"start": v(1242.8, 4518.21) * mm, "end": v(1258.86, 4537.04) * mm});
            skLineSegment(sketch, "E1362", {"start": v(1258.86, 4537.04) * mm, "end": v(1275.53, 4555.66) * mm});
            skLineSegment(sketch, "E1363", {"start": v(1275.53, 4555.66) * mm, "end": v(1292.82, 4574.08) * mm});
            skLineSegment(sketch, "E1364", {"start": v(1292.82, 4574.08) * mm, "end": v(1310.71, 4592.26) * mm});
            skLineSegment(sketch, "E1365", {"start": v(1310.71, 4592.26) * mm, "end": v(1329.2, 4610.2) * mm});
            skLineSegment(sketch, "E1366", {"start": v(1329.2, 4610.2) * mm, "end": v(1348.27, 4627.88) * mm});
            skLineSegment(sketch, "E1367", {"start": v(1348.27, 4627.88) * mm, "end": v(1382.61, 4657.83) * mm});
            skLineSegment(sketch, "E1368", {"start": v(1382.61, 4657.83) * mm, "end": v(1418.06, 4686.47) * mm});
            skLineSegment(sketch, "E1369", {"start": v(1418.06, 4686.47) * mm, "end": v(1445.22, 4707.04) * mm});
            skLineSegment(sketch, "E1370", {"start": v(1445.22, 4707.04) * mm, "end": v(1473.19, 4727.07) * mm});
            skLineSegment(sketch, "E1371", {"start": v(1473.19, 4727.07) * mm, "end": v(1501.93, 4746.56) * mm});
            skLineSegment(sketch, "E1372", {"start": v(1501.93, 4746.56) * mm, "end": v(1531.42, 4765.48) * mm});
            skLineSegment(sketch, "E1373", {"start": v(1531.42, 4765.48) * mm, "end": v(1561.62, 4783.81) * mm});
            skLineSegment(sketch, "E1374", {"start": v(1561.62, 4783.81) * mm, "end": v(1592.49, 4801.54) * mm});
            skLineSegment(sketch, "E1375", {"start": v(1592.49, 4801.54) * mm, "end": v(1624, 4818.63) * mm});
            skLineSegment(sketch, "E1376", {"start": v(1624, 4818.63) * mm, "end": v(1656.1, 4835.09) * mm});
            skLineSegment(sketch, "E1377", {"start": v(1656.1, 4835.09) * mm, "end": v(1688.75, 4850.88) * mm});
            skLineSegment(sketch, "E1378", {"start": v(1688.75, 4850.88) * mm, "end": v(1721.92, 4866) * mm});
            skLineSegment(sketch, "E1379", {"start": v(1721.92, 4866) * mm, "end": v(1755.57, 4880.46) * mm});
            skLineSegment(sketch, "E1380", {"start": v(1755.57, 4880.46) * mm, "end": v(1789.64, 4894.21) * mm});
            skLineSegment(sketch, "E1381", {"start": v(1789.64, 4894.21) * mm, "end": v(1824.1, 4907.27) * mm});
            skLineSegment(sketch, "E1382", {"start": v(1824.1, 4907.27) * mm, "end": v(1858.92, 4919.62) * mm});
            skLineSegment(sketch, "E1383", {"start": v(1858.92, 4919.62) * mm, "end": v(1894.04, 4931.26) * mm});
            skLineSegment(sketch, "E1384", {"start": v(1894.04, 4931.26) * mm, "end": v(1929.41, 4942.2) * mm});
            skLineSegment(sketch, "E1385", {"start": v(1929.41, 4942.2) * mm, "end": v(1965, 4952.41) * mm});
            skLineSegment(sketch, "E1386", {"start": v(1965, 4952.41) * mm, "end": v(2000.78, 4961.92) * mm});
            skLineSegment(sketch, "E1387", {"start": v(2000.78, 4961.92) * mm, "end": v(2036.68, 4970.7) * mm});
            skLineSegment(sketch, "E1388", {"start": v(2036.68, 4970.7) * mm, "end": v(2072.68, 4978.8) * mm});
            skLineSegment(sketch, "E1389", {"start": v(2072.68, 4978.8) * mm, "end": v(2108.73, 4986.17) * mm});
            skLineSegment(sketch, "E1390", {"start": v(2108.73, 4986.17) * mm, "end": v(2144.8, 4992.85) * mm});
            skLineSegment(sketch, "E1391", {"start": v(2144.8, 4992.85) * mm, "end": v(2180.85, 4998.84) * mm});
            skLineSegment(sketch, "E1392", {"start": v(2180.85, 4998.84) * mm, "end": v(2216.83, 5004.15) * mm});
            skLineSegment(sketch, "E1393", {"start": v(2216.83, 5004.15) * mm, "end": v(2252.72, 5008.79) * mm});
            skLineSegment(sketch, "E1394", {"start": v(2252.72, 5008.79) * mm, "end": v(2288.47, 5012.76) * mm});
            skLineSegment(sketch, "E1395", {"start": v(2288.47, 5012.76) * mm, "end": v(2359.46, 5018.77) * mm});
            skLineSegment(sketch, "E1396", {"start": v(2359.46, 5018.77) * mm, "end": v(2429.55, 5022.3) * mm});
            skLineSegment(sketch, "E1397", {"start": v(2429.55, 5022.3) * mm, "end": v(2498.5, 5023.44) * mm});
            skLineSegment(sketch, "E1398", {"start": v(2498.5, 5023.44) * mm, "end": v(2540.77, 5023.01) * mm});
            skLineSegment(sketch, "E1399", {"start": v(2540.77, 5023.01) * mm, "end": v(2583.5, 5021.7) * mm});
            skLineSegment(sketch, "E1400", {"start": v(2583.5, 5021.7) * mm, "end": v(2626.63, 5019.48) * mm});
            skLineSegment(sketch, "E1401", {"start": v(2626.63, 5019.48) * mm, "end": v(2670.12, 5016.32) * mm});
            skLineSegment(sketch, "E1402", {"start": v(2670.12, 5016.32) * mm, "end": v(2713.9, 5012.2) * mm});
            skLineSegment(sketch, "E1403", {"start": v(2713.9, 5012.2) * mm, "end": v(2757.94, 5007.1) * mm});
            skLineSegment(sketch, "E1404", {"start": v(2757.94, 5007.1) * mm, "end": v(2802.15, 5000.99) * mm});
            skLineSegment(sketch, "E1405", {"start": v(2802.15, 5000.99) * mm, "end": v(2846.47, 4993.85) * mm});
            skLineSegment(sketch, "E1406", {"start": v(2846.47, 4993.85) * mm, "end": v(2890.83, 4985.67) * mm});
            skLineSegment(sketch, "E1407", {"start": v(2890.83, 4985.67) * mm, "end": v(2935.17, 4976.43) * mm});
            skLineSegment(sketch, "E1408", {"start": v(2935.17, 4976.43) * mm, "end": v(2979.41, 4966.12) * mm});
            skLineSegment(sketch, "E1409", {"start": v(2979.41, 4966.12) * mm, "end": v(3023.48, 4954.74) * mm});
            skLineSegment(sketch, "E1410", {"start": v(3023.48, 4954.74) * mm, "end": v(3067.3, 4942.28) * mm});
            skLineSegment(sketch, "E1411", {"start": v(3067.3, 4942.28) * mm, "end": v(3110.78, 4928.75) * mm});
            skLineSegment(sketch, "E1412", {"start": v(3110.78, 4928.75) * mm, "end": v(3153.85, 4914.13) * mm});
            skLineSegment(sketch, "E1413", {"start": v(3153.85, 4914.13) * mm, "end": v(3196.44, 4898.44) * mm});
            skLineSegment(sketch, "E1414", {"start": v(3196.44, 4898.44) * mm, "end": v(3238.46, 4881.7) * mm});
            skLineSegment(sketch, "E1415", {"start": v(3238.46, 4881.7) * mm, "end": v(3279.83, 4863.9) * mm});
            skLineSegment(sketch, "E1416", {"start": v(3279.83, 4863.9) * mm, "end": v(3320.47, 4845.08) * mm});
            skLineSegment(sketch, "E1417", {"start": v(3320.47, 4845.08) * mm, "end": v(3360.32, 4825.25) * mm});
            skLineSegment(sketch, "E1418", {"start": v(3360.32, 4825.25) * mm, "end": v(3399.28, 4804.44) * mm});
            skLineSegment(sketch, "E1419", {"start": v(3399.28, 4804.44) * mm, "end": v(3437.3, 4782.68) * mm});
            skLineSegment(sketch, "E1420", {"start": v(3437.3, 4782.68) * mm, "end": v(3474.29, 4760) * mm});
            skLineSegment(sketch, "E1421", {"start": v(3474.29, 4760) * mm, "end": v(3510.2, 4736.44) * mm});
            skLineSegment(sketch, "E1422", {"start": v(3510.2, 4736.44) * mm, "end": v(3544.95, 4712.04) * mm});
            skLineSegment(sketch, "E1423", {"start": v(3544.95, 4712.04) * mm, "end": v(3578.5, 4686.83) * mm});
            skLineSegment(sketch, "E1424", {"start": v(3578.5, 4686.83) * mm, "end": v(3610.77, 4660.86) * mm});
            skLineSegment(sketch, "E1425", {"start": v(3610.77, 4660.86) * mm, "end": v(3641.73, 4634.19) * mm});
            skLineSegment(sketch, "E1426", {"start": v(3641.73, 4634.19) * mm, "end": v(3656.7, 4620.6) * mm});
            skLineSegment(sketch, "E1427", {"start": v(3656.7, 4620.6) * mm, "end": v(3671.32, 4606.85) * mm});
            skLineSegment(sketch, "E1428", {"start": v(3671.32, 4606.85) * mm, "end": v(3685.6, 4592.95) * mm});
            skLineSegment(sketch, "E1429", {"start": v(3685.6, 4592.95) * mm, "end": v(3699.51, 4578.9) * mm});
            skLineSegment(sketch, "E1430", {"start": v(3699.51, 4578.9) * mm, "end": v(3713.07, 4564.72) * mm});
            skLineSegment(sketch, "E1431", {"start": v(3713.07, 4564.72) * mm, "end": v(3726.26, 4550.4) * mm});
            skLineSegment(sketch, "E1432", {"start": v(3726.26, 4550.4) * mm, "end": v(3739.09, 4535.96) * mm});
            skLineSegment(sketch, "E1433", {"start": v(3739.09, 4535.96) * mm, "end": v(3751.54, 4521.4) * mm});
            skLineSegment(sketch, "E1434", {"start": v(1245.46, 3491) * mm, "end": v(4298.42, -147.37) * mm});
            skLineSegment(sketch, "E1435", {"start": v(3751.54, 4521.4) * mm, "end": v(4298.42, 3869.65) * mm});
            skLineSegment(sketch, "E1436", {"start": v(4298.42, 3869.65) * mm, "end": v(4298.42, -147.37) * mm});
            skArc(sketch, "E1437", {"start": v(6775.49, 10987.2) * mm, "mid": v(-33.9, 15266.85) * mm, "end": v(6775.49, 19546.5) * mm});
            skLineSegment(sketch, "E1438", {"start": v(6775.49, 19546.5) * mm, "end": v(4889.14, 15627.28) * mm});
            skArc(sketch, "E1439", {"start": v(4889.14, 15627.28) * mm, "mid": v(4315.66, 15266.85) * mm, "end": v(4889.14, 14906.42) * mm});
            skLineSegment(sketch, "E1440", {"start": v(4889.14, 14906.42) * mm, "end": v(6775.49, 10987.2) * mm});
            skArc(sketch, "E1441", {"start": v(1649.9, 19457.28) * mm, "mid": v(237.21, 19806.52) * mm, "end": v(535.2, 18382.13) * mm});
            skLineSegment(sketch, "E1442", {"start": v(535.2, 18382.13) * mm, "end": v(833.81, 19187.97) * mm});
            skLineSegment(sketch, "E1443", {"start": v(833.81, 19187.97) * mm, "end": v(1649.9, 19457.28) * mm});
            skArc(sketch, "E1444", {"start": v(1744.87, 19488.62) * mm, "mid": v(167.79, 19878.5) * mm, "end": v(500.45, 18288.36) * mm});
            skLineSegment(sketch, "E1445", {"start": v(500.45, 18288.36) * mm, "end": v(594.22, 18253.61) * mm});
            skLineSegment(sketch, "E1446", {"start": v(594.22, 18253.61) * mm, "end": v(628.96, 18347.38) * mm});
            skLineSegment(sketch, "E1447", {"start": v(628.96, 18347.38) * mm, "end": v(910.86, 19108.09) * mm});
            skLineSegment(sketch, "E1448", {"start": v(910.86, 19108.09) * mm, "end": v(1681.25, 19362.32) * mm});
            skLineSegment(sketch, "E1449", {"start": v(1681.25, 19362.32) * mm, "end": v(1776.2, 19393.66) * mm});
            skLineSegment(sketch, "E1450", {"start": v(1776.2, 19393.66) * mm, "end": v(1744.87, 19488.62) * mm});
            skArc(sketch, "E1451", {"start": v(6818.85, 10897.09) * mm, "mid": v(-133.9, 15266.85) * mm, "end": v(6818.85, 19636.61) * mm});
            skLineSegment(sketch, "E1452", {"start": v(6818.85, 19636.61) * mm, "end": v(6908.96, 19593.24) * mm});
            skLineSegment(sketch, "E1453", {"start": v(6908.96, 19593.24) * mm, "end": v(6865.6, 19503.14) * mm});
            skLineSegment(sketch, "E1454", {"start": v(6865.6, 19503.14) * mm, "end": v(4979.24, 15583.9) * mm});
            skLineSegment(sketch, "E1455", {"start": v(4979.24, 15583.9) * mm, "end": v(4935.88, 15493.8) * mm});
            skLineSegment(sketch, "E1456", {"start": v(4935.88, 15493.8) * mm, "end": v(4845.77, 15537.17) * mm});
            skArc(sketch, "E1457", {"start": v(4845.77, 15537.17) * mm, "mid": v(4415.66, 15266.85) * mm, "end": v(4845.77, 14996.53) * mm});
            skLineSegment(sketch, "E1458", {"start": v(4845.77, 14996.53) * mm, "end": v(4935.88, 15039.9) * mm});
            skLineSegment(sketch, "E1459", {"start": v(4935.88, 15039.9) * mm, "end": v(4979.24, 14949.8) * mm});
            skLineSegment(sketch, "E1460", {"start": v(4979.24, 14949.8) * mm, "end": v(6865.6, 11030.56) * mm});
            skLineSegment(sketch, "E1461", {"start": v(6865.6, 11030.56) * mm, "end": v(6908.96, 10940.45) * mm});
            skLineSegment(sketch, "E1462", {"start": v(6908.96, 10940.45) * mm, "end": v(6818.85, 10897.09) * mm});
            skSolve(sketch);
        }
        {
            var Q0;
            Q0=makeQuery(id+"F0.imprint","IMPRINT",FACE,{"disambiguationData":[TD([[makeQuery(id+"F0.imprint","IMPRINT",EDGE,{"derivedFrom":sQuery(id+"F0.wireOp",EDGE,"E1437")}),-1.0]])]});
            var Q1;
            Q1=makeQuery(id+"F0.imprint","IMPRINT",FACE,{"disambiguationData":[TD([[makeQuery(id+"F0.imprint","IMPRINT",EDGE,{"derivedFrom":sQuery(id+"F0.wireOp",EDGE,"E1437")}),1.0]])]});
            var Q2;
            Q2=makeQuery(id+"F0.imprint","IMPRINT",FACE,{"disambiguationData":[TD([[makeQuery(id+"F0.imprint","IMPRINT",EDGE,{"derivedFrom":sQuery(id+"F0.wireOp",EDGE,"E449")}),1.0]])]});
            var Q3;
            Q3=makeQuery(id+"F0.imprint","IMPRINT",FACE,{"disambiguationData":[TD([[makeQuery(id+"F0.imprint","IMPRINT",EDGE,{"derivedFrom":sQuery(id+"F0.wireOp",EDGE,"E449")}),-1.0]])]});
            var Q4;
            {var subQ3=sQuery(id+"F0.wireOp",EDGE,"E177");Q4=makeQuery(id+"F0.imprint","IMPRINT",FACE,{"disambiguationData":[TD([[makeQuery(id+"F0.imprint","IMPRINT",EDGE,{"derivedFrom":subQ3}),1.0]])]});}
            var Q5;
            {var subQ0=sQuery(id+"F0.wireOp",EDGE,"E182");var subQ1=sQuery(id+"F0.wireOp",EDGE,"E173");var subQ2=makeQuery(id+"F0.imprint","INTERSECT",VERTEX,{"disambiguationData":[OD(0.0)],"derivedFrom":[subQ1,subQ0]});Q5=makeQuery(id+"F0.imprint","IMPRINT",FACE,{"disambiguationData":[TD([[makeQuery(id+"F0.imprint","IMPRINT",EDGE,{"disambiguationData":[TD([[subQ2,-1.0]])],"derivedFrom":subQ1}),1.0]])]});}
            var Q6;
            {var subQ0=sQuery(id+"F0.wireOp",EDGE,"E181");var subQ1=sQuery(id+"F0.wireOp",EDGE,"E173");var subQ2=makeQuery(id+"F0.imprint","INTERSECT",VERTEX,{"disambiguationData":[OD(1.0)],"derivedFrom":[subQ1,subQ0]});Q6=makeQuery(id+"F0.imprint","IMPRINT",FACE,{"disambiguationData":[TD([[makeQuery(id+"F0.imprint","IMPRINT",EDGE,{"disambiguationData":[TD([[subQ2,1.0]])],"derivedFrom":subQ1}),-1.0]])]});}
            var Q7;
            {var subQ0=sQuery(id+"F0.wireOp",EDGE,"E181");var subQ1=sQuery(id+"F0.wireOp",EDGE,"E173");var subQ2=makeQuery(id+"F0.imprint","INTERSECT",VERTEX,{"disambiguationData":[OD(1.0)],"derivedFrom":[subQ1,subQ0]});Q7=makeQuery(id+"F0.imprint","IMPRINT",FACE,{"disambiguationData":[TD([[makeQuery(id+"F0.imprint","IMPRINT",EDGE,{"disambiguationData":[TD([[subQ2,1.0]])],"derivedFrom":subQ1}),1.0]])]});}
            var Q8;
            {var subQ0=sQuery(id+"F0.wireOp",EDGE,"E179");Q8=makeQuery(id+"F0.imprint","IMPRINT",FACE,{"disambiguationData":[TD([[makeQuery(id+"F0.imprint","IMPRINT",EDGE,{"derivedFrom":subQ0}),1.0]])]});}
            var Q9;
            {var subQ0=sQuery(id+"F0.wireOp",EDGE,"E181");var subQ1=sQuery(id+"F0.wireOp",EDGE,"E173");var subQ2=makeQuery(id+"F0.imprint","INTERSECT",VERTEX,{"disambiguationData":[OD(0.0)],"derivedFrom":[subQ1,subQ0]});Q9=makeQuery(id+"F0.imprint","IMPRINT",FACE,{"disambiguationData":[TD([[makeQuery(id+"F0.imprint","IMPRINT",EDGE,{"disambiguationData":[TD([[subQ2,1.0]])],"derivedFrom":subQ1}),1.0]])]});}
            var Q10;
            {var subQ0=sQuery(id+"F0.wireOp",EDGE,"E181");var subQ1=sQuery(id+"F0.wireOp",EDGE,"E173");var subQ2=makeQuery(id+"F0.imprint","INTERSECT",VERTEX,{"disambiguationData":[OD(0.0)],"derivedFrom":[subQ1,subQ0]});Q10=makeQuery(id+"F0.imprint","IMPRINT",FACE,{"disambiguationData":[TD([[makeQuery(id+"F0.imprint","IMPRINT",EDGE,{"disambiguationData":[TD([[subQ2,-1.0]])],"derivedFrom":subQ1}),1.0]])]});}
            var Q11;
            {var subQ0=sQuery(id+"F0.wireOp",EDGE,"E181");var subQ1=sQuery(id+"F0.wireOp",EDGE,"E173");var subQ2=makeQuery(id+"F0.imprint","INTERSECT",VERTEX,{"disambiguationData":[OD(0.0)],"derivedFrom":[subQ1,subQ0]});Q11=makeQuery(id+"F0.imprint","IMPRINT",FACE,{"disambiguationData":[TD([[makeQuery(id+"F0.imprint","IMPRINT",EDGE,{"disambiguationData":[TD([[subQ2,-1.0]])],"derivedFrom":subQ1}),-1.0]])]});}
            var Q12;
            {var subQ0=sQuery(id+"F0.wireOp",EDGE,"E176");Q12=makeQuery(id+"F0.imprint","IMPRINT",FACE,{"disambiguationData":[TD([[makeQuery(id+"F0.imprint","IMPRINT",EDGE,{"derivedFrom":subQ0}),1.0]])]});}
            var Q13;
            {var subQ0=sQuery(id+"F0.wireOp",EDGE,"E182");var subQ1=sQuery(id+"F0.wireOp",EDGE,"E178");var subQ2=makeQuery(id+"F0.imprint","INTERSECT",VERTEX,{"derivedFrom":[subQ1,subQ0]});Q13=makeQuery(id+"F0.imprint","IMPRINT",FACE,{"disambiguationData":[TD([[makeQuery(id+"F0.imprint","IMPRINT",EDGE,{"disambiguationData":[TD([[subQ2,-1.0]])],"derivedFrom":subQ1}),-1.0]])]});}
            var Q14;
            {var subQ0=sQuery(id+"F0.wireOp",EDGE,"E175");Q14=makeQuery(id+"F0.imprint","IMPRINT",FACE,{"disambiguationData":[TD([[makeQuery(id+"F0.imprint","IMPRINT",EDGE,{"derivedFrom":subQ0}),-1.0]])]});}
            var Q15;
            {var subQ0=sQuery(id+"F0.wireOp",EDGE,"E175");Q15=makeQuery(id+"F0.imprint","IMPRINT",FACE,{"disambiguationData":[TD([[makeQuery(id+"F0.imprint","IMPRINT",EDGE,{"derivedFrom":subQ0}),1.0]])]});}
            var Q16;
            {var subQ0=sQuery(id+"F0.wireOp",EDGE,"E176");Q16=makeQuery(id+"F0.imprint","IMPRINT",FACE,{"disambiguationData":[TD([[makeQuery(id+"F0.imprint","IMPRINT",EDGE,{"derivedFrom":subQ0}),-1.0]])]});}
            extrude(context, id + "F1", {"entities" : qUnion([Q0, Q1, Q2, Q3, Q4, Q5, Q6, Q7, Q8, Q9, Q10, Q11, Q12, Q13, Q14, Q15, Q16]), "depth" : 10 * mm, "offsetDistance" : 25 * mm});
        }
        {
            var Q0;
            Q0=makeQuery(id+"F0.imprint","IMPRINT",FACE,{"disambiguationData":[TD([[makeQuery(id+"F0.imprint","IMPRINT",EDGE,{"derivedFrom":sQuery(id+"F0.wireOp",EDGE,"E591")}),1.0]])]});
            var Q1;
            Q1=makeQuery(id+"F0.imprint","IMPRINT",FACE,{"disambiguationData":[TD([[makeQuery(id+"F0.imprint","IMPRINT",EDGE,{"derivedFrom":sQuery(id+"F0.wireOp",EDGE,"E591")}),-1.0]])]});
            var Q2;
            Q2=makeQuery(id+"F0.imprint","IMPRINT",FACE,{"disambiguationData":[TD([[makeQuery(id+"F0.imprint","IMPRINT",EDGE,{"derivedFrom":sQuery(id+"F0.wireOp",EDGE,"E183")}),-1.0]])]});
            var Q3;
            Q3=makeQuery(id+"F0.imprint","IMPRINT",FACE,{"disambiguationData":[TD([[makeQuery(id+"F0.imprint","IMPRINT",EDGE,{"derivedFrom":sQuery(id+"F0.wireOp",EDGE,"E183")}),1.0]])]});
            extrude(context, id + "F2", {"entities" : qUnion([Q0, Q1, Q2, Q3]), "depth" : 10 * mm, "offsetDistance" : 25 * mm});
        }
        {
            var Q0;
            Q0=makeQuery(id+"F0.imprint","IMPRINT",FACE,{"disambiguationData":[TD([[makeQuery(id+"F0.imprint","IMPRINT",EDGE,{"derivedFrom":sQuery(id+"F0.wireOp",EDGE,"E1441")}),1.0]])]});
            var Q1;
            Q1=makeQuery(id+"F0.imprint","IMPRINT",FACE,{"disambiguationData":[TD([[makeQuery(id+"F0.imprint","IMPRINT",EDGE,{"derivedFrom":sQuery(id+"F0.wireOp",EDGE,"E1441")}),-1.0]])]});
            extrude(context, id + "F3", {"entities" : qUnion([Q0, Q1]), "depth" : 10 * mm, "offsetDistance" : 25 * mm});
        }
    });
